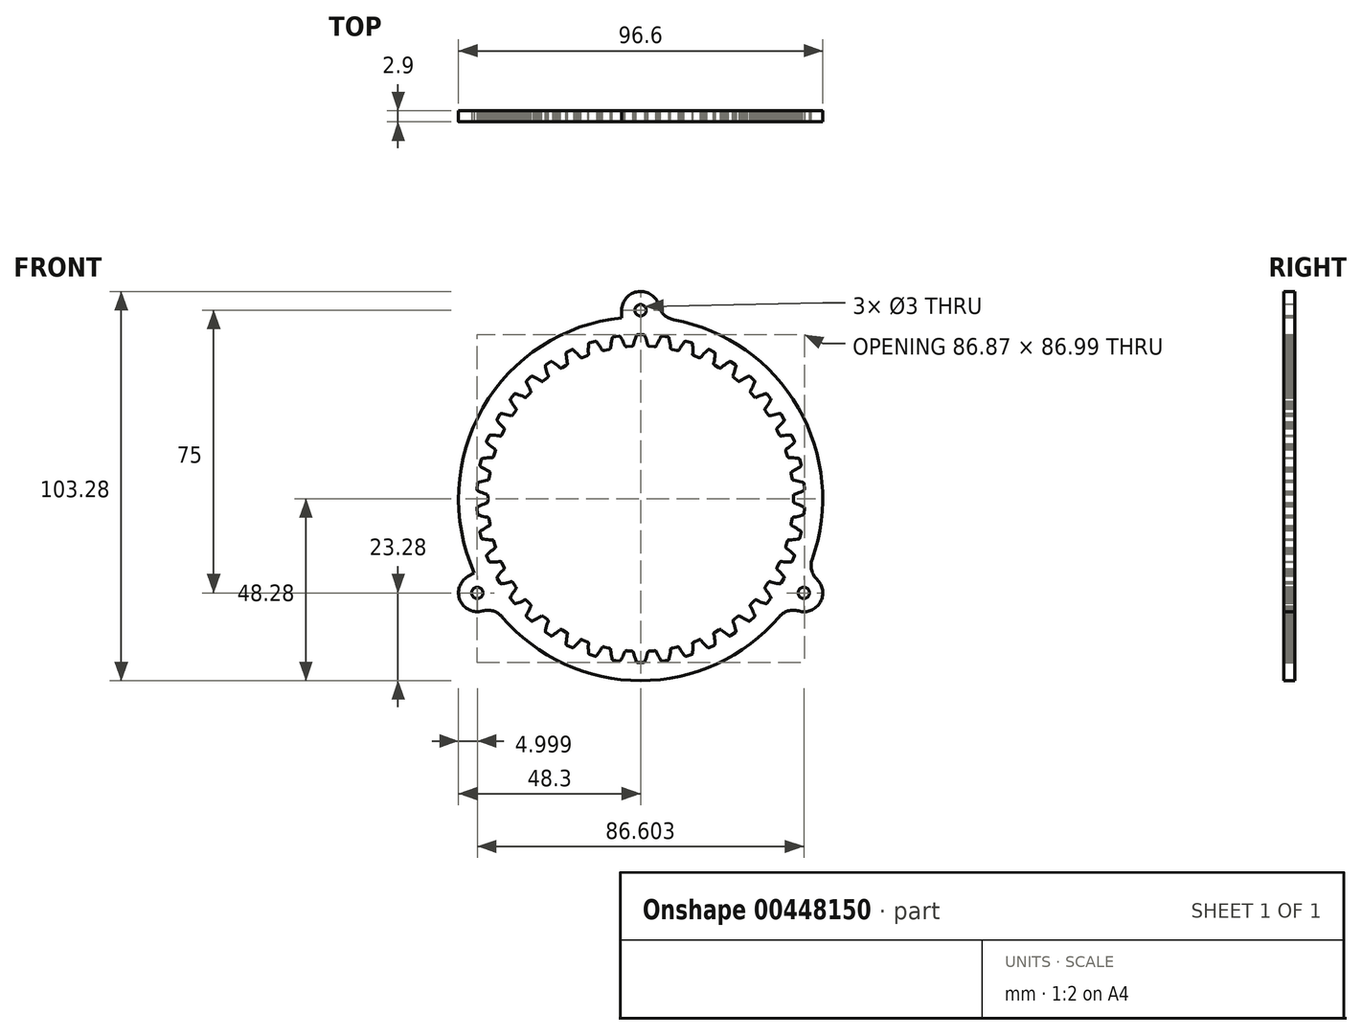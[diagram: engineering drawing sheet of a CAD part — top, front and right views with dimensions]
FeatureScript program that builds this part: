
annotation { "Feature Type Name" : "Feature", "Feature Type Description" : "" }
export const myFeature = defineFeature(function(context is Context, id is Id, definition is map)
    precondition{}
    {
        {
            var Q0;
            Q0=qCreatedBy(makeId("Front.planeOp"),FACE);
            var sketch = newSketch(context, id + "F0", { "sketchPlane" : qUnion([Q0])});
            skLineSegment(sketch, "E0", {"start": v(-40.52, 1.08) * mm, "end": v(-40.64, 1.11) * mm});
            skLineSegment(sketch, "E1", {"start": v(-40.64, 1.11) * mm, "end": v(-40.77, 1.15) * mm});
            skLineSegment(sketch, "E2", {"start": v(-40.77, 1.15) * mm, "end": v(-41.01, 1.22) * mm});
            skLineSegment(sketch, "E3", {"start": v(-41.01, 1.22) * mm, "end": v(-41.5, 1.39) * mm});
            skLineSegment(sketch, "E4", {"start": v(-41.5, 1.39) * mm, "end": v(-42, 1.58) * mm});
            skLineSegment(sketch, "E5", {"start": v(-42, 1.58) * mm, "end": v(-42.48, 1.79) * mm});
            skLineSegment(sketch, "E6", {"start": v(-42.48, 1.79) * mm, "end": v(-42.96, 2.02) * mm});
            skLineSegment(sketch, "E7", {"start": v(-42.96, 2.02) * mm, "end": v(-43.45, 2.26) * mm});
            skLineSegment(sketch, "E8", {"start": v(-43.45, 2.26) * mm, "end": v(-43.3, 4.24) * mm});
            skLineSegment(sketch, "E9", {"start": v(-43.3, 4.24) * mm, "end": v(-42.79, 4.4) * mm});
            skLineSegment(sketch, "E10", {"start": v(-42.79, 4.4) * mm, "end": v(-42.27, 4.56) * mm});
            skLineSegment(sketch, "E11", {"start": v(-42.27, 4.56) * mm, "end": v(-41.76, 4.7) * mm});
            skLineSegment(sketch, "E12", {"start": v(-41.76, 4.7) * mm, "end": v(-41.25, 4.81) * mm});
            skLineSegment(sketch, "E13", {"start": v(-41.25, 4.81) * mm, "end": v(-40.74, 4.9) * mm});
            skLineSegment(sketch, "E14", {"start": v(-40.74, 4.9) * mm, "end": v(-40.48, 4.94) * mm});
            skLineSegment(sketch, "E15", {"start": v(-40.48, 4.94) * mm, "end": v(-40.36, 4.96) * mm});
            skLineSegment(sketch, "E16", {"start": v(-40.36, 4.96) * mm, "end": v(-40.23, 4.97) * mm});
            skLineSegment(sketch, "E17", {"start": v(-40.23, 4.97) * mm, "end": v(-39.9, 7.1) * mm});
            skLineSegment(sketch, "E18", {"start": v(-39.9, 7.1) * mm, "end": v(-40.02, 7.16) * mm});
            skLineSegment(sketch, "E19", {"start": v(-40.02, 7.16) * mm, "end": v(-40.14, 7.21) * mm});
            skLineSegment(sketch, "E20", {"start": v(-40.14, 7.21) * mm, "end": v(-40.37, 7.32) * mm});
            skLineSegment(sketch, "E21", {"start": v(-40.37, 7.32) * mm, "end": v(-40.83, 7.56) * mm});
            skLineSegment(sketch, "E22", {"start": v(-40.83, 7.56) * mm, "end": v(-41.29, 7.82) * mm});
            skLineSegment(sketch, "E23", {"start": v(-41.29, 7.82) * mm, "end": v(-41.74, 8.1) * mm});
            skLineSegment(sketch, "E24", {"start": v(-41.74, 8.1) * mm, "end": v(-42.18, 8.4) * mm});
            skLineSegment(sketch, "E25", {"start": v(-42.18, 8.4) * mm, "end": v(-42.63, 8.71) * mm});
            skLineSegment(sketch, "E26", {"start": v(-42.63, 8.71) * mm, "end": v(-42.19, 10.64) * mm});
            skLineSegment(sketch, "E27", {"start": v(-42.19, 10.64) * mm, "end": v(-41.65, 10.74) * mm});
            skLineSegment(sketch, "E28", {"start": v(-41.65, 10.74) * mm, "end": v(-41.12, 10.81) * mm});
            skLineSegment(sketch, "E29", {"start": v(-41.12, 10.81) * mm, "end": v(-40.6, 10.87) * mm});
            skLineSegment(sketch, "E30", {"start": v(-40.6, 10.87) * mm, "end": v(-40.07, 10.9) * mm});
            skLineSegment(sketch, "E31", {"start": v(-40.07, 10.9) * mm, "end": v(-39.55, 10.92) * mm});
            skLineSegment(sketch, "E32", {"start": v(-39.55, 10.92) * mm, "end": v(-39.3, 10.92) * mm});
            skLineSegment(sketch, "E33", {"start": v(-39.3, 10.92) * mm, "end": v(-39.17, 10.92) * mm});
            skLineSegment(sketch, "E34", {"start": v(-39.17, 10.92) * mm, "end": v(-39.04, 10.91) * mm});
            skLineSegment(sketch, "E35", {"start": v(-39.04, 10.91) * mm, "end": v(-38.4, 12.98) * mm});
            skLineSegment(sketch, "E36", {"start": v(-38.4, 12.98) * mm, "end": v(-38.51, 13.04) * mm});
            skLineSegment(sketch, "E37", {"start": v(-38.51, 13.04) * mm, "end": v(-38.62, 13.11) * mm});
            skLineSegment(sketch, "E38", {"start": v(-38.62, 13.11) * mm, "end": v(-38.83, 13.26) * mm});
            skLineSegment(sketch, "E39", {"start": v(-38.83, 13.26) * mm, "end": v(-39.25, 13.56) * mm});
            skLineSegment(sketch, "E40", {"start": v(-39.25, 13.56) * mm, "end": v(-39.66, 13.89) * mm});
            skLineSegment(sketch, "E41", {"start": v(-39.66, 13.89) * mm, "end": v(-40.06, 14.23) * mm});
            skLineSegment(sketch, "E42", {"start": v(-40.06, 14.23) * mm, "end": v(-40.46, 14.6) * mm});
            skLineSegment(sketch, "E43", {"start": v(-40.46, 14.6) * mm, "end": v(-40.85, 14.97) * mm});
            skLineSegment(sketch, "E44", {"start": v(-40.85, 14.97) * mm, "end": v(-40.13, 16.81) * mm});
            skLineSegment(sketch, "E45", {"start": v(-40.13, 16.81) * mm, "end": v(-39.59, 16.82) * mm});
            skLineSegment(sketch, "E46", {"start": v(-39.59, 16.82) * mm, "end": v(-39.05, 16.82) * mm});
            skLineSegment(sketch, "E47", {"start": v(-39.05, 16.82) * mm, "end": v(-38.52, 16.8) * mm});
            skLineSegment(sketch, "E48", {"start": v(-38.52, 16.8) * mm, "end": v(-38, 16.76) * mm});
            skLineSegment(sketch, "E49", {"start": v(-38, 16.76) * mm, "end": v(-37.48, 16.7) * mm});
            skLineSegment(sketch, "E50", {"start": v(-37.48, 16.7) * mm, "end": v(-37.23, 16.65) * mm});
            skLineSegment(sketch, "E51", {"start": v(-37.23, 16.65) * mm, "end": v(-37.1, 16.63) * mm});
            skLineSegment(sketch, "E52", {"start": v(-37.1, 16.63) * mm, "end": v(-36.98, 16.6) * mm});
            skLineSegment(sketch, "E53", {"start": v(-36.98, 16.6) * mm, "end": v(-36.04, 18.55) * mm});
            skLineSegment(sketch, "E54", {"start": v(-36.04, 18.55) * mm, "end": v(-36.14, 18.64) * mm});
            skLineSegment(sketch, "E55", {"start": v(-36.14, 18.64) * mm, "end": v(-36.23, 18.72) * mm});
            skLineSegment(sketch, "E56", {"start": v(-36.23, 18.72) * mm, "end": v(-36.42, 18.9) * mm});
            skLineSegment(sketch, "E57", {"start": v(-36.42, 18.9) * mm, "end": v(-36.8, 19.26) * mm});
            skLineSegment(sketch, "E58", {"start": v(-36.8, 19.26) * mm, "end": v(-37.15, 19.64) * mm});
            skLineSegment(sketch, "E59", {"start": v(-37.15, 19.64) * mm, "end": v(-37.5, 20.04) * mm});
            skLineSegment(sketch, "E60", {"start": v(-37.5, 20.04) * mm, "end": v(-37.83, 20.46) * mm});
            skLineSegment(sketch, "E61", {"start": v(-37.83, 20.46) * mm, "end": v(-38.16, 20.9) * mm});
            skLineSegment(sketch, "E62", {"start": v(-38.16, 20.9) * mm, "end": v(-37.17, 22.6) * mm});
            skLineSegment(sketch, "E63", {"start": v(-37.17, 22.6) * mm, "end": v(-36.64, 22.54) * mm});
            skLineSegment(sketch, "E64", {"start": v(-36.64, 22.54) * mm, "end": v(-36.1, 22.45) * mm});
            skLineSegment(sketch, "E65", {"start": v(-36.1, 22.45) * mm, "end": v(-35.59, 22.35) * mm});
            skLineSegment(sketch, "E66", {"start": v(-35.59, 22.35) * mm, "end": v(-35.07, 22.23) * mm});
            skLineSegment(sketch, "E67", {"start": v(-35.07, 22.23) * mm, "end": v(-34.58, 22.1) * mm});
            skLineSegment(sketch, "E68", {"start": v(-34.58, 22.1) * mm, "end": v(-34.33, 22.02) * mm});
            skLineSegment(sketch, "E69", {"start": v(-34.33, 22.02) * mm, "end": v(-34.2, 21.98) * mm});
            skLineSegment(sketch, "E70", {"start": v(-34.2, 21.98) * mm, "end": v(-34.09, 21.93) * mm});
            skLineSegment(sketch, "E71", {"start": v(-34.09, 21.93) * mm, "end": v(-32.87, 23.72) * mm});
            skLineSegment(sketch, "E72", {"start": v(-32.87, 23.72) * mm, "end": v(-32.96, 23.82) * mm});
            skLineSegment(sketch, "E73", {"start": v(-32.96, 23.82) * mm, "end": v(-33.04, 23.91) * mm});
            skLineSegment(sketch, "E74", {"start": v(-33.04, 23.91) * mm, "end": v(-33.2, 24.11) * mm});
            skLineSegment(sketch, "E75", {"start": v(-33.2, 24.11) * mm, "end": v(-33.5, 24.53) * mm});
            skLineSegment(sketch, "E76", {"start": v(-33.5, 24.53) * mm, "end": v(-33.8, 24.96) * mm});
            skLineSegment(sketch, "E77", {"start": v(-33.8, 24.96) * mm, "end": v(-34.1, 25.4) * mm});
            skLineSegment(sketch, "E78", {"start": v(-34.1, 25.4) * mm, "end": v(-34.36, 25.87) * mm});
            skLineSegment(sketch, "E79", {"start": v(-34.36, 25.87) * mm, "end": v(-34.62, 26.35) * mm});
            skLineSegment(sketch, "E80", {"start": v(-34.62, 26.35) * mm, "end": v(-33.39, 27.9) * mm});
            skLineSegment(sketch, "E81", {"start": v(-33.39, 27.9) * mm, "end": v(-32.87, 27.74) * mm});
            skLineSegment(sketch, "E82", {"start": v(-32.87, 27.74) * mm, "end": v(-32.36, 27.58) * mm});
            skLineSegment(sketch, "E83", {"start": v(-32.36, 27.58) * mm, "end": v(-31.86, 27.4) * mm});
            skLineSegment(sketch, "E84", {"start": v(-31.86, 27.4) * mm, "end": v(-31.37, 27.21) * mm});
            skLineSegment(sketch, "E85", {"start": v(-31.37, 27.21) * mm, "end": v(-30.9, 27) * mm});
            skLineSegment(sketch, "E86", {"start": v(-30.9, 27) * mm, "end": v(-30.67, 26.89) * mm});
            skLineSegment(sketch, "E87", {"start": v(-30.67, 26.89) * mm, "end": v(-30.55, 26.83) * mm});
            skLineSegment(sketch, "E88", {"start": v(-30.55, 26.83) * mm, "end": v(-30.44, 26.77) * mm});
            skLineSegment(sketch, "E89", {"start": v(-30.44, 26.77) * mm, "end": v(-28.97, 28.35) * mm});
            skLineSegment(sketch, "E90", {"start": v(-28.97, 28.35) * mm, "end": v(-29.04, 28.46) * mm});
            skLineSegment(sketch, "E91", {"start": v(-29.04, 28.46) * mm, "end": v(-29.1, 28.57) * mm});
            skLineSegment(sketch, "E92", {"start": v(-29.1, 28.57) * mm, "end": v(-29.23, 28.8) * mm});
            skLineSegment(sketch, "E93", {"start": v(-29.23, 28.8) * mm, "end": v(-29.48, 29.25) * mm});
            skLineSegment(sketch, "E94", {"start": v(-29.48, 29.25) * mm, "end": v(-29.7, 29.72) * mm});
            skLineSegment(sketch, "E95", {"start": v(-29.7, 29.72) * mm, "end": v(-29.92, 30.2) * mm});
            skLineSegment(sketch, "E96", {"start": v(-29.92, 30.2) * mm, "end": v(-30.12, 30.7) * mm});
            skLineSegment(sketch, "E97", {"start": v(-30.12, 30.7) * mm, "end": v(-30.31, 31.21) * mm});
            skLineSegment(sketch, "E98", {"start": v(-30.31, 31.21) * mm, "end": v(-28.86, 32.56) * mm});
            skLineSegment(sketch, "E99", {"start": v(-28.86, 32.56) * mm, "end": v(-28.37, 32.33) * mm});
            skLineSegment(sketch, "E100", {"start": v(-28.37, 32.33) * mm, "end": v(-27.88, 32.1) * mm});
            skLineSegment(sketch, "E101", {"start": v(-27.88, 32.1) * mm, "end": v(-27.42, 31.85) * mm});
            skLineSegment(sketch, "E102", {"start": v(-27.42, 31.85) * mm, "end": v(-26.96, 31.58) * mm});
            skLineSegment(sketch, "E103", {"start": v(-26.96, 31.58) * mm, "end": v(-26.53, 31.3) * mm});
            skLineSegment(sketch, "E104", {"start": v(-26.53, 31.3) * mm, "end": v(-26.32, 31.16) * mm});
            skLineSegment(sketch, "E105", {"start": v(-26.32, 31.16) * mm, "end": v(-26.21, 31.08) * mm});
            skLineSegment(sketch, "E106", {"start": v(-26.21, 31.08) * mm, "end": v(-26.1, 31) * mm});
            skLineSegment(sketch, "E107", {"start": v(-26.1, 31) * mm, "end": v(-24.42, 32.35) * mm});
            skLineSegment(sketch, "E108", {"start": v(-24.42, 32.35) * mm, "end": v(-24.47, 32.47) * mm});
            skLineSegment(sketch, "E109", {"start": v(-24.47, 32.47) * mm, "end": v(-24.52, 32.59) * mm});
            skLineSegment(sketch, "E110", {"start": v(-24.52, 32.59) * mm, "end": v(-24.62, 32.83) * mm});
            skLineSegment(sketch, "E111", {"start": v(-24.62, 32.83) * mm, "end": v(-24.8, 33.32) * mm});
            skLineSegment(sketch, "E112", {"start": v(-24.8, 33.32) * mm, "end": v(-24.95, 33.82) * mm});
            skLineSegment(sketch, "E113", {"start": v(-24.95, 33.82) * mm, "end": v(-25.09, 34.33) * mm});
            skLineSegment(sketch, "E114", {"start": v(-25.09, 34.33) * mm, "end": v(-25.21, 34.85) * mm});
            skLineSegment(sketch, "E115", {"start": v(-25.21, 34.85) * mm, "end": v(-25.32, 35.38) * mm});
            skLineSegment(sketch, "E116", {"start": v(-25.32, 35.38) * mm, "end": v(-23.68, 36.5) * mm});
            skLineSegment(sketch, "E117", {"start": v(-23.68, 36.5) * mm, "end": v(-23.23, 36.2) * mm});
            skLineSegment(sketch, "E118", {"start": v(-23.23, 36.2) * mm, "end": v(-22.79, 35.9) * mm});
            skLineSegment(sketch, "E119", {"start": v(-22.79, 35.9) * mm, "end": v(-22.36, 35.58) * mm});
            skLineSegment(sketch, "E120", {"start": v(-22.36, 35.58) * mm, "end": v(-21.96, 35.25) * mm});
            skLineSegment(sketch, "E121", {"start": v(-21.96, 35.25) * mm, "end": v(-21.57, 34.9) * mm});
            skLineSegment(sketch, "E122", {"start": v(-21.57, 34.9) * mm, "end": v(-21.38, 34.73) * mm});
            skLineSegment(sketch, "E123", {"start": v(-21.38, 34.73) * mm, "end": v(-21.29, 34.64) * mm});
            skLineSegment(sketch, "E124", {"start": v(-21.29, 34.64) * mm, "end": v(-21.2, 34.55) * mm});
            skLineSegment(sketch, "E125", {"start": v(-21.2, 34.55) * mm, "end": v(-19.33, 35.63) * mm});
            skLineSegment(sketch, "E126", {"start": v(-19.33, 35.63) * mm, "end": v(-19.36, 35.76) * mm});
            skLineSegment(sketch, "E127", {"start": v(-19.36, 35.76) * mm, "end": v(-19.39, 35.88) * mm});
            skLineSegment(sketch, "E128", {"start": v(-19.39, 35.88) * mm, "end": v(-19.45, 36.13) * mm});
            skLineSegment(sketch, "E129", {"start": v(-19.45, 36.13) * mm, "end": v(-19.55, 36.64) * mm});
            skLineSegment(sketch, "E130", {"start": v(-19.55, 36.64) * mm, "end": v(-19.63, 37.16) * mm});
            skLineSegment(sketch, "E131", {"start": v(-19.63, 37.16) * mm, "end": v(-19.7, 37.68) * mm});
            skLineSegment(sketch, "E132", {"start": v(-19.7, 37.68) * mm, "end": v(-19.74, 38.22) * mm});
            skLineSegment(sketch, "E133", {"start": v(-19.74, 38.22) * mm, "end": v(-19.76, 38.76) * mm});
            skLineSegment(sketch, "E134", {"start": v(-19.76, 38.76) * mm, "end": v(-17.98, 39.62) * mm});
            skLineSegment(sketch, "E135", {"start": v(-17.98, 39.62) * mm, "end": v(-17.57, 39.26) * mm});
            skLineSegment(sketch, "E136", {"start": v(-17.57, 39.26) * mm, "end": v(-17.18, 38.89) * mm});
            skLineSegment(sketch, "E137", {"start": v(-17.18, 38.89) * mm, "end": v(-16.81, 38.51) * mm});
            skLineSegment(sketch, "E138", {"start": v(-16.81, 38.51) * mm, "end": v(-16.46, 38.13) * mm});
            skLineSegment(sketch, "E139", {"start": v(-16.46, 38.13) * mm, "end": v(-16.12, 37.73) * mm});
            skLineSegment(sketch, "E140", {"start": v(-16.12, 37.73) * mm, "end": v(-15.96, 37.53) * mm});
            skLineSegment(sketch, "E141", {"start": v(-15.96, 37.53) * mm, "end": v(-15.89, 37.43) * mm});
            skLineSegment(sketch, "E142", {"start": v(-15.89, 37.43) * mm, "end": v(-15.8, 37.33) * mm});
            skLineSegment(sketch, "E143", {"start": v(-15.8, 37.33) * mm, "end": v(-13.8, 38.12) * mm});
            skLineSegment(sketch, "E144", {"start": v(-13.8, 38.12) * mm, "end": v(-13.81, 38.24) * mm});
            skLineSegment(sketch, "E145", {"start": v(-13.81, 38.24) * mm, "end": v(-13.83, 38.37) * mm});
            skLineSegment(sketch, "E146", {"start": v(-13.83, 38.37) * mm, "end": v(-13.85, 38.62) * mm});
            skLineSegment(sketch, "E147", {"start": v(-13.85, 38.62) * mm, "end": v(-13.87, 39.14) * mm});
            skLineSegment(sketch, "E148", {"start": v(-13.87, 39.14) * mm, "end": v(-13.87, 39.67) * mm});
            skLineSegment(sketch, "E149", {"start": v(-13.87, 39.67) * mm, "end": v(-13.85, 40.2) * mm});
            skLineSegment(sketch, "E150", {"start": v(-13.85, 40.2) * mm, "end": v(-13.82, 40.73) * mm});
            skLineSegment(sketch, "E151", {"start": v(-13.82, 40.73) * mm, "end": v(-13.77, 41.27) * mm});
            skLineSegment(sketch, "E152", {"start": v(-13.77, 41.27) * mm, "end": v(-11.87, 41.86) * mm});
            skLineSegment(sketch, "E153", {"start": v(-11.87, 41.86) * mm, "end": v(-11.53, 41.44) * mm});
            skLineSegment(sketch, "E154", {"start": v(-11.53, 41.44) * mm, "end": v(-11.2, 41.02) * mm});
            skLineSegment(sketch, "E155", {"start": v(-11.2, 41.02) * mm, "end": v(-10.88, 40.59) * mm});
            skLineSegment(sketch, "E156", {"start": v(-10.88, 40.59) * mm, "end": v(-10.6, 40.15) * mm});
            skLineSegment(sketch, "E157", {"start": v(-10.6, 40.15) * mm, "end": v(-10.32, 39.71) * mm});
            skLineSegment(sketch, "E158", {"start": v(-10.32, 39.71) * mm, "end": v(-10.2, 39.49) * mm});
            skLineSegment(sketch, "E159", {"start": v(-10.2, 39.49) * mm, "end": v(-10.13, 39.38) * mm});
            skLineSegment(sketch, "E160", {"start": v(-10.13, 39.38) * mm, "end": v(-10.07, 39.27) * mm});
            skLineSegment(sketch, "E161", {"start": v(-10.07, 39.27) * mm, "end": v(-7.96, 39.75) * mm});
            skLineSegment(sketch, "E162", {"start": v(-7.96, 39.75) * mm, "end": v(-7.96, 39.87) * mm});
            skLineSegment(sketch, "E163", {"start": v(-7.96, 39.87) * mm, "end": v(-7.95, 40) * mm});
            skLineSegment(sketch, "E164", {"start": v(-7.95, 40) * mm, "end": v(-7.93, 40.26) * mm});
            skLineSegment(sketch, "E165", {"start": v(-7.93, 40.26) * mm, "end": v(-7.88, 40.77) * mm});
            skLineSegment(sketch, "E166", {"start": v(-7.88, 40.77) * mm, "end": v(-7.8, 41.3) * mm});
            skLineSegment(sketch, "E167", {"start": v(-7.8, 41.3) * mm, "end": v(-7.7, 41.81) * mm});
            skLineSegment(sketch, "E168", {"start": v(-7.7, 41.81) * mm, "end": v(-7.6, 42.34) * mm});
            skLineSegment(sketch, "E169", {"start": v(-7.6, 42.34) * mm, "end": v(-7.46, 42.86) * mm});
            skLineSegment(sketch, "E170", {"start": v(-7.46, 42.86) * mm, "end": v(-5.5, 43.16) * mm});
            skLineSegment(sketch, "E171", {"start": v(-5.5, 43.16) * mm, "end": v(-5.22, 42.7) * mm});
            skLineSegment(sketch, "E172", {"start": v(-5.22, 42.7) * mm, "end": v(-4.96, 42.23) * mm});
            skLineSegment(sketch, "E173", {"start": v(-4.96, 42.23) * mm, "end": v(-4.71, 41.76) * mm});
            skLineSegment(sketch, "E174", {"start": v(-4.71, 41.76) * mm, "end": v(-4.49, 41.28) * mm});
            skLineSegment(sketch, "E175", {"start": v(-4.49, 41.28) * mm, "end": v(-4.28, 40.8) * mm});
            skLineSegment(sketch, "E176", {"start": v(-4.28, 40.8) * mm, "end": v(-4.2, 40.57) * mm});
            skLineSegment(sketch, "E177", {"start": v(-4.2, 40.57) * mm, "end": v(-4.15, 40.45) * mm});
            skLineSegment(sketch, "E178", {"start": v(-4.15, 40.45) * mm, "end": v(-4.1, 40.33) * mm});
            skLineSegment(sketch, "E179", {"start": v(-4.1, 40.33) * mm, "end": v(-1.95, 40.49) * mm});
            skLineSegment(sketch, "E180", {"start": v(-1.95, 40.49) * mm, "end": v(-1.93, 40.61) * mm});
            skLineSegment(sketch, "E181", {"start": v(-1.93, 40.61) * mm, "end": v(-1.9, 40.74) * mm});
            skLineSegment(sketch, "E182", {"start": v(-1.9, 40.74) * mm, "end": v(-1.85, 40.99) * mm});
            skLineSegment(sketch, "E183", {"start": v(-1.85, 40.99) * mm, "end": v(-1.72, 41.5) * mm});
            skLineSegment(sketch, "E184", {"start": v(-1.72, 41.5) * mm, "end": v(-1.56, 42) * mm});
            skLineSegment(sketch, "E185", {"start": v(-1.56, 42) * mm, "end": v(-1.4, 42.5) * mm});
            skLineSegment(sketch, "E186", {"start": v(-1.4, 42.5) * mm, "end": v(-1.2, 43) * mm});
            skLineSegment(sketch, "E187", {"start": v(-1.2, 43) * mm, "end": v(-0.99, 43.5) * mm});
            skLineSegment(sketch, "E188", {"start": v(-0.99, 43.5) * mm, "end": v(0.99, 43.5) * mm});
            skLineSegment(sketch, "E189", {"start": v(0.99, 43.5) * mm, "end": v(1.2, 43) * mm});
            skLineSegment(sketch, "E190", {"start": v(1.2, 43) * mm, "end": v(1.4, 42.5) * mm});
            skLineSegment(sketch, "E191", {"start": v(1.4, 42.5) * mm, "end": v(1.56, 42) * mm});
            skLineSegment(sketch, "E192", {"start": v(1.56, 42) * mm, "end": v(1.72, 41.5) * mm});
            skLineSegment(sketch, "E193", {"start": v(1.72, 41.5) * mm, "end": v(1.85, 40.99) * mm});
            skLineSegment(sketch, "E194", {"start": v(1.85, 40.99) * mm, "end": v(1.9, 40.74) * mm});
            skLineSegment(sketch, "E195", {"start": v(1.9, 40.74) * mm, "end": v(1.93, 40.61) * mm});
            skLineSegment(sketch, "E196", {"start": v(1.93, 40.61) * mm, "end": v(1.95, 40.49) * mm});
            skLineSegment(sketch, "E197", {"start": v(1.95, 40.49) * mm, "end": v(4.1, 40.33) * mm});
            skLineSegment(sketch, "E198", {"start": v(4.1, 40.33) * mm, "end": v(4.15, 40.45) * mm});
            skLineSegment(sketch, "E199", {"start": v(4.15, 40.45) * mm, "end": v(4.2, 40.57) * mm});
            skLineSegment(sketch, "E200", {"start": v(4.2, 40.57) * mm, "end": v(4.28, 40.8) * mm});
            skLineSegment(sketch, "E201", {"start": v(4.28, 40.8) * mm, "end": v(4.49, 41.28) * mm});
            skLineSegment(sketch, "E202", {"start": v(4.49, 41.28) * mm, "end": v(4.71, 41.76) * mm});
            skLineSegment(sketch, "E203", {"start": v(4.71, 41.76) * mm, "end": v(4.96, 42.23) * mm});
            skLineSegment(sketch, "E204", {"start": v(4.96, 42.23) * mm, "end": v(5.22, 42.7) * mm});
            skLineSegment(sketch, "E205", {"start": v(5.22, 42.7) * mm, "end": v(5.5, 43.16) * mm});
            skLineSegment(sketch, "E206", {"start": v(5.5, 43.16) * mm, "end": v(7.46, 42.86) * mm});
            skLineSegment(sketch, "E207", {"start": v(7.46, 42.86) * mm, "end": v(7.6, 42.34) * mm});
            skLineSegment(sketch, "E208", {"start": v(7.6, 42.34) * mm, "end": v(7.7, 41.81) * mm});
            skLineSegment(sketch, "E209", {"start": v(7.7, 41.81) * mm, "end": v(7.8, 41.3) * mm});
            skLineSegment(sketch, "E210", {"start": v(7.8, 41.3) * mm, "end": v(7.88, 40.77) * mm});
            skLineSegment(sketch, "E211", {"start": v(7.88, 40.77) * mm, "end": v(7.93, 40.26) * mm});
            skLineSegment(sketch, "E212", {"start": v(7.93, 40.26) * mm, "end": v(7.95, 40) * mm});
            skLineSegment(sketch, "E213", {"start": v(7.95, 40) * mm, "end": v(7.96, 39.87) * mm});
            skLineSegment(sketch, "E214", {"start": v(7.96, 39.87) * mm, "end": v(7.96, 39.75) * mm});
            skLineSegment(sketch, "E215", {"start": v(7.96, 39.75) * mm, "end": v(10.07, 39.27) * mm});
            skLineSegment(sketch, "E216", {"start": v(10.07, 39.27) * mm, "end": v(10.13, 39.38) * mm});
            skLineSegment(sketch, "E217", {"start": v(10.13, 39.38) * mm, "end": v(10.2, 39.49) * mm});
            skLineSegment(sketch, "E218", {"start": v(10.2, 39.49) * mm, "end": v(10.32, 39.71) * mm});
            skLineSegment(sketch, "E219", {"start": v(10.32, 39.71) * mm, "end": v(10.6, 40.15) * mm});
            skLineSegment(sketch, "E220", {"start": v(10.6, 40.15) * mm, "end": v(10.88, 40.59) * mm});
            skLineSegment(sketch, "E221", {"start": v(10.88, 40.59) * mm, "end": v(11.2, 41.02) * mm});
            skLineSegment(sketch, "E222", {"start": v(11.2, 41.02) * mm, "end": v(11.53, 41.44) * mm});
            skLineSegment(sketch, "E223", {"start": v(11.53, 41.44) * mm, "end": v(11.87, 41.86) * mm});
            skLineSegment(sketch, "E224", {"start": v(11.87, 41.86) * mm, "end": v(13.77, 41.27) * mm});
            skLineSegment(sketch, "E225", {"start": v(13.77, 41.27) * mm, "end": v(13.82, 40.73) * mm});
            skLineSegment(sketch, "E226", {"start": v(13.82, 40.73) * mm, "end": v(13.85, 40.2) * mm});
            skLineSegment(sketch, "E227", {"start": v(13.85, 40.2) * mm, "end": v(13.87, 39.67) * mm});
            skLineSegment(sketch, "E228", {"start": v(13.87, 39.67) * mm, "end": v(13.87, 39.14) * mm});
            skLineSegment(sketch, "E229", {"start": v(13.87, 39.14) * mm, "end": v(13.85, 38.62) * mm});
            skLineSegment(sketch, "E230", {"start": v(13.85, 38.62) * mm, "end": v(13.83, 38.37) * mm});
            skLineSegment(sketch, "E231", {"start": v(13.83, 38.37) * mm, "end": v(13.81, 38.24) * mm});
            skLineSegment(sketch, "E232", {"start": v(13.81, 38.24) * mm, "end": v(13.8, 38.12) * mm});
            skLineSegment(sketch, "E233", {"start": v(13.8, 38.12) * mm, "end": v(15.8, 37.33) * mm});
            skLineSegment(sketch, "E234", {"start": v(15.8, 37.33) * mm, "end": v(15.89, 37.43) * mm});
            skLineSegment(sketch, "E235", {"start": v(15.89, 37.43) * mm, "end": v(15.96, 37.53) * mm});
            skLineSegment(sketch, "E236", {"start": v(15.96, 37.53) * mm, "end": v(16.12, 37.73) * mm});
            skLineSegment(sketch, "E237", {"start": v(16.12, 37.73) * mm, "end": v(16.46, 38.13) * mm});
            skLineSegment(sketch, "E238", {"start": v(16.46, 38.13) * mm, "end": v(16.81, 38.51) * mm});
            skLineSegment(sketch, "E239", {"start": v(16.81, 38.51) * mm, "end": v(17.18, 38.89) * mm});
            skLineSegment(sketch, "E240", {"start": v(17.18, 38.89) * mm, "end": v(17.57, 39.26) * mm});
            skLineSegment(sketch, "E241", {"start": v(17.57, 39.26) * mm, "end": v(17.98, 39.62) * mm});
            skLineSegment(sketch, "E242", {"start": v(17.98, 39.62) * mm, "end": v(19.76, 38.76) * mm});
            skLineSegment(sketch, "E243", {"start": v(19.76, 38.76) * mm, "end": v(19.74, 38.22) * mm});
            skLineSegment(sketch, "E244", {"start": v(19.74, 38.22) * mm, "end": v(19.7, 37.68) * mm});
            skLineSegment(sketch, "E245", {"start": v(19.7, 37.68) * mm, "end": v(19.63, 37.16) * mm});
            skLineSegment(sketch, "E246", {"start": v(19.63, 37.16) * mm, "end": v(19.55, 36.64) * mm});
            skLineSegment(sketch, "E247", {"start": v(19.55, 36.64) * mm, "end": v(19.45, 36.13) * mm});
            skLineSegment(sketch, "E248", {"start": v(19.45, 36.13) * mm, "end": v(19.39, 35.88) * mm});
            skLineSegment(sketch, "E249", {"start": v(19.39, 35.88) * mm, "end": v(19.36, 35.76) * mm});
            skLineSegment(sketch, "E250", {"start": v(19.36, 35.76) * mm, "end": v(19.33, 35.63) * mm});
            skLineSegment(sketch, "E251", {"start": v(19.33, 35.63) * mm, "end": v(21.2, 34.55) * mm});
            skLineSegment(sketch, "E252", {"start": v(21.2, 34.55) * mm, "end": v(21.29, 34.64) * mm});
            skLineSegment(sketch, "E253", {"start": v(21.29, 34.64) * mm, "end": v(21.38, 34.73) * mm});
            skLineSegment(sketch, "E254", {"start": v(21.38, 34.73) * mm, "end": v(21.57, 34.9) * mm});
            skLineSegment(sketch, "E255", {"start": v(21.57, 34.9) * mm, "end": v(21.96, 35.25) * mm});
            skLineSegment(sketch, "E256", {"start": v(21.96, 35.25) * mm, "end": v(22.36, 35.58) * mm});
            skLineSegment(sketch, "E257", {"start": v(22.36, 35.58) * mm, "end": v(22.79, 35.9) * mm});
            skLineSegment(sketch, "E258", {"start": v(22.79, 35.9) * mm, "end": v(23.23, 36.2) * mm});
            skLineSegment(sketch, "E259", {"start": v(23.23, 36.2) * mm, "end": v(23.68, 36.5) * mm});
            skLineSegment(sketch, "E260", {"start": v(23.68, 36.5) * mm, "end": v(25.32, 35.38) * mm});
            skLineSegment(sketch, "E261", {"start": v(25.32, 35.38) * mm, "end": v(25.21, 34.85) * mm});
            skLineSegment(sketch, "E262", {"start": v(25.21, 34.85) * mm, "end": v(25.09, 34.33) * mm});
            skLineSegment(sketch, "E263", {"start": v(25.09, 34.33) * mm, "end": v(24.95, 33.82) * mm});
            skLineSegment(sketch, "E264", {"start": v(24.95, 33.82) * mm, "end": v(24.8, 33.32) * mm});
            skLineSegment(sketch, "E265", {"start": v(24.8, 33.32) * mm, "end": v(24.62, 32.83) * mm});
            skLineSegment(sketch, "E266", {"start": v(24.62, 32.83) * mm, "end": v(24.52, 32.59) * mm});
            skLineSegment(sketch, "E267", {"start": v(24.52, 32.59) * mm, "end": v(24.47, 32.47) * mm});
            skLineSegment(sketch, "E268", {"start": v(24.47, 32.47) * mm, "end": v(24.42, 32.35) * mm});
            skLineSegment(sketch, "E269", {"start": v(24.42, 32.35) * mm, "end": v(26.1, 31) * mm});
            skLineSegment(sketch, "E270", {"start": v(26.1, 31) * mm, "end": v(26.21, 31.08) * mm});
            skLineSegment(sketch, "E271", {"start": v(26.21, 31.08) * mm, "end": v(26.32, 31.16) * mm});
            skLineSegment(sketch, "E272", {"start": v(26.32, 31.16) * mm, "end": v(26.53, 31.3) * mm});
            skLineSegment(sketch, "E273", {"start": v(26.53, 31.3) * mm, "end": v(26.96, 31.58) * mm});
            skLineSegment(sketch, "E274", {"start": v(26.96, 31.58) * mm, "end": v(27.42, 31.85) * mm});
            skLineSegment(sketch, "E275", {"start": v(27.42, 31.85) * mm, "end": v(27.88, 32.1) * mm});
            skLineSegment(sketch, "E276", {"start": v(27.88, 32.1) * mm, "end": v(28.36, 32.33) * mm});
            skLineSegment(sketch, "E277", {"start": v(28.36, 32.33) * mm, "end": v(28.86, 32.56) * mm});
            skLineSegment(sketch, "E278", {"start": v(28.86, 32.56) * mm, "end": v(30.31, 31.21) * mm});
            skLineSegment(sketch, "E279", {"start": v(30.31, 31.21) * mm, "end": v(30.12, 30.7) * mm});
            skLineSegment(sketch, "E280", {"start": v(30.12, 30.7) * mm, "end": v(29.92, 30.2) * mm});
            skLineSegment(sketch, "E281", {"start": v(29.92, 30.2) * mm, "end": v(29.7, 29.72) * mm});
            skLineSegment(sketch, "E282", {"start": v(29.7, 29.72) * mm, "end": v(29.48, 29.25) * mm});
            skLineSegment(sketch, "E283", {"start": v(29.48, 29.25) * mm, "end": v(29.23, 28.8) * mm});
            skLineSegment(sketch, "E284", {"start": v(29.23, 28.8) * mm, "end": v(29.1, 28.57) * mm});
            skLineSegment(sketch, "E285", {"start": v(29.1, 28.57) * mm, "end": v(29.04, 28.46) * mm});
            skLineSegment(sketch, "E286", {"start": v(29.04, 28.46) * mm, "end": v(28.97, 28.35) * mm});
            skLineSegment(sketch, "E287", {"start": v(28.97, 28.35) * mm, "end": v(30.44, 26.77) * mm});
            skLineSegment(sketch, "E288", {"start": v(30.44, 26.77) * mm, "end": v(30.55, 26.83) * mm});
            skLineSegment(sketch, "E289", {"start": v(30.55, 26.83) * mm, "end": v(30.67, 26.89) * mm});
            skLineSegment(sketch, "E290", {"start": v(30.67, 26.89) * mm, "end": v(30.9, 27) * mm});
            skLineSegment(sketch, "E291", {"start": v(30.9, 27) * mm, "end": v(31.37, 27.21) * mm});
            skLineSegment(sketch, "E292", {"start": v(31.37, 27.21) * mm, "end": v(31.86, 27.4) * mm});
            skLineSegment(sketch, "E293", {"start": v(31.86, 27.4) * mm, "end": v(32.36, 27.58) * mm});
            skLineSegment(sketch, "E294", {"start": v(32.36, 27.58) * mm, "end": v(32.87, 27.74) * mm});
            skLineSegment(sketch, "E295", {"start": v(32.87, 27.74) * mm, "end": v(33.39, 27.9) * mm});
            skLineSegment(sketch, "E296", {"start": v(33.39, 27.9) * mm, "end": v(34.62, 26.35) * mm});
            skLineSegment(sketch, "E297", {"start": v(34.62, 26.35) * mm, "end": v(34.36, 25.87) * mm});
            skLineSegment(sketch, "E298", {"start": v(34.36, 25.87) * mm, "end": v(34.1, 25.4) * mm});
            skLineSegment(sketch, "E299", {"start": v(34.1, 25.4) * mm, "end": v(33.8, 24.96) * mm});
            skLineSegment(sketch, "E300", {"start": v(33.8, 24.96) * mm, "end": v(33.5, 24.53) * mm});
            skLineSegment(sketch, "E301", {"start": v(33.5, 24.53) * mm, "end": v(33.2, 24.11) * mm});
            skLineSegment(sketch, "E302", {"start": v(33.2, 24.11) * mm, "end": v(33.04, 23.91) * mm});
            skLineSegment(sketch, "E303", {"start": v(33.04, 23.91) * mm, "end": v(32.95, 23.82) * mm});
            skLineSegment(sketch, "E304", {"start": v(32.95, 23.82) * mm, "end": v(32.87, 23.72) * mm});
            skLineSegment(sketch, "E305", {"start": v(32.87, 23.72) * mm, "end": v(34.09, 21.93) * mm});
            skLineSegment(sketch, "E306", {"start": v(34.09, 21.93) * mm, "end": v(34.2, 21.98) * mm});
            skLineSegment(sketch, "E307", {"start": v(34.2, 21.98) * mm, "end": v(34.33, 22.02) * mm});
            skLineSegment(sketch, "E308", {"start": v(34.33, 22.02) * mm, "end": v(34.58, 22.1) * mm});
            skLineSegment(sketch, "E309", {"start": v(34.58, 22.1) * mm, "end": v(35.07, 22.23) * mm});
            skLineSegment(sketch, "E310", {"start": v(35.07, 22.23) * mm, "end": v(35.58, 22.35) * mm});
            skLineSegment(sketch, "E311", {"start": v(35.58, 22.35) * mm, "end": v(36.1, 22.45) * mm});
            skLineSegment(sketch, "E312", {"start": v(36.1, 22.45) * mm, "end": v(36.64, 22.54) * mm});
            skLineSegment(sketch, "E313", {"start": v(36.64, 22.54) * mm, "end": v(37.17, 22.6) * mm});
            skLineSegment(sketch, "E314", {"start": v(37.17, 22.6) * mm, "end": v(38.16, 20.9) * mm});
            skLineSegment(sketch, "E315", {"start": v(38.16, 20.9) * mm, "end": v(37.83, 20.46) * mm});
            skLineSegment(sketch, "E316", {"start": v(37.83, 20.46) * mm, "end": v(37.5, 20.04) * mm});
            skLineSegment(sketch, "E317", {"start": v(37.5, 20.04) * mm, "end": v(37.15, 19.64) * mm});
            skLineSegment(sketch, "E318", {"start": v(37.15, 19.64) * mm, "end": v(36.79, 19.26) * mm});
            skLineSegment(sketch, "E319", {"start": v(36.79, 19.26) * mm, "end": v(36.42, 18.9) * mm});
            skLineSegment(sketch, "E320", {"start": v(36.42, 18.9) * mm, "end": v(36.23, 18.72) * mm});
            skLineSegment(sketch, "E321", {"start": v(36.23, 18.72) * mm, "end": v(36.14, 18.64) * mm});
            skLineSegment(sketch, "E322", {"start": v(36.14, 18.64) * mm, "end": v(36.04, 18.55) * mm});
            skLineSegment(sketch, "E323", {"start": v(36.04, 18.55) * mm, "end": v(36.98, 16.6) * mm});
            skLineSegment(sketch, "E324", {"start": v(36.98, 16.6) * mm, "end": v(37.1, 16.63) * mm});
            skLineSegment(sketch, "E325", {"start": v(37.1, 16.63) * mm, "end": v(37.23, 16.65) * mm});
            skLineSegment(sketch, "E326", {"start": v(37.23, 16.65) * mm, "end": v(37.48, 16.7) * mm});
            skLineSegment(sketch, "E327", {"start": v(37.48, 16.7) * mm, "end": v(38, 16.76) * mm});
            skLineSegment(sketch, "E328", {"start": v(38, 16.76) * mm, "end": v(38.52, 16.8) * mm});
            skLineSegment(sketch, "E329", {"start": v(38.52, 16.8) * mm, "end": v(39.05, 16.82) * mm});
            skLineSegment(sketch, "E330", {"start": v(39.05, 16.82) * mm, "end": v(39.58, 16.82) * mm});
            skLineSegment(sketch, "E331", {"start": v(39.58, 16.82) * mm, "end": v(40.13, 16.81) * mm});
            skLineSegment(sketch, "E332", {"start": v(40.13, 16.81) * mm, "end": v(40.85, 14.97) * mm});
            skLineSegment(sketch, "E333", {"start": v(40.85, 14.97) * mm, "end": v(40.46, 14.6) * mm});
            skLineSegment(sketch, "E334", {"start": v(40.46, 14.6) * mm, "end": v(40.06, 14.23) * mm});
            skLineSegment(sketch, "E335", {"start": v(40.06, 14.23) * mm, "end": v(39.66, 13.89) * mm});
            skLineSegment(sketch, "E336", {"start": v(39.66, 13.89) * mm, "end": v(39.25, 13.56) * mm});
            skLineSegment(sketch, "E337", {"start": v(39.25, 13.56) * mm, "end": v(38.83, 13.26) * mm});
            skLineSegment(sketch, "E338", {"start": v(38.83, 13.26) * mm, "end": v(38.62, 13.11) * mm});
            skLineSegment(sketch, "E339", {"start": v(38.62, 13.11) * mm, "end": v(38.51, 13.04) * mm});
            skLineSegment(sketch, "E340", {"start": v(38.51, 13.04) * mm, "end": v(38.4, 12.98) * mm});
            skLineSegment(sketch, "E341", {"start": v(38.4, 12.98) * mm, "end": v(39.04, 10.91) * mm});
            skLineSegment(sketch, "E342", {"start": v(39.04, 10.91) * mm, "end": v(39.17, 10.92) * mm});
            skLineSegment(sketch, "E343", {"start": v(39.17, 10.92) * mm, "end": v(39.3, 10.92) * mm});
            skLineSegment(sketch, "E344", {"start": v(39.3, 10.92) * mm, "end": v(39.55, 10.92) * mm});
            skLineSegment(sketch, "E345", {"start": v(39.55, 10.92) * mm, "end": v(40.07, 10.9) * mm});
            skLineSegment(sketch, "E346", {"start": v(40.07, 10.9) * mm, "end": v(40.6, 10.87) * mm});
            skLineSegment(sketch, "E347", {"start": v(40.6, 10.87) * mm, "end": v(41.12, 10.81) * mm});
            skLineSegment(sketch, "E348", {"start": v(41.12, 10.81) * mm, "end": v(41.65, 10.74) * mm});
            skLineSegment(sketch, "E349", {"start": v(41.65, 10.74) * mm, "end": v(42.19, 10.64) * mm});
            skLineSegment(sketch, "E350", {"start": v(42.19, 10.64) * mm, "end": v(42.63, 8.71) * mm});
            skLineSegment(sketch, "E351", {"start": v(42.63, 8.71) * mm, "end": v(42.18, 8.4) * mm});
            skLineSegment(sketch, "E352", {"start": v(42.18, 8.4) * mm, "end": v(41.74, 8.1) * mm});
            skLineSegment(sketch, "E353", {"start": v(41.74, 8.1) * mm, "end": v(41.29, 7.82) * mm});
            skLineSegment(sketch, "E354", {"start": v(41.29, 7.82) * mm, "end": v(40.83, 7.56) * mm});
            skLineSegment(sketch, "E355", {"start": v(40.83, 7.56) * mm, "end": v(40.37, 7.32) * mm});
            skLineSegment(sketch, "E356", {"start": v(40.37, 7.32) * mm, "end": v(40.14, 7.21) * mm});
            skLineSegment(sketch, "E357", {"start": v(40.14, 7.21) * mm, "end": v(40.02, 7.16) * mm});
            skLineSegment(sketch, "E358", {"start": v(40.02, 7.16) * mm, "end": v(39.9, 7.1) * mm});
            skLineSegment(sketch, "E359", {"start": v(39.9, 7.1) * mm, "end": v(40.23, 4.97) * mm});
            skLineSegment(sketch, "E360", {"start": v(40.23, 4.97) * mm, "end": v(40.36, 4.96) * mm});
            skLineSegment(sketch, "E361", {"start": v(40.36, 4.96) * mm, "end": v(40.48, 4.94) * mm});
            skLineSegment(sketch, "E362", {"start": v(40.48, 4.94) * mm, "end": v(40.74, 4.9) * mm});
            skLineSegment(sketch, "E363", {"start": v(40.74, 4.9) * mm, "end": v(41.25, 4.81) * mm});
            skLineSegment(sketch, "E364", {"start": v(41.25, 4.81) * mm, "end": v(41.76, 4.7) * mm});
            skLineSegment(sketch, "E365", {"start": v(41.76, 4.7) * mm, "end": v(42.27, 4.56) * mm});
            skLineSegment(sketch, "E366", {"start": v(42.27, 4.56) * mm, "end": v(42.79, 4.4) * mm});
            skLineSegment(sketch, "E367", {"start": v(42.79, 4.4) * mm, "end": v(43.3, 4.24) * mm});
            skLineSegment(sketch, "E368", {"start": v(43.3, 4.24) * mm, "end": v(43.45, 2.26) * mm});
            skLineSegment(sketch, "E369", {"start": v(43.45, 2.26) * mm, "end": v(42.96, 2.02) * mm});
            skLineSegment(sketch, "E370", {"start": v(42.96, 2.02) * mm, "end": v(42.48, 1.79) * mm});
            skLineSegment(sketch, "E371", {"start": v(42.48, 1.79) * mm, "end": v(42, 1.58) * mm});
            skLineSegment(sketch, "E372", {"start": v(42, 1.58) * mm, "end": v(41.5, 1.39) * mm});
            skLineSegment(sketch, "E373", {"start": v(41.5, 1.39) * mm, "end": v(41.01, 1.22) * mm});
            skLineSegment(sketch, "E374", {"start": v(41.01, 1.22) * mm, "end": v(40.77, 1.15) * mm});
            skLineSegment(sketch, "E375", {"start": v(40.77, 1.15) * mm, "end": v(40.64, 1.11) * mm});
            skLineSegment(sketch, "E376", {"start": v(40.64, 1.11) * mm, "end": v(40.52, 1.08) * mm});
            skLineSegment(sketch, "E377", {"start": v(40.52, 1.08) * mm, "end": v(40.52, -1.08) * mm});
            skLineSegment(sketch, "E378", {"start": v(40.52, -1.08) * mm, "end": v(40.64, -1.11) * mm});
            skLineSegment(sketch, "E379", {"start": v(40.64, -1.11) * mm, "end": v(40.77, -1.15) * mm});
            skLineSegment(sketch, "E380", {"start": v(40.77, -1.15) * mm, "end": v(41.01, -1.22) * mm});
            skLineSegment(sketch, "E381", {"start": v(41.01, -1.22) * mm, "end": v(41.5, -1.4) * mm});
            skLineSegment(sketch, "E382", {"start": v(41.5, -1.4) * mm, "end": v(42, -1.58) * mm});
            skLineSegment(sketch, "E383", {"start": v(42, -1.58) * mm, "end": v(42.48, -1.79) * mm});
            skLineSegment(sketch, "E384", {"start": v(42.48, -1.79) * mm, "end": v(42.96, -2.02) * mm});
            skLineSegment(sketch, "E385", {"start": v(42.96, -2.02) * mm, "end": v(43.45, -2.26) * mm});
            skLineSegment(sketch, "E386", {"start": v(43.45, -2.26) * mm, "end": v(43.3, -4.24) * mm});
            skLineSegment(sketch, "E387", {"start": v(43.3, -4.24) * mm, "end": v(42.79, -4.4) * mm});
            skLineSegment(sketch, "E388", {"start": v(42.79, -4.4) * mm, "end": v(42.27, -4.56) * mm});
            skLineSegment(sketch, "E389", {"start": v(42.27, -4.56) * mm, "end": v(41.76, -4.7) * mm});
            skLineSegment(sketch, "E390", {"start": v(41.76, -4.7) * mm, "end": v(41.25, -4.81) * mm});
            skLineSegment(sketch, "E391", {"start": v(41.25, -4.81) * mm, "end": v(40.74, -4.9) * mm});
            skLineSegment(sketch, "E392", {"start": v(40.74, -4.9) * mm, "end": v(40.48, -4.94) * mm});
            skLineSegment(sketch, "E393", {"start": v(40.48, -4.94) * mm, "end": v(40.36, -4.96) * mm});
            skLineSegment(sketch, "E394", {"start": v(40.36, -4.96) * mm, "end": v(40.23, -4.97) * mm});
            skLineSegment(sketch, "E395", {"start": v(40.23, -4.97) * mm, "end": v(39.9, -7.1) * mm});
            skLineSegment(sketch, "E396", {"start": v(39.9, -7.1) * mm, "end": v(40.02, -7.16) * mm});
            skLineSegment(sketch, "E397", {"start": v(40.02, -7.16) * mm, "end": v(40.14, -7.21) * mm});
            skLineSegment(sketch, "E398", {"start": v(40.14, -7.21) * mm, "end": v(40.37, -7.32) * mm});
            skLineSegment(sketch, "E399", {"start": v(40.37, -7.32) * mm, "end": v(40.83, -7.56) * mm});
            skLineSegment(sketch, "E400", {"start": v(40.83, -7.56) * mm, "end": v(41.29, -7.82) * mm});
            skLineSegment(sketch, "E401", {"start": v(41.29, -7.82) * mm, "end": v(41.74, -8.1) * mm});
            skLineSegment(sketch, "E402", {"start": v(41.74, -8.1) * mm, "end": v(42.18, -8.4) * mm});
            skLineSegment(sketch, "E403", {"start": v(42.18, -8.4) * mm, "end": v(42.63, -8.71) * mm});
            skLineSegment(sketch, "E404", {"start": v(42.63, -8.71) * mm, "end": v(42.19, -10.64) * mm});
            skLineSegment(sketch, "E405", {"start": v(42.19, -10.64) * mm, "end": v(41.65, -10.74) * mm});
            skLineSegment(sketch, "E406", {"start": v(41.65, -10.74) * mm, "end": v(41.12, -10.81) * mm});
            skLineSegment(sketch, "E407", {"start": v(41.12, -10.81) * mm, "end": v(40.6, -10.87) * mm});
            skLineSegment(sketch, "E408", {"start": v(40.6, -10.87) * mm, "end": v(40.07, -10.9) * mm});
            skLineSegment(sketch, "E409", {"start": v(40.07, -10.9) * mm, "end": v(39.55, -10.92) * mm});
            skLineSegment(sketch, "E410", {"start": v(39.55, -10.92) * mm, "end": v(39.3, -10.92) * mm});
            skLineSegment(sketch, "E411", {"start": v(39.3, -10.92) * mm, "end": v(39.17, -10.92) * mm});
            skLineSegment(sketch, "E412", {"start": v(39.17, -10.92) * mm, "end": v(39.04, -10.91) * mm});
            skLineSegment(sketch, "E413", {"start": v(39.04, -10.91) * mm, "end": v(38.4, -12.98) * mm});
            skLineSegment(sketch, "E414", {"start": v(38.4, -12.98) * mm, "end": v(38.51, -13.04) * mm});
            skLineSegment(sketch, "E415", {"start": v(38.51, -13.04) * mm, "end": v(38.62, -13.11) * mm});
            skLineSegment(sketch, "E416", {"start": v(38.62, -13.11) * mm, "end": v(38.83, -13.26) * mm});
            skLineSegment(sketch, "E417", {"start": v(38.83, -13.26) * mm, "end": v(39.25, -13.56) * mm});
            skLineSegment(sketch, "E418", {"start": v(39.25, -13.56) * mm, "end": v(39.66, -13.89) * mm});
            skLineSegment(sketch, "E419", {"start": v(39.66, -13.89) * mm, "end": v(40.06, -14.23) * mm});
            skLineSegment(sketch, "E420", {"start": v(40.06, -14.23) * mm, "end": v(40.46, -14.6) * mm});
            skLineSegment(sketch, "E421", {"start": v(40.46, -14.6) * mm, "end": v(40.85, -14.97) * mm});
            skLineSegment(sketch, "E422", {"start": v(40.85, -14.97) * mm, "end": v(40.13, -16.81) * mm});
            skLineSegment(sketch, "E423", {"start": v(40.13, -16.81) * mm, "end": v(39.58, -16.82) * mm});
            skLineSegment(sketch, "E424", {"start": v(39.58, -16.82) * mm, "end": v(39.05, -16.82) * mm});
            skLineSegment(sketch, "E425", {"start": v(39.05, -16.82) * mm, "end": v(38.52, -16.8) * mm});
            skLineSegment(sketch, "E426", {"start": v(38.52, -16.8) * mm, "end": v(38, -16.76) * mm});
            skLineSegment(sketch, "E427", {"start": v(38, -16.76) * mm, "end": v(37.48, -16.7) * mm});
            skLineSegment(sketch, "E428", {"start": v(37.48, -16.7) * mm, "end": v(37.23, -16.65) * mm});
            skLineSegment(sketch, "E429", {"start": v(37.23, -16.65) * mm, "end": v(37.1, -16.63) * mm});
            skLineSegment(sketch, "E430", {"start": v(37.1, -16.63) * mm, "end": v(36.98, -16.6) * mm});
            skLineSegment(sketch, "E431", {"start": v(36.98, -16.6) * mm, "end": v(36.04, -18.55) * mm});
            skLineSegment(sketch, "E432", {"start": v(36.04, -18.55) * mm, "end": v(36.14, -18.64) * mm});
            skLineSegment(sketch, "E433", {"start": v(36.14, -18.64) * mm, "end": v(36.23, -18.72) * mm});
            skLineSegment(sketch, "E434", {"start": v(36.23, -18.72) * mm, "end": v(36.42, -18.9) * mm});
            skLineSegment(sketch, "E435", {"start": v(36.42, -18.9) * mm, "end": v(36.79, -19.26) * mm});
            skLineSegment(sketch, "E436", {"start": v(36.79, -19.26) * mm, "end": v(37.15, -19.64) * mm});
            skLineSegment(sketch, "E437", {"start": v(37.15, -19.64) * mm, "end": v(37.5, -20.04) * mm});
            skLineSegment(sketch, "E438", {"start": v(37.5, -20.04) * mm, "end": v(37.83, -20.46) * mm});
            skLineSegment(sketch, "E439", {"start": v(37.83, -20.46) * mm, "end": v(38.16, -20.9) * mm});
            skLineSegment(sketch, "E440", {"start": v(38.16, -20.9) * mm, "end": v(37.17, -22.6) * mm});
            skLineSegment(sketch, "E441", {"start": v(37.17, -22.6) * mm, "end": v(36.64, -22.54) * mm});
            skLineSegment(sketch, "E442", {"start": v(36.64, -22.54) * mm, "end": v(36.1, -22.45) * mm});
            skLineSegment(sketch, "E443", {"start": v(36.1, -22.45) * mm, "end": v(35.58, -22.35) * mm});
            skLineSegment(sketch, "E444", {"start": v(35.58, -22.35) * mm, "end": v(35.07, -22.23) * mm});
            skLineSegment(sketch, "E445", {"start": v(35.07, -22.23) * mm, "end": v(34.58, -22.1) * mm});
            skLineSegment(sketch, "E446", {"start": v(34.58, -22.1) * mm, "end": v(34.33, -22.02) * mm});
            skLineSegment(sketch, "E447", {"start": v(34.33, -22.02) * mm, "end": v(34.2, -21.98) * mm});
            skLineSegment(sketch, "E448", {"start": v(34.2, -21.98) * mm, "end": v(34.09, -21.93) * mm});
            skLineSegment(sketch, "E449", {"start": v(34.09, -21.93) * mm, "end": v(32.87, -23.72) * mm});
            skLineSegment(sketch, "E450", {"start": v(32.87, -23.72) * mm, "end": v(32.95, -23.82) * mm});
            skLineSegment(sketch, "E451", {"start": v(32.95, -23.82) * mm, "end": v(33.04, -23.91) * mm});
            skLineSegment(sketch, "E452", {"start": v(33.04, -23.91) * mm, "end": v(33.2, -24.11) * mm});
            skLineSegment(sketch, "E453", {"start": v(33.2, -24.11) * mm, "end": v(33.5, -24.53) * mm});
            skLineSegment(sketch, "E454", {"start": v(33.5, -24.53) * mm, "end": v(33.8, -24.96) * mm});
            skLineSegment(sketch, "E455", {"start": v(33.8, -24.96) * mm, "end": v(34.1, -25.4) * mm});
            skLineSegment(sketch, "E456", {"start": v(34.1, -25.4) * mm, "end": v(34.36, -25.87) * mm});
            skLineSegment(sketch, "E457", {"start": v(34.36, -25.87) * mm, "end": v(34.62, -26.35) * mm});
            skLineSegment(sketch, "E458", {"start": v(34.62, -26.35) * mm, "end": v(33.39, -27.9) * mm});
            skLineSegment(sketch, "E459", {"start": v(33.39, -27.9) * mm, "end": v(32.87, -27.75) * mm});
            skLineSegment(sketch, "E460", {"start": v(32.87, -27.75) * mm, "end": v(32.36, -27.58) * mm});
            skLineSegment(sketch, "E461", {"start": v(32.36, -27.58) * mm, "end": v(31.86, -27.4) * mm});
            skLineSegment(sketch, "E462", {"start": v(31.86, -27.4) * mm, "end": v(31.37, -27.21) * mm});
            skLineSegment(sketch, "E463", {"start": v(31.37, -27.21) * mm, "end": v(30.9, -27) * mm});
            skLineSegment(sketch, "E464", {"start": v(30.9, -27) * mm, "end": v(30.67, -26.89) * mm});
            skLineSegment(sketch, "E465", {"start": v(30.67, -26.89) * mm, "end": v(30.55, -26.83) * mm});
            skLineSegment(sketch, "E466", {"start": v(30.55, -26.83) * mm, "end": v(30.44, -26.77) * mm});
            skLineSegment(sketch, "E467", {"start": v(30.44, -26.77) * mm, "end": v(28.97, -28.35) * mm});
            skLineSegment(sketch, "E468", {"start": v(28.97, -28.35) * mm, "end": v(29.04, -28.46) * mm});
            skLineSegment(sketch, "E469", {"start": v(29.04, -28.46) * mm, "end": v(29.1, -28.57) * mm});
            skLineSegment(sketch, "E470", {"start": v(29.1, -28.57) * mm, "end": v(29.23, -28.8) * mm});
            skLineSegment(sketch, "E471", {"start": v(29.23, -28.8) * mm, "end": v(29.48, -29.25) * mm});
            skLineSegment(sketch, "E472", {"start": v(29.48, -29.25) * mm, "end": v(29.7, -29.72) * mm});
            skLineSegment(sketch, "E473", {"start": v(29.7, -29.72) * mm, "end": v(29.92, -30.2) * mm});
            skLineSegment(sketch, "E474", {"start": v(29.92, -30.2) * mm, "end": v(30.12, -30.7) * mm});
            skLineSegment(sketch, "E475", {"start": v(30.12, -30.7) * mm, "end": v(30.31, -31.21) * mm});
            skLineSegment(sketch, "E476", {"start": v(30.31, -31.21) * mm, "end": v(28.86, -32.56) * mm});
            skLineSegment(sketch, "E477", {"start": v(28.86, -32.56) * mm, "end": v(28.36, -32.33) * mm});
            skLineSegment(sketch, "E478", {"start": v(28.36, -32.33) * mm, "end": v(27.88, -32.1) * mm});
            skLineSegment(sketch, "E479", {"start": v(27.88, -32.1) * mm, "end": v(27.42, -31.85) * mm});
            skLineSegment(sketch, "E480", {"start": v(27.42, -31.85) * mm, "end": v(26.96, -31.58) * mm});
            skLineSegment(sketch, "E481", {"start": v(26.96, -31.58) * mm, "end": v(26.53, -31.3) * mm});
            skLineSegment(sketch, "E482", {"start": v(26.53, -31.3) * mm, "end": v(26.32, -31.16) * mm});
            skLineSegment(sketch, "E483", {"start": v(26.32, -31.16) * mm, "end": v(26.21, -31.08) * mm});
            skLineSegment(sketch, "E484", {"start": v(26.21, -31.08) * mm, "end": v(26.1, -31) * mm});
            skLineSegment(sketch, "E485", {"start": v(26.1, -31) * mm, "end": v(24.42, -32.35) * mm});
            skLineSegment(sketch, "E486", {"start": v(24.42, -32.35) * mm, "end": v(24.47, -32.47) * mm});
            skLineSegment(sketch, "E487", {"start": v(24.47, -32.47) * mm, "end": v(24.52, -32.59) * mm});
            skLineSegment(sketch, "E488", {"start": v(24.52, -32.59) * mm, "end": v(24.62, -32.83) * mm});
            skLineSegment(sketch, "E489", {"start": v(24.62, -32.83) * mm, "end": v(24.8, -33.32) * mm});
            skLineSegment(sketch, "E490", {"start": v(24.8, -33.32) * mm, "end": v(24.95, -33.82) * mm});
            skLineSegment(sketch, "E491", {"start": v(24.95, -33.82) * mm, "end": v(25.09, -34.33) * mm});
            skLineSegment(sketch, "E492", {"start": v(25.09, -34.33) * mm, "end": v(25.21, -34.85) * mm});
            skLineSegment(sketch, "E493", {"start": v(25.21, -34.85) * mm, "end": v(25.32, -35.38) * mm});
            skLineSegment(sketch, "E494", {"start": v(25.32, -35.38) * mm, "end": v(23.68, -36.5) * mm});
            skLineSegment(sketch, "E495", {"start": v(23.68, -36.5) * mm, "end": v(23.23, -36.2) * mm});
            skLineSegment(sketch, "E496", {"start": v(23.23, -36.2) * mm, "end": v(22.79, -35.9) * mm});
            skLineSegment(sketch, "E497", {"start": v(22.79, -35.9) * mm, "end": v(22.36, -35.58) * mm});
            skLineSegment(sketch, "E498", {"start": v(22.36, -35.58) * mm, "end": v(21.96, -35.25) * mm});
            skLineSegment(sketch, "E499", {"start": v(21.96, -35.25) * mm, "end": v(21.57, -34.9) * mm});
            skLineSegment(sketch, "E500", {"start": v(21.57, -34.9) * mm, "end": v(21.38, -34.73) * mm});
            skLineSegment(sketch, "E501", {"start": v(21.38, -34.73) * mm, "end": v(21.29, -34.64) * mm});
            skLineSegment(sketch, "E502", {"start": v(21.29, -34.64) * mm, "end": v(21.2, -34.55) * mm});
            skLineSegment(sketch, "E503", {"start": v(21.2, -34.55) * mm, "end": v(19.33, -35.63) * mm});
            skLineSegment(sketch, "E504", {"start": v(19.33, -35.63) * mm, "end": v(19.36, -35.76) * mm});
            skLineSegment(sketch, "E505", {"start": v(19.36, -35.76) * mm, "end": v(19.39, -35.88) * mm});
            skLineSegment(sketch, "E506", {"start": v(19.39, -35.88) * mm, "end": v(19.45, -36.13) * mm});
            skLineSegment(sketch, "E507", {"start": v(19.45, -36.13) * mm, "end": v(19.55, -36.64) * mm});
            skLineSegment(sketch, "E508", {"start": v(19.55, -36.64) * mm, "end": v(19.63, -37.16) * mm});
            skLineSegment(sketch, "E509", {"start": v(19.63, -37.16) * mm, "end": v(19.7, -37.68) * mm});
            skLineSegment(sketch, "E510", {"start": v(19.7, -37.68) * mm, "end": v(19.74, -38.22) * mm});
            skLineSegment(sketch, "E511", {"start": v(19.74, -38.22) * mm, "end": v(19.76, -38.76) * mm});
            skLineSegment(sketch, "E512", {"start": v(19.76, -38.76) * mm, "end": v(17.98, -39.62) * mm});
            skLineSegment(sketch, "E513", {"start": v(17.98, -39.62) * mm, "end": v(17.57, -39.26) * mm});
            skLineSegment(sketch, "E514", {"start": v(17.57, -39.26) * mm, "end": v(17.18, -38.89) * mm});
            skLineSegment(sketch, "E515", {"start": v(17.18, -38.89) * mm, "end": v(16.81, -38.51) * mm});
            skLineSegment(sketch, "E516", {"start": v(16.81, -38.51) * mm, "end": v(16.46, -38.13) * mm});
            skLineSegment(sketch, "E517", {"start": v(16.46, -38.13) * mm, "end": v(16.12, -37.73) * mm});
            skLineSegment(sketch, "E518", {"start": v(16.12, -37.73) * mm, "end": v(15.96, -37.53) * mm});
            skLineSegment(sketch, "E519", {"start": v(15.96, -37.53) * mm, "end": v(15.89, -37.43) * mm});
            skLineSegment(sketch, "E520", {"start": v(15.89, -37.43) * mm, "end": v(15.8, -37.33) * mm});
            skLineSegment(sketch, "E521", {"start": v(15.8, -37.33) * mm, "end": v(13.8, -38.12) * mm});
            skLineSegment(sketch, "E522", {"start": v(13.8, -38.12) * mm, "end": v(13.81, -38.24) * mm});
            skLineSegment(sketch, "E523", {"start": v(13.81, -38.24) * mm, "end": v(13.83, -38.37) * mm});
            skLineSegment(sketch, "E524", {"start": v(13.83, -38.37) * mm, "end": v(13.85, -38.62) * mm});
            skLineSegment(sketch, "E525", {"start": v(13.85, -38.62) * mm, "end": v(13.87, -39.14) * mm});
            skLineSegment(sketch, "E526", {"start": v(13.87, -39.14) * mm, "end": v(13.87, -39.67) * mm});
            skLineSegment(sketch, "E527", {"start": v(13.87, -39.67) * mm, "end": v(13.85, -40.2) * mm});
            skLineSegment(sketch, "E528", {"start": v(13.85, -40.2) * mm, "end": v(13.82, -40.73) * mm});
            skLineSegment(sketch, "E529", {"start": v(13.82, -40.73) * mm, "end": v(13.77, -41.27) * mm});
            skLineSegment(sketch, "E530", {"start": v(13.77, -41.27) * mm, "end": v(11.87, -41.86) * mm});
            skLineSegment(sketch, "E531", {"start": v(11.87, -41.86) * mm, "end": v(11.53, -41.44) * mm});
            skLineSegment(sketch, "E532", {"start": v(11.53, -41.44) * mm, "end": v(11.2, -41.02) * mm});
            skLineSegment(sketch, "E533", {"start": v(11.2, -41.02) * mm, "end": v(10.88, -40.59) * mm});
            skLineSegment(sketch, "E534", {"start": v(10.88, -40.59) * mm, "end": v(10.6, -40.15) * mm});
            skLineSegment(sketch, "E535", {"start": v(10.6, -40.15) * mm, "end": v(10.32, -39.71) * mm});
            skLineSegment(sketch, "E536", {"start": v(10.32, -39.71) * mm, "end": v(10.2, -39.49) * mm});
            skLineSegment(sketch, "E537", {"start": v(10.2, -39.49) * mm, "end": v(10.13, -39.38) * mm});
            skLineSegment(sketch, "E538", {"start": v(10.13, -39.38) * mm, "end": v(10.07, -39.27) * mm});
            skLineSegment(sketch, "E539", {"start": v(10.07, -39.27) * mm, "end": v(7.96, -39.75) * mm});
            skLineSegment(sketch, "E540", {"start": v(7.96, -39.75) * mm, "end": v(7.96, -39.87) * mm});
            skLineSegment(sketch, "E541", {"start": v(7.96, -39.87) * mm, "end": v(7.95, -40) * mm});
            skLineSegment(sketch, "E542", {"start": v(7.95, -40) * mm, "end": v(7.93, -40.26) * mm});
            skLineSegment(sketch, "E543", {"start": v(7.93, -40.26) * mm, "end": v(7.88, -40.77) * mm});
            skLineSegment(sketch, "E544", {"start": v(7.88, -40.77) * mm, "end": v(7.8, -41.3) * mm});
            skLineSegment(sketch, "E545", {"start": v(7.8, -41.3) * mm, "end": v(7.7, -41.81) * mm});
            skLineSegment(sketch, "E546", {"start": v(7.7, -41.81) * mm, "end": v(7.6, -42.34) * mm});
            skLineSegment(sketch, "E547", {"start": v(7.6, -42.34) * mm, "end": v(7.46, -42.86) * mm});
            skLineSegment(sketch, "E548", {"start": v(7.46, -42.86) * mm, "end": v(5.5, -43.16) * mm});
            skLineSegment(sketch, "E549", {"start": v(5.5, -43.16) * mm, "end": v(5.22, -42.7) * mm});
            skLineSegment(sketch, "E550", {"start": v(5.22, -42.7) * mm, "end": v(4.96, -42.23) * mm});
            skLineSegment(sketch, "E551", {"start": v(4.96, -42.23) * mm, "end": v(4.71, -41.76) * mm});
            skLineSegment(sketch, "E552", {"start": v(4.71, -41.76) * mm, "end": v(4.49, -41.28) * mm});
            skLineSegment(sketch, "E553", {"start": v(4.49, -41.28) * mm, "end": v(4.28, -40.8) * mm});
            skLineSegment(sketch, "E554", {"start": v(4.28, -40.8) * mm, "end": v(4.2, -40.57) * mm});
            skLineSegment(sketch, "E555", {"start": v(4.2, -40.57) * mm, "end": v(4.15, -40.45) * mm});
            skLineSegment(sketch, "E556", {"start": v(4.15, -40.45) * mm, "end": v(4.1, -40.33) * mm});
            skLineSegment(sketch, "E557", {"start": v(4.1, -40.33) * mm, "end": v(1.95, -40.49) * mm});
            skLineSegment(sketch, "E558", {"start": v(1.95, -40.49) * mm, "end": v(1.93, -40.61) * mm});
            skLineSegment(sketch, "E559", {"start": v(1.93, -40.61) * mm, "end": v(1.9, -40.74) * mm});
            skLineSegment(sketch, "E560", {"start": v(1.9, -40.74) * mm, "end": v(1.85, -40.99) * mm});
            skLineSegment(sketch, "E561", {"start": v(1.85, -40.99) * mm, "end": v(1.72, -41.5) * mm});
            skLineSegment(sketch, "E562", {"start": v(1.72, -41.5) * mm, "end": v(1.56, -42) * mm});
            skLineSegment(sketch, "E563", {"start": v(1.56, -42) * mm, "end": v(1.4, -42.5) * mm});
            skLineSegment(sketch, "E564", {"start": v(1.4, -42.5) * mm, "end": v(1.2, -43) * mm});
            skLineSegment(sketch, "E565", {"start": v(1.2, -43) * mm, "end": v(0.99, -43.5) * mm});
            skLineSegment(sketch, "E566", {"start": v(0.99, -43.5) * mm, "end": v(-0.99, -43.5) * mm});
            skLineSegment(sketch, "E567", {"start": v(-0.99, -43.5) * mm, "end": v(-1.2, -43) * mm});
            skLineSegment(sketch, "E568", {"start": v(-1.2, -43) * mm, "end": v(-1.4, -42.5) * mm});
            skLineSegment(sketch, "E569", {"start": v(-1.4, -42.5) * mm, "end": v(-1.56, -42) * mm});
            skLineSegment(sketch, "E570", {"start": v(-1.56, -42) * mm, "end": v(-1.72, -41.5) * mm});
            skLineSegment(sketch, "E571", {"start": v(-1.72, -41.5) * mm, "end": v(-1.85, -40.99) * mm});
            skLineSegment(sketch, "E572", {"start": v(-1.85, -40.99) * mm, "end": v(-1.9, -40.74) * mm});
            skLineSegment(sketch, "E573", {"start": v(-1.9, -40.74) * mm, "end": v(-1.93, -40.61) * mm});
            skLineSegment(sketch, "E574", {"start": v(-1.93, -40.61) * mm, "end": v(-1.95, -40.49) * mm});
            skLineSegment(sketch, "E575", {"start": v(-1.95, -40.49) * mm, "end": v(-4.1, -40.33) * mm});
            skLineSegment(sketch, "E576", {"start": v(-4.1, -40.33) * mm, "end": v(-4.15, -40.45) * mm});
            skLineSegment(sketch, "E577", {"start": v(-4.15, -40.45) * mm, "end": v(-4.2, -40.57) * mm});
            skLineSegment(sketch, "E578", {"start": v(-4.2, -40.57) * mm, "end": v(-4.28, -40.8) * mm});
            skLineSegment(sketch, "E579", {"start": v(-4.28, -40.8) * mm, "end": v(-4.49, -41.28) * mm});
            skLineSegment(sketch, "E580", {"start": v(-4.49, -41.28) * mm, "end": v(-4.71, -41.76) * mm});
            skLineSegment(sketch, "E581", {"start": v(-4.71, -41.76) * mm, "end": v(-4.96, -42.23) * mm});
            skLineSegment(sketch, "E582", {"start": v(-4.96, -42.23) * mm, "end": v(-5.22, -42.7) * mm});
            skLineSegment(sketch, "E583", {"start": v(-5.22, -42.7) * mm, "end": v(-5.5, -43.16) * mm});
            skLineSegment(sketch, "E584", {"start": v(-5.5, -43.16) * mm, "end": v(-7.46, -42.86) * mm});
            skLineSegment(sketch, "E585", {"start": v(-7.46, -42.86) * mm, "end": v(-7.6, -42.34) * mm});
            skLineSegment(sketch, "E586", {"start": v(-7.6, -42.34) * mm, "end": v(-7.7, -41.81) * mm});
            skLineSegment(sketch, "E587", {"start": v(-7.7, -41.81) * mm, "end": v(-7.8, -41.3) * mm});
            skLineSegment(sketch, "E588", {"start": v(-7.8, -41.3) * mm, "end": v(-7.88, -40.77) * mm});
            skLineSegment(sketch, "E589", {"start": v(-7.88, -40.77) * mm, "end": v(-7.93, -40.26) * mm});
            skLineSegment(sketch, "E590", {"start": v(-7.93, -40.26) * mm, "end": v(-7.95, -40) * mm});
            skLineSegment(sketch, "E591", {"start": v(-7.95, -40) * mm, "end": v(-7.96, -39.87) * mm});
            skLineSegment(sketch, "E592", {"start": v(-7.96, -39.87) * mm, "end": v(-7.96, -39.75) * mm});
            skLineSegment(sketch, "E593", {"start": v(-7.96, -39.75) * mm, "end": v(-10.07, -39.27) * mm});
            skLineSegment(sketch, "E594", {"start": v(-10.07, -39.27) * mm, "end": v(-10.13, -39.38) * mm});
            skLineSegment(sketch, "E595", {"start": v(-10.13, -39.38) * mm, "end": v(-10.2, -39.49) * mm});
            skLineSegment(sketch, "E596", {"start": v(-10.2, -39.49) * mm, "end": v(-10.32, -39.71) * mm});
            skLineSegment(sketch, "E597", {"start": v(-10.32, -39.71) * mm, "end": v(-10.6, -40.15) * mm});
            skLineSegment(sketch, "E598", {"start": v(-10.6, -40.15) * mm, "end": v(-10.88, -40.59) * mm});
            skLineSegment(sketch, "E599", {"start": v(-10.88, -40.59) * mm, "end": v(-11.2, -41.02) * mm});
            skLineSegment(sketch, "E600", {"start": v(-11.2, -41.02) * mm, "end": v(-11.53, -41.44) * mm});
            skLineSegment(sketch, "E601", {"start": v(-11.53, -41.44) * mm, "end": v(-11.87, -41.86) * mm});
            skLineSegment(sketch, "E602", {"start": v(-11.87, -41.86) * mm, "end": v(-13.77, -41.27) * mm});
            skLineSegment(sketch, "E603", {"start": v(-13.77, -41.27) * mm, "end": v(-13.82, -40.73) * mm});
            skLineSegment(sketch, "E604", {"start": v(-13.82, -40.73) * mm, "end": v(-13.85, -40.2) * mm});
            skLineSegment(sketch, "E605", {"start": v(-13.85, -40.2) * mm, "end": v(-13.87, -39.67) * mm});
            skLineSegment(sketch, "E606", {"start": v(-13.87, -39.67) * mm, "end": v(-13.87, -39.14) * mm});
            skLineSegment(sketch, "E607", {"start": v(-13.87, -39.14) * mm, "end": v(-13.85, -38.62) * mm});
            skLineSegment(sketch, "E608", {"start": v(-13.85, -38.62) * mm, "end": v(-13.83, -38.37) * mm});
            skLineSegment(sketch, "E609", {"start": v(-13.83, -38.37) * mm, "end": v(-13.81, -38.24) * mm});
            skLineSegment(sketch, "E610", {"start": v(-13.81, -38.24) * mm, "end": v(-13.8, -38.12) * mm});
            skLineSegment(sketch, "E611", {"start": v(-13.8, -38.12) * mm, "end": v(-15.8, -37.33) * mm});
            skLineSegment(sketch, "E612", {"start": v(-15.8, -37.33) * mm, "end": v(-15.89, -37.43) * mm});
            skLineSegment(sketch, "E613", {"start": v(-15.89, -37.43) * mm, "end": v(-15.96, -37.53) * mm});
            skLineSegment(sketch, "E614", {"start": v(-15.96, -37.53) * mm, "end": v(-16.12, -37.73) * mm});
            skLineSegment(sketch, "E615", {"start": v(-16.12, -37.73) * mm, "end": v(-16.46, -38.13) * mm});
            skLineSegment(sketch, "E616", {"start": v(-16.46, -38.13) * mm, "end": v(-16.81, -38.51) * mm});
            skLineSegment(sketch, "E617", {"start": v(-16.81, -38.51) * mm, "end": v(-17.18, -38.89) * mm});
            skLineSegment(sketch, "E618", {"start": v(-17.18, -38.89) * mm, "end": v(-17.57, -39.26) * mm});
            skLineSegment(sketch, "E619", {"start": v(-17.57, -39.26) * mm, "end": v(-17.98, -39.62) * mm});
            skLineSegment(sketch, "E620", {"start": v(-17.98, -39.62) * mm, "end": v(-19.76, -38.76) * mm});
            skLineSegment(sketch, "E621", {"start": v(-19.76, -38.76) * mm, "end": v(-19.74, -38.22) * mm});
            skLineSegment(sketch, "E622", {"start": v(-19.74, -38.22) * mm, "end": v(-19.7, -37.68) * mm});
            skLineSegment(sketch, "E623", {"start": v(-19.7, -37.68) * mm, "end": v(-19.63, -37.16) * mm});
            skLineSegment(sketch, "E624", {"start": v(-19.63, -37.16) * mm, "end": v(-19.55, -36.64) * mm});
            skLineSegment(sketch, "E625", {"start": v(-19.55, -36.64) * mm, "end": v(-19.45, -36.13) * mm});
            skLineSegment(sketch, "E626", {"start": v(-19.45, -36.13) * mm, "end": v(-19.39, -35.88) * mm});
            skLineSegment(sketch, "E627", {"start": v(-19.39, -35.88) * mm, "end": v(-19.36, -35.76) * mm});
            skLineSegment(sketch, "E628", {"start": v(-19.36, -35.76) * mm, "end": v(-19.33, -35.63) * mm});
            skLineSegment(sketch, "E629", {"start": v(-19.33, -35.63) * mm, "end": v(-21.2, -34.55) * mm});
            skLineSegment(sketch, "E630", {"start": v(-21.2, -34.55) * mm, "end": v(-21.29, -34.64) * mm});
            skLineSegment(sketch, "E631", {"start": v(-21.29, -34.64) * mm, "end": v(-21.38, -34.73) * mm});
            skLineSegment(sketch, "E632", {"start": v(-21.38, -34.73) * mm, "end": v(-21.57, -34.9) * mm});
            skLineSegment(sketch, "E633", {"start": v(-21.57, -34.9) * mm, "end": v(-21.96, -35.25) * mm});
            skLineSegment(sketch, "E634", {"start": v(-21.96, -35.25) * mm, "end": v(-22.36, -35.58) * mm});
            skLineSegment(sketch, "E635", {"start": v(-22.36, -35.58) * mm, "end": v(-22.79, -35.9) * mm});
            skLineSegment(sketch, "E636", {"start": v(-22.79, -35.9) * mm, "end": v(-23.23, -36.2) * mm});
            skLineSegment(sketch, "E637", {"start": v(-23.23, -36.2) * mm, "end": v(-23.68, -36.5) * mm});
            skLineSegment(sketch, "E638", {"start": v(-23.68, -36.5) * mm, "end": v(-25.32, -35.38) * mm});
            skLineSegment(sketch, "E639", {"start": v(-25.32, -35.38) * mm, "end": v(-25.21, -34.85) * mm});
            skLineSegment(sketch, "E640", {"start": v(-25.21, -34.85) * mm, "end": v(-25.09, -34.33) * mm});
            skLineSegment(sketch, "E641", {"start": v(-25.09, -34.33) * mm, "end": v(-24.95, -33.82) * mm});
            skLineSegment(sketch, "E642", {"start": v(-24.95, -33.82) * mm, "end": v(-24.8, -33.32) * mm});
            skLineSegment(sketch, "E643", {"start": v(-24.8, -33.32) * mm, "end": v(-24.62, -32.83) * mm});
            skLineSegment(sketch, "E644", {"start": v(-24.62, -32.83) * mm, "end": v(-24.52, -32.59) * mm});
            skLineSegment(sketch, "E645", {"start": v(-24.52, -32.59) * mm, "end": v(-24.47, -32.47) * mm});
            skLineSegment(sketch, "E646", {"start": v(-24.47, -32.47) * mm, "end": v(-24.42, -32.35) * mm});
            skLineSegment(sketch, "E647", {"start": v(-24.42, -32.35) * mm, "end": v(-26.1, -31) * mm});
            skLineSegment(sketch, "E648", {"start": v(-26.1, -31) * mm, "end": v(-26.21, -31.08) * mm});
            skLineSegment(sketch, "E649", {"start": v(-26.21, -31.08) * mm, "end": v(-26.32, -31.16) * mm});
            skLineSegment(sketch, "E650", {"start": v(-26.32, -31.16) * mm, "end": v(-26.53, -31.3) * mm});
            skLineSegment(sketch, "E651", {"start": v(-26.53, -31.3) * mm, "end": v(-26.96, -31.58) * mm});
            skLineSegment(sketch, "E652", {"start": v(-26.96, -31.58) * mm, "end": v(-27.42, -31.85) * mm});
            skLineSegment(sketch, "E653", {"start": v(-27.42, -31.85) * mm, "end": v(-27.88, -32.1) * mm});
            skLineSegment(sketch, "E654", {"start": v(-27.88, -32.1) * mm, "end": v(-28.37, -32.33) * mm});
            skLineSegment(sketch, "E655", {"start": v(-28.37, -32.33) * mm, "end": v(-28.86, -32.56) * mm});
            skLineSegment(sketch, "E656", {"start": v(-28.86, -32.56) * mm, "end": v(-30.31, -31.21) * mm});
            skLineSegment(sketch, "E657", {"start": v(-30.31, -31.21) * mm, "end": v(-30.12, -30.7) * mm});
            skLineSegment(sketch, "E658", {"start": v(-30.12, -30.7) * mm, "end": v(-29.92, -30.2) * mm});
            skLineSegment(sketch, "E659", {"start": v(-29.92, -30.2) * mm, "end": v(-29.7, -29.72) * mm});
            skLineSegment(sketch, "E660", {"start": v(-29.7, -29.72) * mm, "end": v(-29.48, -29.25) * mm});
            skLineSegment(sketch, "E661", {"start": v(-29.48, -29.25) * mm, "end": v(-29.23, -28.8) * mm});
            skLineSegment(sketch, "E662", {"start": v(-29.23, -28.8) * mm, "end": v(-29.1, -28.57) * mm});
            skLineSegment(sketch, "E663", {"start": v(-29.1, -28.57) * mm, "end": v(-29.04, -28.46) * mm});
            skLineSegment(sketch, "E664", {"start": v(-29.04, -28.46) * mm, "end": v(-28.97, -28.35) * mm});
            skLineSegment(sketch, "E665", {"start": v(-28.97, -28.35) * mm, "end": v(-30.44, -26.77) * mm});
            skLineSegment(sketch, "E666", {"start": v(-30.44, -26.77) * mm, "end": v(-30.55, -26.83) * mm});
            skLineSegment(sketch, "E667", {"start": v(-30.55, -26.83) * mm, "end": v(-30.67, -26.89) * mm});
            skLineSegment(sketch, "E668", {"start": v(-30.67, -26.89) * mm, "end": v(-30.9, -27) * mm});
            skLineSegment(sketch, "E669", {"start": v(-30.9, -27) * mm, "end": v(-31.37, -27.21) * mm});
            skLineSegment(sketch, "E670", {"start": v(-31.37, -27.21) * mm, "end": v(-31.86, -27.4) * mm});
            skLineSegment(sketch, "E671", {"start": v(-31.86, -27.4) * mm, "end": v(-32.36, -27.58) * mm});
            skLineSegment(sketch, "E672", {"start": v(-32.36, -27.58) * mm, "end": v(-32.87, -27.75) * mm});
            skLineSegment(sketch, "E673", {"start": v(-32.87, -27.75) * mm, "end": v(-33.39, -27.9) * mm});
            skLineSegment(sketch, "E674", {"start": v(-33.39, -27.9) * mm, "end": v(-34.62, -26.35) * mm});
            skLineSegment(sketch, "E675", {"start": v(-34.62, -26.35) * mm, "end": v(-34.36, -25.87) * mm});
            skLineSegment(sketch, "E676", {"start": v(-34.36, -25.87) * mm, "end": v(-34.1, -25.4) * mm});
            skLineSegment(sketch, "E677", {"start": v(-34.1, -25.4) * mm, "end": v(-33.8, -24.96) * mm});
            skLineSegment(sketch, "E678", {"start": v(-33.8, -24.96) * mm, "end": v(-33.5, -24.53) * mm});
            skLineSegment(sketch, "E679", {"start": v(-33.5, -24.53) * mm, "end": v(-33.2, -24.11) * mm});
            skLineSegment(sketch, "E680", {"start": v(-33.2, -24.11) * mm, "end": v(-33.04, -23.91) * mm});
            skLineSegment(sketch, "E681", {"start": v(-33.04, -23.91) * mm, "end": v(-32.96, -23.82) * mm});
            skLineSegment(sketch, "E682", {"start": v(-32.96, -23.82) * mm, "end": v(-32.87, -23.72) * mm});
            skLineSegment(sketch, "E683", {"start": v(-32.87, -23.72) * mm, "end": v(-34.09, -21.93) * mm});
            skLineSegment(sketch, "E684", {"start": v(-34.09, -21.93) * mm, "end": v(-34.2, -21.98) * mm});
            skLineSegment(sketch, "E685", {"start": v(-34.2, -21.98) * mm, "end": v(-34.33, -22.02) * mm});
            skLineSegment(sketch, "E686", {"start": v(-34.33, -22.02) * mm, "end": v(-34.58, -22.1) * mm});
            skLineSegment(sketch, "E687", {"start": v(-34.58, -22.1) * mm, "end": v(-35.07, -22.23) * mm});
            skLineSegment(sketch, "E688", {"start": v(-35.07, -22.23) * mm, "end": v(-35.59, -22.35) * mm});
            skLineSegment(sketch, "E689", {"start": v(-35.59, -22.35) * mm, "end": v(-36.1, -22.45) * mm});
            skLineSegment(sketch, "E690", {"start": v(-36.1, -22.45) * mm, "end": v(-36.64, -22.54) * mm});
            skLineSegment(sketch, "E691", {"start": v(-36.64, -22.54) * mm, "end": v(-37.17, -22.6) * mm});
            skLineSegment(sketch, "E692", {"start": v(-37.17, -22.6) * mm, "end": v(-38.16, -20.9) * mm});
            skLineSegment(sketch, "E693", {"start": v(-38.16, -20.9) * mm, "end": v(-37.83, -20.46) * mm});
            skLineSegment(sketch, "E694", {"start": v(-37.83, -20.46) * mm, "end": v(-37.5, -20.04) * mm});
            skLineSegment(sketch, "E695", {"start": v(-37.5, -20.04) * mm, "end": v(-37.15, -19.64) * mm});
            skLineSegment(sketch, "E696", {"start": v(-37.15, -19.64) * mm, "end": v(-36.8, -19.26) * mm});
            skLineSegment(sketch, "E697", {"start": v(-36.8, -19.26) * mm, "end": v(-36.42, -18.9) * mm});
            skLineSegment(sketch, "E698", {"start": v(-36.42, -18.9) * mm, "end": v(-36.23, -18.72) * mm});
            skLineSegment(sketch, "E699", {"start": v(-36.23, -18.72) * mm, "end": v(-36.14, -18.64) * mm});
            skLineSegment(sketch, "E700", {"start": v(-36.14, -18.64) * mm, "end": v(-36.04, -18.55) * mm});
            skLineSegment(sketch, "E701", {"start": v(-36.04, -18.55) * mm, "end": v(-36.98, -16.6) * mm});
            skLineSegment(sketch, "E702", {"start": v(-36.98, -16.6) * mm, "end": v(-37.1, -16.63) * mm});
            skLineSegment(sketch, "E703", {"start": v(-37.1, -16.63) * mm, "end": v(-37.23, -16.65) * mm});
            skLineSegment(sketch, "E704", {"start": v(-37.23, -16.65) * mm, "end": v(-37.48, -16.7) * mm});
            skLineSegment(sketch, "E705", {"start": v(-37.48, -16.7) * mm, "end": v(-38, -16.76) * mm});
            skLineSegment(sketch, "E706", {"start": v(-38, -16.76) * mm, "end": v(-38.52, -16.8) * mm});
            skLineSegment(sketch, "E707", {"start": v(-38.52, -16.8) * mm, "end": v(-39.05, -16.82) * mm});
            skLineSegment(sketch, "E708", {"start": v(-39.05, -16.82) * mm, "end": v(-39.59, -16.82) * mm});
            skLineSegment(sketch, "E709", {"start": v(-39.59, -16.82) * mm, "end": v(-40.13, -16.81) * mm});
            skLineSegment(sketch, "E710", {"start": v(-40.13, -16.81) * mm, "end": v(-40.85, -14.97) * mm});
            skLineSegment(sketch, "E711", {"start": v(-40.85, -14.97) * mm, "end": v(-40.46, -14.6) * mm});
            skLineSegment(sketch, "E712", {"start": v(-40.46, -14.6) * mm, "end": v(-40.06, -14.23) * mm});
            skLineSegment(sketch, "E713", {"start": v(-40.06, -14.23) * mm, "end": v(-39.66, -13.89) * mm});
            skLineSegment(sketch, "E714", {"start": v(-39.66, -13.89) * mm, "end": v(-39.25, -13.56) * mm});
            skLineSegment(sketch, "E715", {"start": v(-39.25, -13.56) * mm, "end": v(-38.83, -13.26) * mm});
            skLineSegment(sketch, "E716", {"start": v(-38.83, -13.26) * mm, "end": v(-38.62, -13.11) * mm});
            skLineSegment(sketch, "E717", {"start": v(-38.62, -13.11) * mm, "end": v(-38.51, -13.04) * mm});
            skLineSegment(sketch, "E718", {"start": v(-38.51, -13.04) * mm, "end": v(-38.4, -12.98) * mm});
            skLineSegment(sketch, "E719", {"start": v(-38.4, -12.98) * mm, "end": v(-39.04, -10.91) * mm});
            skLineSegment(sketch, "E720", {"start": v(-39.04, -10.91) * mm, "end": v(-39.17, -10.92) * mm});
            skLineSegment(sketch, "E721", {"start": v(-39.17, -10.92) * mm, "end": v(-39.3, -10.92) * mm});
            skLineSegment(sketch, "E722", {"start": v(-39.3, -10.92) * mm, "end": v(-39.55, -10.92) * mm});
            skLineSegment(sketch, "E723", {"start": v(-39.55, -10.92) * mm, "end": v(-40.07, -10.9) * mm});
            skLineSegment(sketch, "E724", {"start": v(-40.07, -10.9) * mm, "end": v(-40.6, -10.87) * mm});
            skLineSegment(sketch, "E725", {"start": v(-40.6, -10.87) * mm, "end": v(-41.12, -10.81) * mm});
            skLineSegment(sketch, "E726", {"start": v(-41.12, -10.81) * mm, "end": v(-41.65, -10.74) * mm});
            skLineSegment(sketch, "E727", {"start": v(-41.65, -10.74) * mm, "end": v(-42.19, -10.64) * mm});
            skLineSegment(sketch, "E728", {"start": v(-42.19, -10.64) * mm, "end": v(-42.63, -8.71) * mm});
            skLineSegment(sketch, "E729", {"start": v(-42.63, -8.71) * mm, "end": v(-42.18, -8.4) * mm});
            skLineSegment(sketch, "E730", {"start": v(-42.18, -8.4) * mm, "end": v(-41.74, -8.1) * mm});
            skLineSegment(sketch, "E731", {"start": v(-41.74, -8.1) * mm, "end": v(-41.29, -7.82) * mm});
            skLineSegment(sketch, "E732", {"start": v(-41.29, -7.82) * mm, "end": v(-40.83, -7.56) * mm});
            skLineSegment(sketch, "E733", {"start": v(-40.83, -7.56) * mm, "end": v(-40.37, -7.32) * mm});
            skLineSegment(sketch, "E734", {"start": v(-40.37, -7.32) * mm, "end": v(-40.14, -7.21) * mm});
            skLineSegment(sketch, "E735", {"start": v(-40.14, -7.21) * mm, "end": v(-40.02, -7.16) * mm});
            skLineSegment(sketch, "E736", {"start": v(-40.02, -7.16) * mm, "end": v(-39.9, -7.1) * mm});
            skLineSegment(sketch, "E737", {"start": v(-39.9, -7.1) * mm, "end": v(-40.23, -4.97) * mm});
            skLineSegment(sketch, "E738", {"start": v(-40.23, -4.97) * mm, "end": v(-40.36, -4.96) * mm});
            skLineSegment(sketch, "E739", {"start": v(-40.36, -4.96) * mm, "end": v(-40.48, -4.94) * mm});
            skLineSegment(sketch, "E740", {"start": v(-40.48, -4.94) * mm, "end": v(-40.74, -4.9) * mm});
            skLineSegment(sketch, "E741", {"start": v(-40.74, -4.9) * mm, "end": v(-41.25, -4.81) * mm});
            skLineSegment(sketch, "E742", {"start": v(-41.25, -4.81) * mm, "end": v(-41.76, -4.7) * mm});
            skLineSegment(sketch, "E743", {"start": v(-41.76, -4.7) * mm, "end": v(-42.27, -4.56) * mm});
            skLineSegment(sketch, "E744", {"start": v(-42.27, -4.56) * mm, "end": v(-42.79, -4.4) * mm});
            skLineSegment(sketch, "E745", {"start": v(-42.79, -4.4) * mm, "end": v(-43.3, -4.24) * mm});
            skLineSegment(sketch, "E746", {"start": v(-43.3, -4.24) * mm, "end": v(-43.45, -2.26) * mm});
            skLineSegment(sketch, "E747", {"start": v(-43.45, -2.26) * mm, "end": v(-42.96, -2.02) * mm});
            skLineSegment(sketch, "E748", {"start": v(-42.96, -2.02) * mm, "end": v(-42.48, -1.79) * mm});
            skLineSegment(sketch, "E749", {"start": v(-42.48, -1.79) * mm, "end": v(-42, -1.58) * mm});
            skLineSegment(sketch, "E750", {"start": v(-42, -1.58) * mm, "end": v(-41.5, -1.4) * mm});
            skLineSegment(sketch, "E751", {"start": v(-41.5, -1.4) * mm, "end": v(-41.01, -1.22) * mm});
            skLineSegment(sketch, "E752", {"start": v(-41.01, -1.22) * mm, "end": v(-40.77, -1.15) * mm});
            skLineSegment(sketch, "E753", {"start": v(-40.77, -1.15) * mm, "end": v(-40.64, -1.11) * mm});
            skLineSegment(sketch, "E754", {"start": v(-40.64, -1.11) * mm, "end": v(-40.52, -1.08) * mm});
            skLineSegment(sketch, "E755", {"start": v(-40.52, -1.08) * mm, "end": v(-40.52, 1.08) * mm});
            skCircle(sketch, "E756", {"center": v(0, 0) * mm, "radius": 48.28 * mm});
            skSolve(sketch);
        }
        {
            var Q0;
            Q0=makeQuery(id+"F0.imprint","IMPRINT",FACE,{"disambiguationData":[TD([[makeQuery(id+"F0.imprint","IMPRINT",EDGE,{"derivedFrom":sQuery(id+"F0.wireOp",EDGE,"E0")}),1.0]])]});
            extrude(context, id + "F1", {"entities" : qUnion([Q0]), "depth" : 2.9 * mm, "offsetDistance" : 25 * mm});
        }
        {
            var Q0;
            Q0=makeQuery(id+"F1.opExtrude","CAP_FACE",FACE,{"disambiguationData":[OSD([sQuery(id+"F0.wireOp",EDGE,"E0"),sQuery(id+"F0.wireOp",EDGE,"E1"),sQuery(id+"F0.wireOp",EDGE,"E2"),sQuery(id+"F0.wireOp",EDGE,"E3"),sQuery(id+"F0.wireOp",EDGE,"E4"),sQuery(id+"F0.wireOp",EDGE,"E5"),sQuery(id+"F0.wireOp",EDGE,"E6"),sQuery(id+"F0.wireOp",EDGE,"E7"),sQuery(id+"F0.wireOp",EDGE,"E8"),sQuery(id+"F0.wireOp",EDGE,"E9"),sQuery(id+"F0.wireOp",EDGE,"E10"),sQuery(id+"F0.wireOp",EDGE,"E11"),sQuery(id+"F0.wireOp",EDGE,"E12"),sQuery(id+"F0.wireOp",EDGE,"E13"),sQuery(id+"F0.wireOp",EDGE,"E14"),sQuery(id+"F0.wireOp",EDGE,"E15"),sQuery(id+"F0.wireOp",EDGE,"E16"),sQuery(id+"F0.wireOp",EDGE,"E17"),sQuery(id+"F0.wireOp",EDGE,"E18"),sQuery(id+"F0.wireOp",EDGE,"E19"),sQuery(id+"F0.wireOp",EDGE,"E20"),sQuery(id+"F0.wireOp",EDGE,"E21"),sQuery(id+"F0.wireOp",EDGE,"E22"),sQuery(id+"F0.wireOp",EDGE,"E23"),sQuery(id+"F0.wireOp",EDGE,"E24"),sQuery(id+"F0.wireOp",EDGE,"E25"),sQuery(id+"F0.wireOp",EDGE,"E26"),sQuery(id+"F0.wireOp",EDGE,"E27"),sQuery(id+"F0.wireOp",EDGE,"E28"),sQuery(id+"F0.wireOp",EDGE,"E29"),sQuery(id+"F0.wireOp",EDGE,"E30"),sQuery(id+"F0.wireOp",EDGE,"E31"),sQuery(id+"F0.wireOp",EDGE,"E32"),sQuery(id+"F0.wireOp",EDGE,"E33"),sQuery(id+"F0.wireOp",EDGE,"E34"),sQuery(id+"F0.wireOp",EDGE,"E35"),sQuery(id+"F0.wireOp",EDGE,"E36"),sQuery(id+"F0.wireOp",EDGE,"E37"),sQuery(id+"F0.wireOp",EDGE,"E38"),sQuery(id+"F0.wireOp",EDGE,"E39"),sQuery(id+"F0.wireOp",EDGE,"E40"),sQuery(id+"F0.wireOp",EDGE,"E41"),sQuery(id+"F0.wireOp",EDGE,"E42"),sQuery(id+"F0.wireOp",EDGE,"E43"),sQuery(id+"F0.wireOp",EDGE,"E44"),sQuery(id+"F0.wireOp",EDGE,"E45"),sQuery(id+"F0.wireOp",EDGE,"E46"),sQuery(id+"F0.wireOp",EDGE,"E47"),sQuery(id+"F0.wireOp",EDGE,"E48"),sQuery(id+"F0.wireOp",EDGE,"E49"),sQuery(id+"F0.wireOp",EDGE,"E50"),sQuery(id+"F0.wireOp",EDGE,"E51"),sQuery(id+"F0.wireOp",EDGE,"E52"),sQuery(id+"F0.wireOp",EDGE,"E53"),sQuery(id+"F0.wireOp",EDGE,"E54"),sQuery(id+"F0.wireOp",EDGE,"E55"),sQuery(id+"F0.wireOp",EDGE,"E56"),sQuery(id+"F0.wireOp",EDGE,"E57"),sQuery(id+"F0.wireOp",EDGE,"E58"),sQuery(id+"F0.wireOp",EDGE,"E59"),sQuery(id+"F0.wireOp",EDGE,"E60"),sQuery(id+"F0.wireOp",EDGE,"E61"),sQuery(id+"F0.wireOp",EDGE,"E62"),sQuery(id+"F0.wireOp",EDGE,"E63"),sQuery(id+"F0.wireOp",EDGE,"E64"),sQuery(id+"F0.wireOp",EDGE,"E65"),sQuery(id+"F0.wireOp",EDGE,"E66"),sQuery(id+"F0.wireOp",EDGE,"E67"),sQuery(id+"F0.wireOp",EDGE,"E68"),sQuery(id+"F0.wireOp",EDGE,"E69"),sQuery(id+"F0.wireOp",EDGE,"E70"),sQuery(id+"F0.wireOp",EDGE,"E71"),sQuery(id+"F0.wireOp",EDGE,"E72"),sQuery(id+"F0.wireOp",EDGE,"E73"),sQuery(id+"F0.wireOp",EDGE,"E74"),sQuery(id+"F0.wireOp",EDGE,"E75"),sQuery(id+"F0.wireOp",EDGE,"E76"),sQuery(id+"F0.wireOp",EDGE,"E77"),sQuery(id+"F0.wireOp",EDGE,"E78"),sQuery(id+"F0.wireOp",EDGE,"E79"),sQuery(id+"F0.wireOp",EDGE,"E80"),sQuery(id+"F0.wireOp",EDGE,"E81"),sQuery(id+"F0.wireOp",EDGE,"E82"),sQuery(id+"F0.wireOp",EDGE,"E83"),sQuery(id+"F0.wireOp",EDGE,"E84"),sQuery(id+"F0.wireOp",EDGE,"E85"),sQuery(id+"F0.wireOp",EDGE,"E86"),sQuery(id+"F0.wireOp",EDGE,"E87"),sQuery(id+"F0.wireOp",EDGE,"E88"),sQuery(id+"F0.wireOp",EDGE,"E89"),sQuery(id+"F0.wireOp",EDGE,"E90"),sQuery(id+"F0.wireOp",EDGE,"E91"),sQuery(id+"F0.wireOp",EDGE,"E92"),sQuery(id+"F0.wireOp",EDGE,"E93"),sQuery(id+"F0.wireOp",EDGE,"E94"),sQuery(id+"F0.wireOp",EDGE,"E95"),sQuery(id+"F0.wireOp",EDGE,"E96"),sQuery(id+"F0.wireOp",EDGE,"E97"),sQuery(id+"F0.wireOp",EDGE,"E98"),sQuery(id+"F0.wireOp",EDGE,"E99"),sQuery(id+"F0.wireOp",EDGE,"E100"),sQuery(id+"F0.wireOp",EDGE,"E101"),sQuery(id+"F0.wireOp",EDGE,"E102"),sQuery(id+"F0.wireOp",EDGE,"E103"),sQuery(id+"F0.wireOp",EDGE,"E104"),sQuery(id+"F0.wireOp",EDGE,"E105"),sQuery(id+"F0.wireOp",EDGE,"E106"),sQuery(id+"F0.wireOp",EDGE,"E107"),sQuery(id+"F0.wireOp",EDGE,"E108"),sQuery(id+"F0.wireOp",EDGE,"E109"),sQuery(id+"F0.wireOp",EDGE,"E110"),sQuery(id+"F0.wireOp",EDGE,"E111"),sQuery(id+"F0.wireOp",EDGE,"E112"),sQuery(id+"F0.wireOp",EDGE,"E113"),sQuery(id+"F0.wireOp",EDGE,"E114"),sQuery(id+"F0.wireOp",EDGE,"E115"),sQuery(id+"F0.wireOp",EDGE,"E116"),sQuery(id+"F0.wireOp",EDGE,"E117"),sQuery(id+"F0.wireOp",EDGE,"E118"),sQuery(id+"F0.wireOp",EDGE,"E119"),sQuery(id+"F0.wireOp",EDGE,"E120"),sQuery(id+"F0.wireOp",EDGE,"E121"),sQuery(id+"F0.wireOp",EDGE,"E122"),sQuery(id+"F0.wireOp",EDGE,"E123"),sQuery(id+"F0.wireOp",EDGE,"E124"),sQuery(id+"F0.wireOp",EDGE,"E125"),sQuery(id+"F0.wireOp",EDGE,"E126"),sQuery(id+"F0.wireOp",EDGE,"E127"),sQuery(id+"F0.wireOp",EDGE,"E128"),sQuery(id+"F0.wireOp",EDGE,"E129"),sQuery(id+"F0.wireOp",EDGE,"E130"),sQuery(id+"F0.wireOp",EDGE,"E131"),sQuery(id+"F0.wireOp",EDGE,"E132"),sQuery(id+"F0.wireOp",EDGE,"E133"),sQuery(id+"F0.wireOp",EDGE,"E134"),sQuery(id+"F0.wireOp",EDGE,"E135"),sQuery(id+"F0.wireOp",EDGE,"E136"),sQuery(id+"F0.wireOp",EDGE,"E137"),sQuery(id+"F0.wireOp",EDGE,"E138"),sQuery(id+"F0.wireOp",EDGE,"E139"),sQuery(id+"F0.wireOp",EDGE,"E140"),sQuery(id+"F0.wireOp",EDGE,"E141"),sQuery(id+"F0.wireOp",EDGE,"E142"),sQuery(id+"F0.wireOp",EDGE,"E143"),sQuery(id+"F0.wireOp",EDGE,"E144"),sQuery(id+"F0.wireOp",EDGE,"E145"),sQuery(id+"F0.wireOp",EDGE,"E146"),sQuery(id+"F0.wireOp",EDGE,"E147"),sQuery(id+"F0.wireOp",EDGE,"E148"),sQuery(id+"F0.wireOp",EDGE,"E149"),sQuery(id+"F0.wireOp",EDGE,"E150"),sQuery(id+"F0.wireOp",EDGE,"E151"),sQuery(id+"F0.wireOp",EDGE,"E152"),sQuery(id+"F0.wireOp",EDGE,"E153"),sQuery(id+"F0.wireOp",EDGE,"E154"),sQuery(id+"F0.wireOp",EDGE,"E155"),sQuery(id+"F0.wireOp",EDGE,"E156"),sQuery(id+"F0.wireOp",EDGE,"E157"),sQuery(id+"F0.wireOp",EDGE,"E158"),sQuery(id+"F0.wireOp",EDGE,"E159"),sQuery(id+"F0.wireOp",EDGE,"E160"),sQuery(id+"F0.wireOp",EDGE,"E161"),sQuery(id+"F0.wireOp",EDGE,"E162"),sQuery(id+"F0.wireOp",EDGE,"E163"),sQuery(id+"F0.wireOp",EDGE,"E164"),sQuery(id+"F0.wireOp",EDGE,"E165"),sQuery(id+"F0.wireOp",EDGE,"E166"),sQuery(id+"F0.wireOp",EDGE,"E167"),sQuery(id+"F0.wireOp",EDGE,"E168"),sQuery(id+"F0.wireOp",EDGE,"E169"),sQuery(id+"F0.wireOp",EDGE,"E170"),sQuery(id+"F0.wireOp",EDGE,"E171"),sQuery(id+"F0.wireOp",EDGE,"E172"),sQuery(id+"F0.wireOp",EDGE,"E173"),sQuery(id+"F0.wireOp",EDGE,"E174"),sQuery(id+"F0.wireOp",EDGE,"E175"),sQuery(id+"F0.wireOp",EDGE,"E176"),sQuery(id+"F0.wireOp",EDGE,"E177"),sQuery(id+"F0.wireOp",EDGE,"E178"),sQuery(id+"F0.wireOp",EDGE,"E179"),sQuery(id+"F0.wireOp",EDGE,"E180"),sQuery(id+"F0.wireOp",EDGE,"E181"),sQuery(id+"F0.wireOp",EDGE,"E182"),sQuery(id+"F0.wireOp",EDGE,"E183"),sQuery(id+"F0.wireOp",EDGE,"E184"),sQuery(id+"F0.wireOp",EDGE,"E185"),sQuery(id+"F0.wireOp",EDGE,"E186"),sQuery(id+"F0.wireOp",EDGE,"E187"),sQuery(id+"F0.wireOp",EDGE,"E188"),sQuery(id+"F0.wireOp",EDGE,"E189"),sQuery(id+"F0.wireOp",EDGE,"E190"),sQuery(id+"F0.wireOp",EDGE,"E191"),sQuery(id+"F0.wireOp",EDGE,"E192"),sQuery(id+"F0.wireOp",EDGE,"E193"),sQuery(id+"F0.wireOp",EDGE,"E194"),sQuery(id+"F0.wireOp",EDGE,"E195"),sQuery(id+"F0.wireOp",EDGE,"E196"),sQuery(id+"F0.wireOp",EDGE,"E197"),sQuery(id+"F0.wireOp",EDGE,"E198"),sQuery(id+"F0.wireOp",EDGE,"E199"),sQuery(id+"F0.wireOp",EDGE,"E200"),sQuery(id+"F0.wireOp",EDGE,"E201"),sQuery(id+"F0.wireOp",EDGE,"E202"),sQuery(id+"F0.wireOp",EDGE,"E203"),sQuery(id+"F0.wireOp",EDGE,"E204"),sQuery(id+"F0.wireOp",EDGE,"E205"),sQuery(id+"F0.wireOp",EDGE,"E206"),sQuery(id+"F0.wireOp",EDGE,"E207"),sQuery(id+"F0.wireOp",EDGE,"E208"),sQuery(id+"F0.wireOp",EDGE,"E209"),sQuery(id+"F0.wireOp",EDGE,"E210"),sQuery(id+"F0.wireOp",EDGE,"E211"),sQuery(id+"F0.wireOp",EDGE,"E212"),sQuery(id+"F0.wireOp",EDGE,"E213"),sQuery(id+"F0.wireOp",EDGE,"E214"),sQuery(id+"F0.wireOp",EDGE,"E215"),sQuery(id+"F0.wireOp",EDGE,"E216"),sQuery(id+"F0.wireOp",EDGE,"E217"),sQuery(id+"F0.wireOp",EDGE,"E218"),sQuery(id+"F0.wireOp",EDGE,"E219"),sQuery(id+"F0.wireOp",EDGE,"E220"),sQuery(id+"F0.wireOp",EDGE,"E221"),sQuery(id+"F0.wireOp",EDGE,"E222"),sQuery(id+"F0.wireOp",EDGE,"E223"),sQuery(id+"F0.wireOp",EDGE,"E224"),sQuery(id+"F0.wireOp",EDGE,"E225"),sQuery(id+"F0.wireOp",EDGE,"E226"),sQuery(id+"F0.wireOp",EDGE,"E227"),sQuery(id+"F0.wireOp",EDGE,"E228"),sQuery(id+"F0.wireOp",EDGE,"E229"),sQuery(id+"F0.wireOp",EDGE,"E230"),sQuery(id+"F0.wireOp",EDGE,"E231"),sQuery(id+"F0.wireOp",EDGE,"E232"),sQuery(id+"F0.wireOp",EDGE,"E233"),sQuery(id+"F0.wireOp",EDGE,"E234"),sQuery(id+"F0.wireOp",EDGE,"E235"),sQuery(id+"F0.wireOp",EDGE,"E236"),sQuery(id+"F0.wireOp",EDGE,"E237"),sQuery(id+"F0.wireOp",EDGE,"E238"),sQuery(id+"F0.wireOp",EDGE,"E239"),sQuery(id+"F0.wireOp",EDGE,"E240"),sQuery(id+"F0.wireOp",EDGE,"E241"),sQuery(id+"F0.wireOp",EDGE,"E242"),sQuery(id+"F0.wireOp",EDGE,"E243"),sQuery(id+"F0.wireOp",EDGE,"E244"),sQuery(id+"F0.wireOp",EDGE,"E245"),sQuery(id+"F0.wireOp",EDGE,"E246"),sQuery(id+"F0.wireOp",EDGE,"E247"),sQuery(id+"F0.wireOp",EDGE,"E248"),sQuery(id+"F0.wireOp",EDGE,"E249"),sQuery(id+"F0.wireOp",EDGE,"E250"),sQuery(id+"F0.wireOp",EDGE,"E251"),sQuery(id+"F0.wireOp",EDGE,"E252"),sQuery(id+"F0.wireOp",EDGE,"E253"),sQuery(id+"F0.wireOp",EDGE,"E254"),sQuery(id+"F0.wireOp",EDGE,"E255"),sQuery(id+"F0.wireOp",EDGE,"E256"),sQuery(id+"F0.wireOp",EDGE,"E257"),sQuery(id+"F0.wireOp",EDGE,"E258"),sQuery(id+"F0.wireOp",EDGE,"E259"),sQuery(id+"F0.wireOp",EDGE,"E260"),sQuery(id+"F0.wireOp",EDGE,"E261"),sQuery(id+"F0.wireOp",EDGE,"E262"),sQuery(id+"F0.wireOp",EDGE,"E263"),sQuery(id+"F0.wireOp",EDGE,"E264"),sQuery(id+"F0.wireOp",EDGE,"E265"),sQuery(id+"F0.wireOp",EDGE,"E266"),sQuery(id+"F0.wireOp",EDGE,"E267"),sQuery(id+"F0.wireOp",EDGE,"E268"),sQuery(id+"F0.wireOp",EDGE,"E269"),sQuery(id+"F0.wireOp",EDGE,"E270"),sQuery(id+"F0.wireOp",EDGE,"E271"),sQuery(id+"F0.wireOp",EDGE,"E272"),sQuery(id+"F0.wireOp",EDGE,"E273"),sQuery(id+"F0.wireOp",EDGE,"E274"),sQuery(id+"F0.wireOp",EDGE,"E275"),sQuery(id+"F0.wireOp",EDGE,"E276"),sQuery(id+"F0.wireOp",EDGE,"E277"),sQuery(id+"F0.wireOp",EDGE,"E278"),sQuery(id+"F0.wireOp",EDGE,"E279"),sQuery(id+"F0.wireOp",EDGE,"E280"),sQuery(id+"F0.wireOp",EDGE,"E281"),sQuery(id+"F0.wireOp",EDGE,"E282"),sQuery(id+"F0.wireOp",EDGE,"E283"),sQuery(id+"F0.wireOp",EDGE,"E284"),sQuery(id+"F0.wireOp",EDGE,"E285"),sQuery(id+"F0.wireOp",EDGE,"E286"),sQuery(id+"F0.wireOp",EDGE,"E287"),sQuery(id+"F0.wireOp",EDGE,"E288"),sQuery(id+"F0.wireOp",EDGE,"E289"),sQuery(id+"F0.wireOp",EDGE,"E290"),sQuery(id+"F0.wireOp",EDGE,"E291"),sQuery(id+"F0.wireOp",EDGE,"E292"),sQuery(id+"F0.wireOp",EDGE,"E293"),sQuery(id+"F0.wireOp",EDGE,"E294"),sQuery(id+"F0.wireOp",EDGE,"E295"),sQuery(id+"F0.wireOp",EDGE,"E296"),sQuery(id+"F0.wireOp",EDGE,"E297"),sQuery(id+"F0.wireOp",EDGE,"E298"),sQuery(id+"F0.wireOp",EDGE,"E299"),sQuery(id+"F0.wireOp",EDGE,"E300"),sQuery(id+"F0.wireOp",EDGE,"E301"),sQuery(id+"F0.wireOp",EDGE,"E302"),sQuery(id+"F0.wireOp",EDGE,"E303"),sQuery(id+"F0.wireOp",EDGE,"E304"),sQuery(id+"F0.wireOp",EDGE,"E305"),sQuery(id+"F0.wireOp",EDGE,"E306"),sQuery(id+"F0.wireOp",EDGE,"E307"),sQuery(id+"F0.wireOp",EDGE,"E308"),sQuery(id+"F0.wireOp",EDGE,"E309"),sQuery(id+"F0.wireOp",EDGE,"E310"),sQuery(id+"F0.wireOp",EDGE,"E311"),sQuery(id+"F0.wireOp",EDGE,"E312"),sQuery(id+"F0.wireOp",EDGE,"E313"),sQuery(id+"F0.wireOp",EDGE,"E314"),sQuery(id+"F0.wireOp",EDGE,"E315"),sQuery(id+"F0.wireOp",EDGE,"E316"),sQuery(id+"F0.wireOp",EDGE,"E317"),sQuery(id+"F0.wireOp",EDGE,"E318"),sQuery(id+"F0.wireOp",EDGE,"E319"),sQuery(id+"F0.wireOp",EDGE,"E320"),sQuery(id+"F0.wireOp",EDGE,"E321"),sQuery(id+"F0.wireOp",EDGE,"E322"),sQuery(id+"F0.wireOp",EDGE,"E323"),sQuery(id+"F0.wireOp",EDGE,"E324"),sQuery(id+"F0.wireOp",EDGE,"E325"),sQuery(id+"F0.wireOp",EDGE,"E326"),sQuery(id+"F0.wireOp",EDGE,"E327"),sQuery(id+"F0.wireOp",EDGE,"E328"),sQuery(id+"F0.wireOp",EDGE,"E329"),sQuery(id+"F0.wireOp",EDGE,"E330"),sQuery(id+"F0.wireOp",EDGE,"E331"),sQuery(id+"F0.wireOp",EDGE,"E332"),sQuery(id+"F0.wireOp",EDGE,"E333"),sQuery(id+"F0.wireOp",EDGE,"E334"),sQuery(id+"F0.wireOp",EDGE,"E335"),sQuery(id+"F0.wireOp",EDGE,"E336"),sQuery(id+"F0.wireOp",EDGE,"E337"),sQuery(id+"F0.wireOp",EDGE,"E338"),sQuery(id+"F0.wireOp",EDGE,"E339"),sQuery(id+"F0.wireOp",EDGE,"E340"),sQuery(id+"F0.wireOp",EDGE,"E341"),sQuery(id+"F0.wireOp",EDGE,"E342"),sQuery(id+"F0.wireOp",EDGE,"E343"),sQuery(id+"F0.wireOp",EDGE,"E344"),sQuery(id+"F0.wireOp",EDGE,"E345"),sQuery(id+"F0.wireOp",EDGE,"E346"),sQuery(id+"F0.wireOp",EDGE,"E347"),sQuery(id+"F0.wireOp",EDGE,"E348"),sQuery(id+"F0.wireOp",EDGE,"E349"),sQuery(id+"F0.wireOp",EDGE,"E350"),sQuery(id+"F0.wireOp",EDGE,"E351"),sQuery(id+"F0.wireOp",EDGE,"E352"),sQuery(id+"F0.wireOp",EDGE,"E353"),sQuery(id+"F0.wireOp",EDGE,"E354"),sQuery(id+"F0.wireOp",EDGE,"E355"),sQuery(id+"F0.wireOp",EDGE,"E356"),sQuery(id+"F0.wireOp",EDGE,"E357"),sQuery(id+"F0.wireOp",EDGE,"E358"),sQuery(id+"F0.wireOp",EDGE,"E359"),sQuery(id+"F0.wireOp",EDGE,"E360"),sQuery(id+"F0.wireOp",EDGE,"E361"),sQuery(id+"F0.wireOp",EDGE,"E362"),sQuery(id+"F0.wireOp",EDGE,"E363"),sQuery(id+"F0.wireOp",EDGE,"E364"),sQuery(id+"F0.wireOp",EDGE,"E365"),sQuery(id+"F0.wireOp",EDGE,"E366"),sQuery(id+"F0.wireOp",EDGE,"E367"),sQuery(id+"F0.wireOp",EDGE,"E368"),sQuery(id+"F0.wireOp",EDGE,"E369"),sQuery(id+"F0.wireOp",EDGE,"E370"),sQuery(id+"F0.wireOp",EDGE,"E371"),sQuery(id+"F0.wireOp",EDGE,"E372"),sQuery(id+"F0.wireOp",EDGE,"E373"),sQuery(id+"F0.wireOp",EDGE,"E374"),sQuery(id+"F0.wireOp",EDGE,"E375"),sQuery(id+"F0.wireOp",EDGE,"E376"),sQuery(id+"F0.wireOp",EDGE,"E377"),sQuery(id+"F0.wireOp",EDGE,"E378"),sQuery(id+"F0.wireOp",EDGE,"E379"),sQuery(id+"F0.wireOp",EDGE,"E380"),sQuery(id+"F0.wireOp",EDGE,"E381"),sQuery(id+"F0.wireOp",EDGE,"E382"),sQuery(id+"F0.wireOp",EDGE,"E383"),sQuery(id+"F0.wireOp",EDGE,"E384"),sQuery(id+"F0.wireOp",EDGE,"E385"),sQuery(id+"F0.wireOp",EDGE,"E386"),sQuery(id+"F0.wireOp",EDGE,"E387"),sQuery(id+"F0.wireOp",EDGE,"E388"),sQuery(id+"F0.wireOp",EDGE,"E389"),sQuery(id+"F0.wireOp",EDGE,"E390"),sQuery(id+"F0.wireOp",EDGE,"E391"),sQuery(id+"F0.wireOp",EDGE,"E392"),sQuery(id+"F0.wireOp",EDGE,"E393"),sQuery(id+"F0.wireOp",EDGE,"E394"),sQuery(id+"F0.wireOp",EDGE,"E395"),sQuery(id+"F0.wireOp",EDGE,"E396"),sQuery(id+"F0.wireOp",EDGE,"E397"),sQuery(id+"F0.wireOp",EDGE,"E398"),sQuery(id+"F0.wireOp",EDGE,"E399"),sQuery(id+"F0.wireOp",EDGE,"E400"),sQuery(id+"F0.wireOp",EDGE,"E401"),sQuery(id+"F0.wireOp",EDGE,"E402"),sQuery(id+"F0.wireOp",EDGE,"E403"),sQuery(id+"F0.wireOp",EDGE,"E404"),sQuery(id+"F0.wireOp",EDGE,"E405"),sQuery(id+"F0.wireOp",EDGE,"E406"),sQuery(id+"F0.wireOp",EDGE,"E407"),sQuery(id+"F0.wireOp",EDGE,"E408"),sQuery(id+"F0.wireOp",EDGE,"E409"),sQuery(id+"F0.wireOp",EDGE,"E410"),sQuery(id+"F0.wireOp",EDGE,"E411"),sQuery(id+"F0.wireOp",EDGE,"E412"),sQuery(id+"F0.wireOp",EDGE,"E413"),sQuery(id+"F0.wireOp",EDGE,"E414"),sQuery(id+"F0.wireOp",EDGE,"E415"),sQuery(id+"F0.wireOp",EDGE,"E416"),sQuery(id+"F0.wireOp",EDGE,"E417"),sQuery(id+"F0.wireOp",EDGE,"E418"),sQuery(id+"F0.wireOp",EDGE,"E419"),sQuery(id+"F0.wireOp",EDGE,"E420"),sQuery(id+"F0.wireOp",EDGE,"E421"),sQuery(id+"F0.wireOp",EDGE,"E422"),sQuery(id+"F0.wireOp",EDGE,"E423"),sQuery(id+"F0.wireOp",EDGE,"E424"),sQuery(id+"F0.wireOp",EDGE,"E425"),sQuery(id+"F0.wireOp",EDGE,"E426"),sQuery(id+"F0.wireOp",EDGE,"E427"),sQuery(id+"F0.wireOp",EDGE,"E428"),sQuery(id+"F0.wireOp",EDGE,"E429"),sQuery(id+"F0.wireOp",EDGE,"E430"),sQuery(id+"F0.wireOp",EDGE,"E431"),sQuery(id+"F0.wireOp",EDGE,"E432"),sQuery(id+"F0.wireOp",EDGE,"E433"),sQuery(id+"F0.wireOp",EDGE,"E434"),sQuery(id+"F0.wireOp",EDGE,"E435"),sQuery(id+"F0.wireOp",EDGE,"E436"),sQuery(id+"F0.wireOp",EDGE,"E437"),sQuery(id+"F0.wireOp",EDGE,"E438"),sQuery(id+"F0.wireOp",EDGE,"E439"),sQuery(id+"F0.wireOp",EDGE,"E440"),sQuery(id+"F0.wireOp",EDGE,"E441"),sQuery(id+"F0.wireOp",EDGE,"E442"),sQuery(id+"F0.wireOp",EDGE,"E443"),sQuery(id+"F0.wireOp",EDGE,"E444"),sQuery(id+"F0.wireOp",EDGE,"E445"),sQuery(id+"F0.wireOp",EDGE,"E446"),sQuery(id+"F0.wireOp",EDGE,"E447"),sQuery(id+"F0.wireOp",EDGE,"E448"),sQuery(id+"F0.wireOp",EDGE,"E449"),sQuery(id+"F0.wireOp",EDGE,"E450"),sQuery(id+"F0.wireOp",EDGE,"E451"),sQuery(id+"F0.wireOp",EDGE,"E452"),sQuery(id+"F0.wireOp",EDGE,"E453"),sQuery(id+"F0.wireOp",EDGE,"E454"),sQuery(id+"F0.wireOp",EDGE,"E455"),sQuery(id+"F0.wireOp",EDGE,"E456"),sQuery(id+"F0.wireOp",EDGE,"E457"),sQuery(id+"F0.wireOp",EDGE,"E458"),sQuery(id+"F0.wireOp",EDGE,"E459"),sQuery(id+"F0.wireOp",EDGE,"E460"),sQuery(id+"F0.wireOp",EDGE,"E461"),sQuery(id+"F0.wireOp",EDGE,"E462"),sQuery(id+"F0.wireOp",EDGE,"E463"),sQuery(id+"F0.wireOp",EDGE,"E464"),sQuery(id+"F0.wireOp",EDGE,"E465"),sQuery(id+"F0.wireOp",EDGE,"E466"),sQuery(id+"F0.wireOp",EDGE,"E467"),sQuery(id+"F0.wireOp",EDGE,"E468"),sQuery(id+"F0.wireOp",EDGE,"E469"),sQuery(id+"F0.wireOp",EDGE,"E470"),sQuery(id+"F0.wireOp",EDGE,"E471"),sQuery(id+"F0.wireOp",EDGE,"E472"),sQuery(id+"F0.wireOp",EDGE,"E473"),sQuery(id+"F0.wireOp",EDGE,"E474"),sQuery(id+"F0.wireOp",EDGE,"E475"),sQuery(id+"F0.wireOp",EDGE,"E476"),sQuery(id+"F0.wireOp",EDGE,"E477"),sQuery(id+"F0.wireOp",EDGE,"E478"),sQuery(id+"F0.wireOp",EDGE,"E479"),sQuery(id+"F0.wireOp",EDGE,"E480"),sQuery(id+"F0.wireOp",EDGE,"E481"),sQuery(id+"F0.wireOp",EDGE,"E482"),sQuery(id+"F0.wireOp",EDGE,"E483"),sQuery(id+"F0.wireOp",EDGE,"E484"),sQuery(id+"F0.wireOp",EDGE,"E485"),sQuery(id+"F0.wireOp",EDGE,"E486"),sQuery(id+"F0.wireOp",EDGE,"E487"),sQuery(id+"F0.wireOp",EDGE,"E488"),sQuery(id+"F0.wireOp",EDGE,"E489"),sQuery(id+"F0.wireOp",EDGE,"E490"),sQuery(id+"F0.wireOp",EDGE,"E491"),sQuery(id+"F0.wireOp",EDGE,"E492"),sQuery(id+"F0.wireOp",EDGE,"E493"),sQuery(id+"F0.wireOp",EDGE,"E494"),sQuery(id+"F0.wireOp",EDGE,"E495"),sQuery(id+"F0.wireOp",EDGE,"E496"),sQuery(id+"F0.wireOp",EDGE,"E497"),sQuery(id+"F0.wireOp",EDGE,"E498"),sQuery(id+"F0.wireOp",EDGE,"E499"),sQuery(id+"F0.wireOp",EDGE,"E500"),sQuery(id+"F0.wireOp",EDGE,"E501"),sQuery(id+"F0.wireOp",EDGE,"E502"),sQuery(id+"F0.wireOp",EDGE,"E503"),sQuery(id+"F0.wireOp",EDGE,"E504"),sQuery(id+"F0.wireOp",EDGE,"E505"),sQuery(id+"F0.wireOp",EDGE,"E506"),sQuery(id+"F0.wireOp",EDGE,"E507"),sQuery(id+"F0.wireOp",EDGE,"E508"),sQuery(id+"F0.wireOp",EDGE,"E509"),sQuery(id+"F0.wireOp",EDGE,"E510"),sQuery(id+"F0.wireOp",EDGE,"E511"),sQuery(id+"F0.wireOp",EDGE,"E512"),sQuery(id+"F0.wireOp",EDGE,"E513"),sQuery(id+"F0.wireOp",EDGE,"E514"),sQuery(id+"F0.wireOp",EDGE,"E515"),sQuery(id+"F0.wireOp",EDGE,"E516"),sQuery(id+"F0.wireOp",EDGE,"E517"),sQuery(id+"F0.wireOp",EDGE,"E518"),sQuery(id+"F0.wireOp",EDGE,"E519"),sQuery(id+"F0.wireOp",EDGE,"E520"),sQuery(id+"F0.wireOp",EDGE,"E521"),sQuery(id+"F0.wireOp",EDGE,"E522"),sQuery(id+"F0.wireOp",EDGE,"E523"),sQuery(id+"F0.wireOp",EDGE,"E524"),sQuery(id+"F0.wireOp",EDGE,"E525"),sQuery(id+"F0.wireOp",EDGE,"E526"),sQuery(id+"F0.wireOp",EDGE,"E527"),sQuery(id+"F0.wireOp",EDGE,"E528"),sQuery(id+"F0.wireOp",EDGE,"E529"),sQuery(id+"F0.wireOp",EDGE,"E530"),sQuery(id+"F0.wireOp",EDGE,"E531"),sQuery(id+"F0.wireOp",EDGE,"E532"),sQuery(id+"F0.wireOp",EDGE,"E533"),sQuery(id+"F0.wireOp",EDGE,"E534"),sQuery(id+"F0.wireOp",EDGE,"E535"),sQuery(id+"F0.wireOp",EDGE,"E536"),sQuery(id+"F0.wireOp",EDGE,"E537"),sQuery(id+"F0.wireOp",EDGE,"E538"),sQuery(id+"F0.wireOp",EDGE,"E539"),sQuery(id+"F0.wireOp",EDGE,"E540"),sQuery(id+"F0.wireOp",EDGE,"E541"),sQuery(id+"F0.wireOp",EDGE,"E542"),sQuery(id+"F0.wireOp",EDGE,"E543"),sQuery(id+"F0.wireOp",EDGE,"E544"),sQuery(id+"F0.wireOp",EDGE,"E545"),sQuery(id+"F0.wireOp",EDGE,"E546"),sQuery(id+"F0.wireOp",EDGE,"E547"),sQuery(id+"F0.wireOp",EDGE,"E548"),sQuery(id+"F0.wireOp",EDGE,"E549"),sQuery(id+"F0.wireOp",EDGE,"E550"),sQuery(id+"F0.wireOp",EDGE,"E551"),sQuery(id+"F0.wireOp",EDGE,"E552"),sQuery(id+"F0.wireOp",EDGE,"E553"),sQuery(id+"F0.wireOp",EDGE,"E554"),sQuery(id+"F0.wireOp",EDGE,"E555"),sQuery(id+"F0.wireOp",EDGE,"E556"),sQuery(id+"F0.wireOp",EDGE,"E557"),sQuery(id+"F0.wireOp",EDGE,"E558"),sQuery(id+"F0.wireOp",EDGE,"E559"),sQuery(id+"F0.wireOp",EDGE,"E560"),sQuery(id+"F0.wireOp",EDGE,"E561"),sQuery(id+"F0.wireOp",EDGE,"E562"),sQuery(id+"F0.wireOp",EDGE,"E563"),sQuery(id+"F0.wireOp",EDGE,"E564"),sQuery(id+"F0.wireOp",EDGE,"E565"),sQuery(id+"F0.wireOp",EDGE,"E566"),sQuery(id+"F0.wireOp",EDGE,"E567"),sQuery(id+"F0.wireOp",EDGE,"E568"),sQuery(id+"F0.wireOp",EDGE,"E569"),sQuery(id+"F0.wireOp",EDGE,"E570"),sQuery(id+"F0.wireOp",EDGE,"E571"),sQuery(id+"F0.wireOp",EDGE,"E572"),sQuery(id+"F0.wireOp",EDGE,"E573"),sQuery(id+"F0.wireOp",EDGE,"E574"),sQuery(id+"F0.wireOp",EDGE,"E575"),sQuery(id+"F0.wireOp",EDGE,"E576"),sQuery(id+"F0.wireOp",EDGE,"E577"),sQuery(id+"F0.wireOp",EDGE,"E578"),sQuery(id+"F0.wireOp",EDGE,"E579"),sQuery(id+"F0.wireOp",EDGE,"E580"),sQuery(id+"F0.wireOp",EDGE,"E581"),sQuery(id+"F0.wireOp",EDGE,"E582"),sQuery(id+"F0.wireOp",EDGE,"E583"),sQuery(id+"F0.wireOp",EDGE,"E584"),sQuery(id+"F0.wireOp",EDGE,"E585"),sQuery(id+"F0.wireOp",EDGE,"E586"),sQuery(id+"F0.wireOp",EDGE,"E587"),sQuery(id+"F0.wireOp",EDGE,"E588"),sQuery(id+"F0.wireOp",EDGE,"E589"),sQuery(id+"F0.wireOp",EDGE,"E590"),sQuery(id+"F0.wireOp",EDGE,"E591"),sQuery(id+"F0.wireOp",EDGE,"E592"),sQuery(id+"F0.wireOp",EDGE,"E593"),sQuery(id+"F0.wireOp",EDGE,"E594"),sQuery(id+"F0.wireOp",EDGE,"E595"),sQuery(id+"F0.wireOp",EDGE,"E596"),sQuery(id+"F0.wireOp",EDGE,"E597"),sQuery(id+"F0.wireOp",EDGE,"E598"),sQuery(id+"F0.wireOp",EDGE,"E599"),sQuery(id+"F0.wireOp",EDGE,"E600"),sQuery(id+"F0.wireOp",EDGE,"E601"),sQuery(id+"F0.wireOp",EDGE,"E602"),sQuery(id+"F0.wireOp",EDGE,"E603"),sQuery(id+"F0.wireOp",EDGE,"E604"),sQuery(id+"F0.wireOp",EDGE,"E605"),sQuery(id+"F0.wireOp",EDGE,"E606"),sQuery(id+"F0.wireOp",EDGE,"E607"),sQuery(id+"F0.wireOp",EDGE,"E608"),sQuery(id+"F0.wireOp",EDGE,"E609"),sQuery(id+"F0.wireOp",EDGE,"E610"),sQuery(id+"F0.wireOp",EDGE,"E611"),sQuery(id+"F0.wireOp",EDGE,"E612"),sQuery(id+"F0.wireOp",EDGE,"E613"),sQuery(id+"F0.wireOp",EDGE,"E614"),sQuery(id+"F0.wireOp",EDGE,"E615"),sQuery(id+"F0.wireOp",EDGE,"E616"),sQuery(id+"F0.wireOp",EDGE,"E617"),sQuery(id+"F0.wireOp",EDGE,"E618"),sQuery(id+"F0.wireOp",EDGE,"E619"),sQuery(id+"F0.wireOp",EDGE,"E620"),sQuery(id+"F0.wireOp",EDGE,"E621"),sQuery(id+"F0.wireOp",EDGE,"E622"),sQuery(id+"F0.wireOp",EDGE,"E623"),sQuery(id+"F0.wireOp",EDGE,"E624"),sQuery(id+"F0.wireOp",EDGE,"E625"),sQuery(id+"F0.wireOp",EDGE,"E626"),sQuery(id+"F0.wireOp",EDGE,"E627"),sQuery(id+"F0.wireOp",EDGE,"E628"),sQuery(id+"F0.wireOp",EDGE,"E629"),sQuery(id+"F0.wireOp",EDGE,"E630"),sQuery(id+"F0.wireOp",EDGE,"E631"),sQuery(id+"F0.wireOp",EDGE,"E632"),sQuery(id+"F0.wireOp",EDGE,"E633"),sQuery(id+"F0.wireOp",EDGE,"E634"),sQuery(id+"F0.wireOp",EDGE,"E635"),sQuery(id+"F0.wireOp",EDGE,"E636"),sQuery(id+"F0.wireOp",EDGE,"E637"),sQuery(id+"F0.wireOp",EDGE,"E638"),sQuery(id+"F0.wireOp",EDGE,"E639"),sQuery(id+"F0.wireOp",EDGE,"E640"),sQuery(id+"F0.wireOp",EDGE,"E641"),sQuery(id+"F0.wireOp",EDGE,"E642"),sQuery(id+"F0.wireOp",EDGE,"E643"),sQuery(id+"F0.wireOp",EDGE,"E644"),sQuery(id+"F0.wireOp",EDGE,"E645"),sQuery(id+"F0.wireOp",EDGE,"E646"),sQuery(id+"F0.wireOp",EDGE,"E647"),sQuery(id+"F0.wireOp",EDGE,"E648"),sQuery(id+"F0.wireOp",EDGE,"E649"),sQuery(id+"F0.wireOp",EDGE,"E650"),sQuery(id+"F0.wireOp",EDGE,"E651"),sQuery(id+"F0.wireOp",EDGE,"E652"),sQuery(id+"F0.wireOp",EDGE,"E653"),sQuery(id+"F0.wireOp",EDGE,"E654"),sQuery(id+"F0.wireOp",EDGE,"E655"),sQuery(id+"F0.wireOp",EDGE,"E656"),sQuery(id+"F0.wireOp",EDGE,"E657"),sQuery(id+"F0.wireOp",EDGE,"E658"),sQuery(id+"F0.wireOp",EDGE,"E659"),sQuery(id+"F0.wireOp",EDGE,"E660"),sQuery(id+"F0.wireOp",EDGE,"E661"),sQuery(id+"F0.wireOp",EDGE,"E662"),sQuery(id+"F0.wireOp",EDGE,"E663"),sQuery(id+"F0.wireOp",EDGE,"E664"),sQuery(id+"F0.wireOp",EDGE,"E665"),sQuery(id+"F0.wireOp",EDGE,"E666"),sQuery(id+"F0.wireOp",EDGE,"E667"),sQuery(id+"F0.wireOp",EDGE,"E668"),sQuery(id+"F0.wireOp",EDGE,"E669"),sQuery(id+"F0.wireOp",EDGE,"E670"),sQuery(id+"F0.wireOp",EDGE,"E671"),sQuery(id+"F0.wireOp",EDGE,"E672"),sQuery(id+"F0.wireOp",EDGE,"E673"),sQuery(id+"F0.wireOp",EDGE,"E674"),sQuery(id+"F0.wireOp",EDGE,"E675"),sQuery(id+"F0.wireOp",EDGE,"E676"),sQuery(id+"F0.wireOp",EDGE,"E677"),sQuery(id+"F0.wireOp",EDGE,"E678"),sQuery(id+"F0.wireOp",EDGE,"E679"),sQuery(id+"F0.wireOp",EDGE,"E680"),sQuery(id+"F0.wireOp",EDGE,"E681"),sQuery(id+"F0.wireOp",EDGE,"E682"),sQuery(id+"F0.wireOp",EDGE,"E683"),sQuery(id+"F0.wireOp",EDGE,"E684"),sQuery(id+"F0.wireOp",EDGE,"E685"),sQuery(id+"F0.wireOp",EDGE,"E686"),sQuery(id+"F0.wireOp",EDGE,"E687"),sQuery(id+"F0.wireOp",EDGE,"E688"),sQuery(id+"F0.wireOp",EDGE,"E689"),sQuery(id+"F0.wireOp",EDGE,"E690"),sQuery(id+"F0.wireOp",EDGE,"E691"),sQuery(id+"F0.wireOp",EDGE,"E692"),sQuery(id+"F0.wireOp",EDGE,"E693"),sQuery(id+"F0.wireOp",EDGE,"E694"),sQuery(id+"F0.wireOp",EDGE,"E695"),sQuery(id+"F0.wireOp",EDGE,"E696"),sQuery(id+"F0.wireOp",EDGE,"E697"),sQuery(id+"F0.wireOp",EDGE,"E698"),sQuery(id+"F0.wireOp",EDGE,"E699"),sQuery(id+"F0.wireOp",EDGE,"E700"),sQuery(id+"F0.wireOp",EDGE,"E701"),sQuery(id+"F0.wireOp",EDGE,"E702"),sQuery(id+"F0.wireOp",EDGE,"E703"),sQuery(id+"F0.wireOp",EDGE,"E704"),sQuery(id+"F0.wireOp",EDGE,"E705"),sQuery(id+"F0.wireOp",EDGE,"E706"),sQuery(id+"F0.wireOp",EDGE,"E707"),sQuery(id+"F0.wireOp",EDGE,"E708"),sQuery(id+"F0.wireOp",EDGE,"E709"),sQuery(id+"F0.wireOp",EDGE,"E710"),sQuery(id+"F0.wireOp",EDGE,"E711"),sQuery(id+"F0.wireOp",EDGE,"E712"),sQuery(id+"F0.wireOp",EDGE,"E713"),sQuery(id+"F0.wireOp",EDGE,"E714"),sQuery(id+"F0.wireOp",EDGE,"E715"),sQuery(id+"F0.wireOp",EDGE,"E716"),sQuery(id+"F0.wireOp",EDGE,"E717"),sQuery(id+"F0.wireOp",EDGE,"E718"),sQuery(id+"F0.wireOp",EDGE,"E719"),sQuery(id+"F0.wireOp",EDGE,"E720"),sQuery(id+"F0.wireOp",EDGE,"E721"),sQuery(id+"F0.wireOp",EDGE,"E722"),sQuery(id+"F0.wireOp",EDGE,"E723"),sQuery(id+"F0.wireOp",EDGE,"E724"),sQuery(id+"F0.wireOp",EDGE,"E725"),sQuery(id+"F0.wireOp",EDGE,"E726"),sQuery(id+"F0.wireOp",EDGE,"E727"),sQuery(id+"F0.wireOp",EDGE,"E728"),sQuery(id+"F0.wireOp",EDGE,"E729"),sQuery(id+"F0.wireOp",EDGE,"E730"),sQuery(id+"F0.wireOp",EDGE,"E731"),sQuery(id+"F0.wireOp",EDGE,"E732"),sQuery(id+"F0.wireOp",EDGE,"E733"),sQuery(id+"F0.wireOp",EDGE,"E734"),sQuery(id+"F0.wireOp",EDGE,"E735"),sQuery(id+"F0.wireOp",EDGE,"E736"),sQuery(id+"F0.wireOp",EDGE,"E737"),sQuery(id+"F0.wireOp",EDGE,"E738"),sQuery(id+"F0.wireOp",EDGE,"E739"),sQuery(id+"F0.wireOp",EDGE,"E740"),sQuery(id+"F0.wireOp",EDGE,"E741"),sQuery(id+"F0.wireOp",EDGE,"E742"),sQuery(id+"F0.wireOp",EDGE,"E743"),sQuery(id+"F0.wireOp",EDGE,"E744"),sQuery(id+"F0.wireOp",EDGE,"E745"),sQuery(id+"F0.wireOp",EDGE,"E746"),sQuery(id+"F0.wireOp",EDGE,"E747"),sQuery(id+"F0.wireOp",EDGE,"E748"),sQuery(id+"F0.wireOp",EDGE,"E749"),sQuery(id+"F0.wireOp",EDGE,"E750"),sQuery(id+"F0.wireOp",EDGE,"E751"),sQuery(id+"F0.wireOp",EDGE,"E752"),sQuery(id+"F0.wireOp",EDGE,"E753"),sQuery(id+"F0.wireOp",EDGE,"E754"),sQuery(id+"F0.wireOp",EDGE,"E755"),sQuery(id+"F0.wireOp",EDGE,"E756")])],"isStart":false});
            var sketch = newSketch(context, id + "F2", { "sketchPlane" : qUnion([Q0])});
            skLineSegment(sketch, "E757", {"start": v(0, 0) * mm, "end": v(0, 63.57) * mm, "construction": true});
            skLineSegment(sketch, "E758", {"start": v(0, 0) * mm, "end": v(55.18, -31.86) * mm, "construction": true});
            skLineSegment(sketch, "E759", {"start": v(0, 0) * mm, "end": v(-55.31, -31.93) * mm, "construction": true});
            skCircle(sketch, "E760", {"center": v(0, 50) * mm, "radius": 1.5 * mm});
            skCircle(sketch, "E761", {"center": v(-43.3, -25) * mm, "radius": 1.5 * mm});
            skCircle(sketch, "E762.0", {"center": v(0, 0) * mm, "radius": 48.28 * mm});
            skLineSegment(sketch, "E763", {"start": v(-5, 48.02) * mm, "end": v(-5, 50) * mm});
            skLineSegment(sketch, "E764.MirrorCS", {"start": v(5, 48.02) * mm, "end": v(5, 50) * mm});
            skArc(sketch, "E765", {"start": v(-5, 50) * mm, "mid": v(0, 55) * mm, "end": v(5, 50) * mm});
            skLineSegment(sketch, "E766", {"start": v(-43.3, -25) * mm, "end": v(-41.64, -27.88) * mm, "construction": true});
            skLineSegment(sketch, "E767", {"start": v(-40.8, -29.33) * mm, "end": v(-39.09, -28.34) * mm});
            skLineSegment(sketch, "E768.MirrorCS", {"start": v(-45.8, -20.67) * mm, "end": v(-44.09, -19.68) * mm});
            skArc(sketch, "E769", {"start": v(-40.8, -29.33) * mm, "mid": v(-47.63, -27.5) * mm, "end": v(-45.8, -20.67) * mm});
            skLineSegment(sketch, "E770.MirrorCS", {"start": v(40.8, -29.33) * mm, "end": v(39.09, -28.34) * mm});
            skLineSegment(sketch, "E771.MirrorCS", {"start": v(45.8, -20.67) * mm, "end": v(44.09, -19.68) * mm});
            skArc(sketch, "E772.MirrorCS", {"start": v(40.8, -29.33) * mm, "mid": v(47.63, -27.5) * mm, "end": v(45.8, -20.67) * mm});
            skCircle(sketch, "E773.MirrorC", {"center": v(43.3, -25) * mm, "radius": 1.5 * mm});
            skSolve(sketch);
        }
        {
            var Q0;
            Q0=makeQuery(id+"F2.imprint","IMPRINT",FACE,{"disambiguationData":[TD([[makeQuery(id+"F2.imprint","IMPRINT",EDGE,{"derivedFrom":sQuery(id+"F2.wireOp",EDGE,"E760")}),-1.0]])]});
            var Q1;
            Q1=makeQuery(id+"F2.imprint","IMPRINT",FACE,{"disambiguationData":[TD([[makeQuery(id+"F2.imprint","IMPRINT",EDGE,{"derivedFrom":sQuery(id+"F2.wireOp",EDGE,"E761")}),-1.0]])]});
            var Q2;
            {var subQ1=sQuery(id+"F2.wireOp",EDGE,"E770.MirrorCS");Q2=makeQuery(id+"F2.imprint","IMPRINT",FACE,{"disambiguationData":[TD([[makeQuery(id+"F2.imprint","IMPRINT",EDGE,{"derivedFrom":subQ1}),-1.0]])]});}
            extrude(context, id + "F3", {"entities" : qUnion([Q0, Q1, Q2]), "operationType" : NewBodyOperationType.ADD, "oppositeDirection" : true, "depth" : 2.9 * mm, "offsetDistance" : 25 * mm});
        }
        {
            var Q0;
            Q0=makeQuery(id+"F3.opExtrude","SWEPT_EDGE",EDGE,{"disambiguationData":[OSD([sQuery(id+"F2.wireOp",EDGE,"E762.0"),sQuery(id+"F2.wireOp",EDGE,"E764.MirrorCS")])]});
            var Q1;
            Q1=makeQuery(id+"F3.opExtrude","SWEPT_EDGE",EDGE,{"disambiguationData":[OSD([sQuery(id+"F2.wireOp",EDGE,"E762.0"),sQuery(id+"F2.wireOp",EDGE,"E763")])]});
            var Q2;
            Q2=makeQuery(id+"F3.opExtrude","SWEPT_EDGE",EDGE,{"disambiguationData":[OSD([sQuery(id+"F2.wireOp",EDGE,"E762.0"),sQuery(id+"F2.wireOp",EDGE,"E768.MirrorCS")])]});
            var Q3;
            Q3=makeQuery(id+"F3.opExtrude","SWEPT_EDGE",EDGE,{"disambiguationData":[OSD([sQuery(id+"F2.wireOp",EDGE,"E762.0"),sQuery(id+"F2.wireOp",EDGE,"E767")])]});
            var Q4;
            Q4=makeQuery(id+"F3.opExtrude","SWEPT_EDGE",EDGE,{"disambiguationData":[OSD([sQuery(id+"F2.wireOp",EDGE,"E762.0"),sQuery(id+"F2.wireOp",EDGE,"E770.MirrorCS")])]});
            var Q5;
            Q5=makeQuery(id+"F3.opExtrude","SWEPT_EDGE",EDGE,{"disambiguationData":[OSD([sQuery(id+"F2.wireOp",EDGE,"E762.0"),sQuery(id+"F2.wireOp",EDGE,"E771.MirrorCS")])]});
            fillet(context, id + "F4", {"entities" : qUnion([Q0, Q1, Q2, Q3, Q4, Q5]), "radius" : 5 * mm, "tangentPropagation" : true, "allowEdgeOverflow" : false});
        }
        {
            var Q0;
            Q0=makeQuery(id+"F1.opExtrude","SWEPT_EDGE",EDGE,{"disambiguationData":[OSD([sQuery(id+"F0.wireOp",EDGE,"E7"),sQuery(id+"F0.wireOp",EDGE,"E8")])]});
            var Q1;
            Q1=makeQuery(id+"F1.opExtrude","SWEPT_EDGE",EDGE,{"disambiguationData":[OSD([sQuery(id+"F0.wireOp",EDGE,"E745"),sQuery(id+"F0.wireOp",EDGE,"E746")])]});
            var Q2;
            Q2=makeQuery(id+"F1.opExtrude","SWEPT_EDGE",EDGE,{"disambiguationData":[OSD([sQuery(id+"F0.wireOp",EDGE,"E727"),sQuery(id+"F0.wireOp",EDGE,"E728")])]});
            var Q3;
            Q3=makeQuery(id+"F1.opExtrude","SWEPT_EDGE",EDGE,{"disambiguationData":[OSD([sQuery(id+"F0.wireOp",EDGE,"E8"),sQuery(id+"F0.wireOp",EDGE,"E9")])]});
            var Q4;
            Q4=makeQuery(id+"F1.opExtrude","SWEPT_EDGE",EDGE,{"disambiguationData":[OSD([sQuery(id+"F0.wireOp",EDGE,"E746"),sQuery(id+"F0.wireOp",EDGE,"E747")])]});
            var Q5;
            Q5=makeQuery(id+"F1.opExtrude","SWEPT_EDGE",EDGE,{"disambiguationData":[OSD([sQuery(id+"F0.wireOp",EDGE,"E728"),sQuery(id+"F0.wireOp",EDGE,"E729")])]});
            var Q6;
            Q6=makeQuery(id+"F1.opExtrude","SWEPT_EDGE",EDGE,{"disambiguationData":[OSD([sQuery(id+"F0.wireOp",EDGE,"E25"),sQuery(id+"F0.wireOp",EDGE,"E26")])]});
            var Q7;
            Q7=makeQuery(id+"F1.opExtrude","SWEPT_EDGE",EDGE,{"disambiguationData":[OSD([sQuery(id+"F0.wireOp",EDGE,"E26"),sQuery(id+"F0.wireOp",EDGE,"E27")])]});
            var Q8;
            Q8=makeQuery(id+"F1.opExtrude","SWEPT_EDGE",EDGE,{"disambiguationData":[OSD([sQuery(id+"F0.wireOp",EDGE,"E43"),sQuery(id+"F0.wireOp",EDGE,"E44")])]});
            var Q9;
            Q9=makeQuery(id+"F1.opExtrude","SWEPT_EDGE",EDGE,{"disambiguationData":[OSD([sQuery(id+"F0.wireOp",EDGE,"E44"),sQuery(id+"F0.wireOp",EDGE,"E45")])]});
            var Q10;
            Q10=makeQuery(id+"F1.opExtrude","SWEPT_EDGE",EDGE,{"disambiguationData":[OSD([sQuery(id+"F0.wireOp",EDGE,"E61"),sQuery(id+"F0.wireOp",EDGE,"E62")])]});
            var Q11;
            Q11=makeQuery(id+"F1.opExtrude","SWEPT_EDGE",EDGE,{"disambiguationData":[OSD([sQuery(id+"F0.wireOp",EDGE,"E62"),sQuery(id+"F0.wireOp",EDGE,"E63")])]});
            var Q12;
            Q12=makeQuery(id+"F1.opExtrude","SWEPT_EDGE",EDGE,{"disambiguationData":[OSD([sQuery(id+"F0.wireOp",EDGE,"E79"),sQuery(id+"F0.wireOp",EDGE,"E80")])]});
            var Q13;
            Q13=makeQuery(id+"F1.opExtrude","SWEPT_EDGE",EDGE,{"disambiguationData":[OSD([sQuery(id+"F0.wireOp",EDGE,"E80"),sQuery(id+"F0.wireOp",EDGE,"E81")])]});
            var Q14;
            Q14=makeQuery(id+"F1.opExtrude","SWEPT_EDGE",EDGE,{"disambiguationData":[OSD([sQuery(id+"F0.wireOp",EDGE,"E97"),sQuery(id+"F0.wireOp",EDGE,"E98")])]});
            var Q15;
            Q15=makeQuery(id+"F1.opExtrude","SWEPT_EDGE",EDGE,{"disambiguationData":[OSD([sQuery(id+"F0.wireOp",EDGE,"E98"),sQuery(id+"F0.wireOp",EDGE,"E99")])]});
            var Q16;
            Q16=makeQuery(id+"F1.opExtrude","SWEPT_EDGE",EDGE,{"disambiguationData":[OSD([sQuery(id+"F0.wireOp",EDGE,"E115"),sQuery(id+"F0.wireOp",EDGE,"E116")])]});
            var Q17;
            Q17=makeQuery(id+"F1.opExtrude","SWEPT_EDGE",EDGE,{"disambiguationData":[OSD([sQuery(id+"F0.wireOp",EDGE,"E116"),sQuery(id+"F0.wireOp",EDGE,"E117")])]});
            var Q18;
            Q18=makeQuery(id+"F1.opExtrude","SWEPT_EDGE",EDGE,{"disambiguationData":[OSD([sQuery(id+"F0.wireOp",EDGE,"E133"),sQuery(id+"F0.wireOp",EDGE,"E134")])]});
            var Q19;
            Q19=makeQuery(id+"F1.opExtrude","SWEPT_EDGE",EDGE,{"disambiguationData":[OSD([sQuery(id+"F0.wireOp",EDGE,"E134"),sQuery(id+"F0.wireOp",EDGE,"E135")])]});
            var Q20;
            Q20=makeQuery(id+"F1.opExtrude","SWEPT_EDGE",EDGE,{"disambiguationData":[OSD([sQuery(id+"F0.wireOp",EDGE,"E151"),sQuery(id+"F0.wireOp",EDGE,"E152")])]});
            var Q21;
            Q21=makeQuery(id+"F1.opExtrude","SWEPT_EDGE",EDGE,{"disambiguationData":[OSD([sQuery(id+"F0.wireOp",EDGE,"E152"),sQuery(id+"F0.wireOp",EDGE,"E153")])]});
            var Q22;
            Q22=makeQuery(id+"F1.opExtrude","SWEPT_EDGE",EDGE,{"disambiguationData":[OSD([sQuery(id+"F0.wireOp",EDGE,"E169"),sQuery(id+"F0.wireOp",EDGE,"E170")])]});
            var Q23;
            Q23=makeQuery(id+"F1.opExtrude","SWEPT_EDGE",EDGE,{"disambiguationData":[OSD([sQuery(id+"F0.wireOp",EDGE,"E170"),sQuery(id+"F0.wireOp",EDGE,"E171")])]});
            var Q24;
            Q24=makeQuery(id+"F1.opExtrude","SWEPT_EDGE",EDGE,{"disambiguationData":[OSD([sQuery(id+"F0.wireOp",EDGE,"E187"),sQuery(id+"F0.wireOp",EDGE,"E188")])]});
            var Q25;
            Q25=makeQuery(id+"F1.opExtrude","SWEPT_EDGE",EDGE,{"disambiguationData":[OSD([sQuery(id+"F0.wireOp",EDGE,"E188"),sQuery(id+"F0.wireOp",EDGE,"E189")])]});
            var Q26;
            Q26=makeQuery(id+"F1.opExtrude","SWEPT_EDGE",EDGE,{"disambiguationData":[OSD([sQuery(id+"F0.wireOp",EDGE,"E205"),sQuery(id+"F0.wireOp",EDGE,"E206")])]});
            var Q27;
            Q27=makeQuery(id+"F1.opExtrude","SWEPT_EDGE",EDGE,{"disambiguationData":[OSD([sQuery(id+"F0.wireOp",EDGE,"E206"),sQuery(id+"F0.wireOp",EDGE,"E207")])]});
            var Q28;
            Q28=makeQuery(id+"F1.opExtrude","SWEPT_EDGE",EDGE,{"disambiguationData":[OSD([sQuery(id+"F0.wireOp",EDGE,"E223"),sQuery(id+"F0.wireOp",EDGE,"E224")])]});
            var Q29;
            Q29=makeQuery(id+"F1.opExtrude","SWEPT_EDGE",EDGE,{"disambiguationData":[OSD([sQuery(id+"F0.wireOp",EDGE,"E224"),sQuery(id+"F0.wireOp",EDGE,"E225")])]});
            var Q30;
            Q30=makeQuery(id+"F1.opExtrude","SWEPT_EDGE",EDGE,{"disambiguationData":[OSD([sQuery(id+"F0.wireOp",EDGE,"E241"),sQuery(id+"F0.wireOp",EDGE,"E242")])]});
            var Q31;
            Q31=makeQuery(id+"F1.opExtrude","SWEPT_EDGE",EDGE,{"disambiguationData":[OSD([sQuery(id+"F0.wireOp",EDGE,"E242"),sQuery(id+"F0.wireOp",EDGE,"E243")])]});
            var Q32;
            Q32=makeQuery(id+"F1.opExtrude","SWEPT_EDGE",EDGE,{"disambiguationData":[OSD([sQuery(id+"F0.wireOp",EDGE,"E259"),sQuery(id+"F0.wireOp",EDGE,"E260")])]});
            var Q33;
            Q33=makeQuery(id+"F1.opExtrude","SWEPT_EDGE",EDGE,{"disambiguationData":[OSD([sQuery(id+"F0.wireOp",EDGE,"E260"),sQuery(id+"F0.wireOp",EDGE,"E261")])]});
            var Q34;
            Q34=makeQuery(id+"F1.opExtrude","SWEPT_EDGE",EDGE,{"disambiguationData":[OSD([sQuery(id+"F0.wireOp",EDGE,"E277"),sQuery(id+"F0.wireOp",EDGE,"E278")])]});
            var Q35;
            Q35=makeQuery(id+"F1.opExtrude","SWEPT_EDGE",EDGE,{"disambiguationData":[OSD([sQuery(id+"F0.wireOp",EDGE,"E278"),sQuery(id+"F0.wireOp",EDGE,"E279")])]});
            var Q36;
            Q36=makeQuery(id+"F1.opExtrude","SWEPT_EDGE",EDGE,{"disambiguationData":[OSD([sQuery(id+"F0.wireOp",EDGE,"E295"),sQuery(id+"F0.wireOp",EDGE,"E296")])]});
            var Q37;
            Q37=makeQuery(id+"F1.opExtrude","SWEPT_EDGE",EDGE,{"disambiguationData":[OSD([sQuery(id+"F0.wireOp",EDGE,"E296"),sQuery(id+"F0.wireOp",EDGE,"E297")])]});
            var Q38;
            Q38=makeQuery(id+"F1.opExtrude","SWEPT_EDGE",EDGE,{"disambiguationData":[OSD([sQuery(id+"F0.wireOp",EDGE,"E313"),sQuery(id+"F0.wireOp",EDGE,"E314")])]});
            var Q39;
            Q39=makeQuery(id+"F1.opExtrude","SWEPT_EDGE",EDGE,{"disambiguationData":[OSD([sQuery(id+"F0.wireOp",EDGE,"E314"),sQuery(id+"F0.wireOp",EDGE,"E315")])]});
            var Q40;
            Q40=makeQuery(id+"F1.opExtrude","SWEPT_EDGE",EDGE,{"disambiguationData":[OSD([sQuery(id+"F0.wireOp",EDGE,"E331"),sQuery(id+"F0.wireOp",EDGE,"E332")])]});
            var Q41;
            Q41=makeQuery(id+"F1.opExtrude","SWEPT_EDGE",EDGE,{"disambiguationData":[OSD([sQuery(id+"F0.wireOp",EDGE,"E332"),sQuery(id+"F0.wireOp",EDGE,"E333")])]});
            var Q42;
            Q42=makeQuery(id+"F1.opExtrude","SWEPT_EDGE",EDGE,{"disambiguationData":[OSD([sQuery(id+"F0.wireOp",EDGE,"E349"),sQuery(id+"F0.wireOp",EDGE,"E350")])]});
            var Q43;
            Q43=makeQuery(id+"F1.opExtrude","SWEPT_EDGE",EDGE,{"disambiguationData":[OSD([sQuery(id+"F0.wireOp",EDGE,"E350"),sQuery(id+"F0.wireOp",EDGE,"E351")])]});
            var Q44;
            Q44=makeQuery(id+"F1.opExtrude","SWEPT_EDGE",EDGE,{"disambiguationData":[OSD([sQuery(id+"F0.wireOp",EDGE,"E367"),sQuery(id+"F0.wireOp",EDGE,"E368")])]});
            var Q45;
            Q45=makeQuery(id+"F1.opExtrude","SWEPT_EDGE",EDGE,{"disambiguationData":[OSD([sQuery(id+"F0.wireOp",EDGE,"E368"),sQuery(id+"F0.wireOp",EDGE,"E369")])]});
            var Q46;
            Q46=makeQuery(id+"F1.opExtrude","SWEPT_EDGE",EDGE,{"disambiguationData":[OSD([sQuery(id+"F0.wireOp",EDGE,"E385"),sQuery(id+"F0.wireOp",EDGE,"E386")])]});
            var Q47;
            Q47=makeQuery(id+"F1.opExtrude","SWEPT_EDGE",EDGE,{"disambiguationData":[OSD([sQuery(id+"F0.wireOp",EDGE,"E386"),sQuery(id+"F0.wireOp",EDGE,"E387")])]});
            var Q48;
            Q48=makeQuery(id+"F1.opExtrude","SWEPT_EDGE",EDGE,{"disambiguationData":[OSD([sQuery(id+"F0.wireOp",EDGE,"E403"),sQuery(id+"F0.wireOp",EDGE,"E404")])]});
            var Q49;
            Q49=makeQuery(id+"F1.opExtrude","SWEPT_EDGE",EDGE,{"disambiguationData":[OSD([sQuery(id+"F0.wireOp",EDGE,"E404"),sQuery(id+"F0.wireOp",EDGE,"E405")])]});
            var Q50;
            Q50=makeQuery(id+"F1.opExtrude","SWEPT_EDGE",EDGE,{"disambiguationData":[OSD([sQuery(id+"F0.wireOp",EDGE,"E421"),sQuery(id+"F0.wireOp",EDGE,"E422")])]});
            var Q51;
            Q51=makeQuery(id+"F1.opExtrude","SWEPT_EDGE",EDGE,{"disambiguationData":[OSD([sQuery(id+"F0.wireOp",EDGE,"E422"),sQuery(id+"F0.wireOp",EDGE,"E423")])]});
            var Q52;
            Q52=makeQuery(id+"F1.opExtrude","SWEPT_EDGE",EDGE,{"disambiguationData":[OSD([sQuery(id+"F0.wireOp",EDGE,"E439"),sQuery(id+"F0.wireOp",EDGE,"E440")])]});
            var Q53;
            Q53=makeQuery(id+"F1.opExtrude","SWEPT_EDGE",EDGE,{"disambiguationData":[OSD([sQuery(id+"F0.wireOp",EDGE,"E440"),sQuery(id+"F0.wireOp",EDGE,"E441")])]});
            var Q54;
            Q54=makeQuery(id+"F1.opExtrude","SWEPT_EDGE",EDGE,{"disambiguationData":[OSD([sQuery(id+"F0.wireOp",EDGE,"E457"),sQuery(id+"F0.wireOp",EDGE,"E458")])]});
            var Q55;
            Q55=makeQuery(id+"F1.opExtrude","SWEPT_EDGE",EDGE,{"disambiguationData":[OSD([sQuery(id+"F0.wireOp",EDGE,"E458"),sQuery(id+"F0.wireOp",EDGE,"E459")])]});
            var Q56;
            Q56=makeQuery(id+"F1.opExtrude","SWEPT_EDGE",EDGE,{"disambiguationData":[OSD([sQuery(id+"F0.wireOp",EDGE,"E475"),sQuery(id+"F0.wireOp",EDGE,"E476")])]});
            var Q57;
            Q57=makeQuery(id+"F1.opExtrude","SWEPT_EDGE",EDGE,{"disambiguationData":[OSD([sQuery(id+"F0.wireOp",EDGE,"E476"),sQuery(id+"F0.wireOp",EDGE,"E477")])]});
            var Q58;
            Q58=makeQuery(id+"F1.opExtrude","SWEPT_EDGE",EDGE,{"disambiguationData":[OSD([sQuery(id+"F0.wireOp",EDGE,"E493"),sQuery(id+"F0.wireOp",EDGE,"E494")])]});
            var Q59;
            Q59=makeQuery(id+"F1.opExtrude","SWEPT_EDGE",EDGE,{"disambiguationData":[OSD([sQuery(id+"F0.wireOp",EDGE,"E494"),sQuery(id+"F0.wireOp",EDGE,"E495")])]});
            var Q60;
            Q60=makeQuery(id+"F1.opExtrude","SWEPT_EDGE",EDGE,{"disambiguationData":[OSD([sQuery(id+"F0.wireOp",EDGE,"E511"),sQuery(id+"F0.wireOp",EDGE,"E512")])]});
            var Q61;
            Q61=makeQuery(id+"F1.opExtrude","SWEPT_EDGE",EDGE,{"disambiguationData":[OSD([sQuery(id+"F0.wireOp",EDGE,"E512"),sQuery(id+"F0.wireOp",EDGE,"E513")])]});
            var Q62;
            Q62=makeQuery(id+"F1.opExtrude","SWEPT_EDGE",EDGE,{"disambiguationData":[OSD([sQuery(id+"F0.wireOp",EDGE,"E529"),sQuery(id+"F0.wireOp",EDGE,"E530")])]});
            var Q63;
            Q63=makeQuery(id+"F1.opExtrude","SWEPT_EDGE",EDGE,{"disambiguationData":[OSD([sQuery(id+"F0.wireOp",EDGE,"E530"),sQuery(id+"F0.wireOp",EDGE,"E531")])]});
            var Q64;
            Q64=makeQuery(id+"F1.opExtrude","SWEPT_EDGE",EDGE,{"disambiguationData":[OSD([sQuery(id+"F0.wireOp",EDGE,"E547"),sQuery(id+"F0.wireOp",EDGE,"E548")])]});
            var Q65;
            Q65=makeQuery(id+"F1.opExtrude","SWEPT_EDGE",EDGE,{"disambiguationData":[OSD([sQuery(id+"F0.wireOp",EDGE,"E548"),sQuery(id+"F0.wireOp",EDGE,"E549")])]});
            var Q66;
            Q66=makeQuery(id+"F1.opExtrude","SWEPT_EDGE",EDGE,{"disambiguationData":[OSD([sQuery(id+"F0.wireOp",EDGE,"E565"),sQuery(id+"F0.wireOp",EDGE,"E566")])]});
            var Q67;
            Q67=makeQuery(id+"F1.opExtrude","SWEPT_EDGE",EDGE,{"disambiguationData":[OSD([sQuery(id+"F0.wireOp",EDGE,"E566"),sQuery(id+"F0.wireOp",EDGE,"E567")])]});
            var Q68;
            Q68=makeQuery(id+"F1.opExtrude","SWEPT_EDGE",EDGE,{"disambiguationData":[OSD([sQuery(id+"F0.wireOp",EDGE,"E583"),sQuery(id+"F0.wireOp",EDGE,"E584")])]});
            var Q69;
            Q69=makeQuery(id+"F1.opExtrude","SWEPT_EDGE",EDGE,{"disambiguationData":[OSD([sQuery(id+"F0.wireOp",EDGE,"E584"),sQuery(id+"F0.wireOp",EDGE,"E585")])]});
            var Q70;
            Q70=makeQuery(id+"F1.opExtrude","SWEPT_EDGE",EDGE,{"disambiguationData":[OSD([sQuery(id+"F0.wireOp",EDGE,"E601"),sQuery(id+"F0.wireOp",EDGE,"E602")])]});
            var Q71;
            Q71=makeQuery(id+"F1.opExtrude","SWEPT_EDGE",EDGE,{"disambiguationData":[OSD([sQuery(id+"F0.wireOp",EDGE,"E602"),sQuery(id+"F0.wireOp",EDGE,"E603")])]});
            var Q72;
            Q72=makeQuery(id+"F1.opExtrude","SWEPT_EDGE",EDGE,{"disambiguationData":[OSD([sQuery(id+"F0.wireOp",EDGE,"E619"),sQuery(id+"F0.wireOp",EDGE,"E620")])]});
            var Q73;
            Q73=makeQuery(id+"F1.opExtrude","SWEPT_EDGE",EDGE,{"disambiguationData":[OSD([sQuery(id+"F0.wireOp",EDGE,"E620"),sQuery(id+"F0.wireOp",EDGE,"E621")])]});
            var Q74;
            Q74=makeQuery(id+"F1.opExtrude","SWEPT_EDGE",EDGE,{"disambiguationData":[OSD([sQuery(id+"F0.wireOp",EDGE,"E637"),sQuery(id+"F0.wireOp",EDGE,"E638")])]});
            var Q75;
            Q75=makeQuery(id+"F1.opExtrude","SWEPT_EDGE",EDGE,{"disambiguationData":[OSD([sQuery(id+"F0.wireOp",EDGE,"E638"),sQuery(id+"F0.wireOp",EDGE,"E639")])]});
            var Q76;
            Q76=makeQuery(id+"F1.opExtrude","SWEPT_EDGE",EDGE,{"disambiguationData":[OSD([sQuery(id+"F0.wireOp",EDGE,"E655"),sQuery(id+"F0.wireOp",EDGE,"E656")])]});
            var Q77;
            Q77=makeQuery(id+"F1.opExtrude","SWEPT_EDGE",EDGE,{"disambiguationData":[OSD([sQuery(id+"F0.wireOp",EDGE,"E656"),sQuery(id+"F0.wireOp",EDGE,"E657")])]});
            var Q78;
            Q78=makeQuery(id+"F1.opExtrude","SWEPT_EDGE",EDGE,{"disambiguationData":[OSD([sQuery(id+"F0.wireOp",EDGE,"E673"),sQuery(id+"F0.wireOp",EDGE,"E674")])]});
            var Q79;
            Q79=makeQuery(id+"F1.opExtrude","SWEPT_EDGE",EDGE,{"disambiguationData":[OSD([sQuery(id+"F0.wireOp",EDGE,"E674"),sQuery(id+"F0.wireOp",EDGE,"E675")])]});
            var Q80;
            Q80=makeQuery(id+"F1.opExtrude","SWEPT_EDGE",EDGE,{"disambiguationData":[OSD([sQuery(id+"F0.wireOp",EDGE,"E691"),sQuery(id+"F0.wireOp",EDGE,"E692")])]});
            var Q81;
            Q81=makeQuery(id+"F1.opExtrude","SWEPT_EDGE",EDGE,{"disambiguationData":[OSD([sQuery(id+"F0.wireOp",EDGE,"E692"),sQuery(id+"F0.wireOp",EDGE,"E693")])]});
            var Q82;
            Q82=makeQuery(id+"F1.opExtrude","SWEPT_EDGE",EDGE,{"disambiguationData":[OSD([sQuery(id+"F0.wireOp",EDGE,"E709"),sQuery(id+"F0.wireOp",EDGE,"E710")])]});
            var Q83;
            Q83=makeQuery(id+"F1.opExtrude","SWEPT_EDGE",EDGE,{"disambiguationData":[OSD([sQuery(id+"F0.wireOp",EDGE,"E710"),sQuery(id+"F0.wireOp",EDGE,"E711")])]});
            fillet(context, id + "F5", {"entities" : qUnion([Q0, Q1, Q2, Q3, Q4, Q5, Q6, Q7, Q8, Q9, Q10, Q11, Q12, Q13, Q14, Q15, Q16, Q17, Q18, Q19, Q20, Q21, Q22, Q23, Q24, Q25, Q26, Q27, Q28, Q29, Q30, Q31, Q32, Q33, Q34, Q35, Q36, Q37, Q38, Q39, Q40, Q41, Q42, Q43, Q44, Q45, Q46, Q47, Q48, Q49, Q50, Q51, Q52, Q53, Q54, Q55, Q56, Q57, Q58, Q59, Q60, Q61, Q62, Q63, Q64, Q65, Q66, Q67, Q68, Q69, Q70, Q71, Q72, Q73, Q74, Q75, Q76, Q77, Q78, Q79, Q80, Q81, Q82, Q83]), "radius" : 0.3 * mm, "tangentPropagation" : true, "allowEdgeOverflow" : false});
        }
        {
            var Q0;
            Q0=makeQuery(id+"F1.opExtrude","SWEPT_EDGE",EDGE,{"disambiguationData":[OSD([sQuery(id+"F0.wireOp",EDGE,"E17"),sQuery(id+"F0.wireOp",EDGE,"E18")])]});
            var Q1;
            Q1=makeQuery(id+"F1.opExtrude","SWEPT_EDGE",EDGE,{"disambiguationData":[OSD([sQuery(id+"F0.wireOp",EDGE,"E16"),sQuery(id+"F0.wireOp",EDGE,"E17")])]});
            var Q2;
            Q2=makeQuery(id+"F1.opExtrude","SWEPT_EDGE",EDGE,{"disambiguationData":[OSD([sQuery(id+"F0.wireOp",EDGE,"E0"),sQuery(id+"F0.wireOp",EDGE,"E755")])]});
            var Q3;
            Q3=makeQuery(id+"F1.opExtrude","SWEPT_EDGE",EDGE,{"disambiguationData":[OSD([sQuery(id+"F0.wireOp",EDGE,"E754"),sQuery(id+"F0.wireOp",EDGE,"E755")])]});
            var Q4;
            Q4=makeQuery(id+"F1.opExtrude","SWEPT_EDGE",EDGE,{"disambiguationData":[OSD([sQuery(id+"F0.wireOp",EDGE,"E737"),sQuery(id+"F0.wireOp",EDGE,"E738")])]});
            var Q5;
            Q5=makeQuery(id+"F1.opExtrude","SWEPT_EDGE",EDGE,{"disambiguationData":[OSD([sQuery(id+"F0.wireOp",EDGE,"E736"),sQuery(id+"F0.wireOp",EDGE,"E737")])]});
            var Q6;
            Q6=makeQuery(id+"F1.opExtrude","SWEPT_EDGE",EDGE,{"disambiguationData":[OSD([sQuery(id+"F0.wireOp",EDGE,"E719"),sQuery(id+"F0.wireOp",EDGE,"E720")])]});
            var Q7;
            Q7=makeQuery(id+"F1.opExtrude","SWEPT_EDGE",EDGE,{"disambiguationData":[OSD([sQuery(id+"F0.wireOp",EDGE,"E718"),sQuery(id+"F0.wireOp",EDGE,"E719")])]});
            var Q8;
            Q8=makeQuery(id+"F1.opExtrude","SWEPT_EDGE",EDGE,{"disambiguationData":[OSD([sQuery(id+"F0.wireOp",EDGE,"E701"),sQuery(id+"F0.wireOp",EDGE,"E702")])]});
            var Q9;
            Q9=makeQuery(id+"F1.opExtrude","SWEPT_EDGE",EDGE,{"disambiguationData":[OSD([sQuery(id+"F0.wireOp",EDGE,"E700"),sQuery(id+"F0.wireOp",EDGE,"E701")])]});
            var Q10;
            Q10=makeQuery(id+"F1.opExtrude","SWEPT_EDGE",EDGE,{"disambiguationData":[OSD([sQuery(id+"F0.wireOp",EDGE,"E683"),sQuery(id+"F0.wireOp",EDGE,"E684")])]});
            var Q11;
            Q11=makeQuery(id+"F1.opExtrude","SWEPT_EDGE",EDGE,{"disambiguationData":[OSD([sQuery(id+"F0.wireOp",EDGE,"E682"),sQuery(id+"F0.wireOp",EDGE,"E683")])]});
            var Q12;
            Q12=makeQuery(id+"F1.opExtrude","SWEPT_EDGE",EDGE,{"disambiguationData":[OSD([sQuery(id+"F0.wireOp",EDGE,"E665"),sQuery(id+"F0.wireOp",EDGE,"E666")])]});
            var Q13;
            Q13=makeQuery(id+"F1.opExtrude","SWEPT_EDGE",EDGE,{"disambiguationData":[OSD([sQuery(id+"F0.wireOp",EDGE,"E664"),sQuery(id+"F0.wireOp",EDGE,"E665")])]});
            var Q14;
            Q14=makeQuery(id+"F1.opExtrude","SWEPT_EDGE",EDGE,{"disambiguationData":[OSD([sQuery(id+"F0.wireOp",EDGE,"E647"),sQuery(id+"F0.wireOp",EDGE,"E648")])]});
            var Q15;
            Q15=makeQuery(id+"F1.opExtrude","SWEPT_EDGE",EDGE,{"disambiguationData":[OSD([sQuery(id+"F0.wireOp",EDGE,"E646"),sQuery(id+"F0.wireOp",EDGE,"E647")])]});
            var Q16;
            Q16=makeQuery(id+"F1.opExtrude","SWEPT_EDGE",EDGE,{"disambiguationData":[OSD([sQuery(id+"F0.wireOp",EDGE,"E629"),sQuery(id+"F0.wireOp",EDGE,"E630")])]});
            var Q17;
            Q17=makeQuery(id+"F1.opExtrude","SWEPT_EDGE",EDGE,{"disambiguationData":[OSD([sQuery(id+"F0.wireOp",EDGE,"E628"),sQuery(id+"F0.wireOp",EDGE,"E629")])]});
            var Q18;
            Q18=makeQuery(id+"F1.opExtrude","SWEPT_EDGE",EDGE,{"disambiguationData":[OSD([sQuery(id+"F0.wireOp",EDGE,"E611"),sQuery(id+"F0.wireOp",EDGE,"E612")])]});
            var Q19;
            Q19=makeQuery(id+"F1.opExtrude","SWEPT_EDGE",EDGE,{"disambiguationData":[OSD([sQuery(id+"F0.wireOp",EDGE,"E610"),sQuery(id+"F0.wireOp",EDGE,"E611")])]});
            var Q20;
            Q20=makeQuery(id+"F1.opExtrude","SWEPT_EDGE",EDGE,{"disambiguationData":[OSD([sQuery(id+"F0.wireOp",EDGE,"E593"),sQuery(id+"F0.wireOp",EDGE,"E594")])]});
            var Q21;
            Q21=makeQuery(id+"F1.opExtrude","SWEPT_EDGE",EDGE,{"disambiguationData":[OSD([sQuery(id+"F0.wireOp",EDGE,"E592"),sQuery(id+"F0.wireOp",EDGE,"E593")])]});
            var Q22;
            Q22=makeQuery(id+"F1.opExtrude","SWEPT_EDGE",EDGE,{"disambiguationData":[OSD([sQuery(id+"F0.wireOp",EDGE,"E575"),sQuery(id+"F0.wireOp",EDGE,"E576")])]});
            var Q23;
            Q23=makeQuery(id+"F1.opExtrude","SWEPT_EDGE",EDGE,{"disambiguationData":[OSD([sQuery(id+"F0.wireOp",EDGE,"E574"),sQuery(id+"F0.wireOp",EDGE,"E575")])]});
            var Q24;
            Q24=makeQuery(id+"F1.opExtrude","SWEPT_EDGE",EDGE,{"disambiguationData":[OSD([sQuery(id+"F0.wireOp",EDGE,"E557"),sQuery(id+"F0.wireOp",EDGE,"E558")])]});
            var Q25;
            Q25=makeQuery(id+"F1.opExtrude","SWEPT_EDGE",EDGE,{"disambiguationData":[OSD([sQuery(id+"F0.wireOp",EDGE,"E556"),sQuery(id+"F0.wireOp",EDGE,"E557")])]});
            var Q26;
            Q26=makeQuery(id+"F1.opExtrude","SWEPT_EDGE",EDGE,{"disambiguationData":[OSD([sQuery(id+"F0.wireOp",EDGE,"E539"),sQuery(id+"F0.wireOp",EDGE,"E540")])]});
            var Q27;
            Q27=makeQuery(id+"F1.opExtrude","SWEPT_EDGE",EDGE,{"disambiguationData":[OSD([sQuery(id+"F0.wireOp",EDGE,"E538"),sQuery(id+"F0.wireOp",EDGE,"E539")])]});
            var Q28;
            Q28=makeQuery(id+"F1.opExtrude","SWEPT_EDGE",EDGE,{"disambiguationData":[OSD([sQuery(id+"F0.wireOp",EDGE,"E521"),sQuery(id+"F0.wireOp",EDGE,"E522")])]});
            var Q29;
            Q29=makeQuery(id+"F1.opExtrude","SWEPT_EDGE",EDGE,{"disambiguationData":[OSD([sQuery(id+"F0.wireOp",EDGE,"E520"),sQuery(id+"F0.wireOp",EDGE,"E521")])]});
            var Q30;
            Q30=makeQuery(id+"F1.opExtrude","SWEPT_EDGE",EDGE,{"disambiguationData":[OSD([sQuery(id+"F0.wireOp",EDGE,"E503"),sQuery(id+"F0.wireOp",EDGE,"E504")])]});
            var Q31;
            Q31=makeQuery(id+"F1.opExtrude","SWEPT_EDGE",EDGE,{"disambiguationData":[OSD([sQuery(id+"F0.wireOp",EDGE,"E502"),sQuery(id+"F0.wireOp",EDGE,"E503")])]});
            var Q32;
            Q32=makeQuery(id+"F1.opExtrude","SWEPT_EDGE",EDGE,{"disambiguationData":[OSD([sQuery(id+"F0.wireOp",EDGE,"E485"),sQuery(id+"F0.wireOp",EDGE,"E486")])]});
            var Q33;
            Q33=makeQuery(id+"F1.opExtrude","SWEPT_EDGE",EDGE,{"disambiguationData":[OSD([sQuery(id+"F0.wireOp",EDGE,"E484"),sQuery(id+"F0.wireOp",EDGE,"E485")])]});
            var Q34;
            Q34=makeQuery(id+"F1.opExtrude","SWEPT_EDGE",EDGE,{"disambiguationData":[OSD([sQuery(id+"F0.wireOp",EDGE,"E467"),sQuery(id+"F0.wireOp",EDGE,"E468")])]});
            var Q35;
            Q35=makeQuery(id+"F1.opExtrude","SWEPT_EDGE",EDGE,{"disambiguationData":[OSD([sQuery(id+"F0.wireOp",EDGE,"E466"),sQuery(id+"F0.wireOp",EDGE,"E467")])]});
            var Q36;
            Q36=makeQuery(id+"F1.opExtrude","SWEPT_EDGE",EDGE,{"disambiguationData":[OSD([sQuery(id+"F0.wireOp",EDGE,"E449"),sQuery(id+"F0.wireOp",EDGE,"E450")])]});
            var Q37;
            Q37=makeQuery(id+"F1.opExtrude","SWEPT_EDGE",EDGE,{"disambiguationData":[OSD([sQuery(id+"F0.wireOp",EDGE,"E448"),sQuery(id+"F0.wireOp",EDGE,"E449")])]});
            var Q38;
            Q38=makeQuery(id+"F1.opExtrude","SWEPT_EDGE",EDGE,{"disambiguationData":[OSD([sQuery(id+"F0.wireOp",EDGE,"E431"),sQuery(id+"F0.wireOp",EDGE,"E432")])]});
            var Q39;
            Q39=makeQuery(id+"F1.opExtrude","SWEPT_EDGE",EDGE,{"disambiguationData":[OSD([sQuery(id+"F0.wireOp",EDGE,"E430"),sQuery(id+"F0.wireOp",EDGE,"E431")])]});
            var Q40;
            Q40=makeQuery(id+"F1.opExtrude","SWEPT_EDGE",EDGE,{"disambiguationData":[OSD([sQuery(id+"F0.wireOp",EDGE,"E413"),sQuery(id+"F0.wireOp",EDGE,"E414")])]});
            var Q41;
            Q41=makeQuery(id+"F1.opExtrude","SWEPT_EDGE",EDGE,{"disambiguationData":[OSD([sQuery(id+"F0.wireOp",EDGE,"E412"),sQuery(id+"F0.wireOp",EDGE,"E413")])]});
            var Q42;
            Q42=makeQuery(id+"F1.opExtrude","SWEPT_EDGE",EDGE,{"disambiguationData":[OSD([sQuery(id+"F0.wireOp",EDGE,"E395"),sQuery(id+"F0.wireOp",EDGE,"E396")])]});
            var Q43;
            Q43=makeQuery(id+"F1.opExtrude","SWEPT_EDGE",EDGE,{"disambiguationData":[OSD([sQuery(id+"F0.wireOp",EDGE,"E394"),sQuery(id+"F0.wireOp",EDGE,"E395")])]});
            var Q44;
            Q44=makeQuery(id+"F1.opExtrude","SWEPT_EDGE",EDGE,{"disambiguationData":[OSD([sQuery(id+"F0.wireOp",EDGE,"E377"),sQuery(id+"F0.wireOp",EDGE,"E378")])]});
            var Q45;
            Q45=makeQuery(id+"F1.opExtrude","SWEPT_EDGE",EDGE,{"disambiguationData":[OSD([sQuery(id+"F0.wireOp",EDGE,"E376"),sQuery(id+"F0.wireOp",EDGE,"E377")])]});
            var Q46;
            Q46=makeQuery(id+"F1.opExtrude","SWEPT_EDGE",EDGE,{"disambiguationData":[OSD([sQuery(id+"F0.wireOp",EDGE,"E359"),sQuery(id+"F0.wireOp",EDGE,"E360")])]});
            var Q47;
            Q47=makeQuery(id+"F1.opExtrude","SWEPT_EDGE",EDGE,{"disambiguationData":[OSD([sQuery(id+"F0.wireOp",EDGE,"E358"),sQuery(id+"F0.wireOp",EDGE,"E359")])]});
            var Q48;
            Q48=makeQuery(id+"F1.opExtrude","SWEPT_EDGE",EDGE,{"disambiguationData":[OSD([sQuery(id+"F0.wireOp",EDGE,"E341"),sQuery(id+"F0.wireOp",EDGE,"E342")])]});
            var Q49;
            Q49=makeQuery(id+"F1.opExtrude","SWEPT_EDGE",EDGE,{"disambiguationData":[OSD([sQuery(id+"F0.wireOp",EDGE,"E340"),sQuery(id+"F0.wireOp",EDGE,"E341")])]});
            var Q50;
            Q50=makeQuery(id+"F1.opExtrude","SWEPT_EDGE",EDGE,{"disambiguationData":[OSD([sQuery(id+"F0.wireOp",EDGE,"E323"),sQuery(id+"F0.wireOp",EDGE,"E324")])]});
            var Q51;
            Q51=makeQuery(id+"F1.opExtrude","SWEPT_EDGE",EDGE,{"disambiguationData":[OSD([sQuery(id+"F0.wireOp",EDGE,"E322"),sQuery(id+"F0.wireOp",EDGE,"E323")])]});
            var Q52;
            Q52=makeQuery(id+"F1.opExtrude","SWEPT_EDGE",EDGE,{"disambiguationData":[OSD([sQuery(id+"F0.wireOp",EDGE,"E305"),sQuery(id+"F0.wireOp",EDGE,"E306")])]});
            var Q53;
            Q53=makeQuery(id+"F1.opExtrude","SWEPT_EDGE",EDGE,{"disambiguationData":[OSD([sQuery(id+"F0.wireOp",EDGE,"E304"),sQuery(id+"F0.wireOp",EDGE,"E305")])]});
            var Q54;
            Q54=makeQuery(id+"F1.opExtrude","SWEPT_EDGE",EDGE,{"disambiguationData":[OSD([sQuery(id+"F0.wireOp",EDGE,"E286"),sQuery(id+"F0.wireOp",EDGE,"E287")])]});
            var Q55;
            Q55=makeQuery(id+"F1.opExtrude","SWEPT_EDGE",EDGE,{"disambiguationData":[OSD([sQuery(id+"F0.wireOp",EDGE,"E269"),sQuery(id+"F0.wireOp",EDGE,"E270")])]});
            var Q56;
            Q56=makeQuery(id+"F1.opExtrude","SWEPT_EDGE",EDGE,{"disambiguationData":[OSD([sQuery(id+"F0.wireOp",EDGE,"E268"),sQuery(id+"F0.wireOp",EDGE,"E269")])]});
            var Q57;
            Q57=makeQuery(id+"F1.opExtrude","SWEPT_EDGE",EDGE,{"disambiguationData":[OSD([sQuery(id+"F0.wireOp",EDGE,"E251"),sQuery(id+"F0.wireOp",EDGE,"E252")])]});
            var Q58;
            Q58=makeQuery(id+"F1.opExtrude","SWEPT_EDGE",EDGE,{"disambiguationData":[OSD([sQuery(id+"F0.wireOp",EDGE,"E250"),sQuery(id+"F0.wireOp",EDGE,"E251")])]});
            var Q59;
            Q59=makeQuery(id+"F1.opExtrude","SWEPT_EDGE",EDGE,{"disambiguationData":[OSD([sQuery(id+"F0.wireOp",EDGE,"E233"),sQuery(id+"F0.wireOp",EDGE,"E234")])]});
            var Q60;
            Q60=makeQuery(id+"F1.opExtrude","SWEPT_EDGE",EDGE,{"disambiguationData":[OSD([sQuery(id+"F0.wireOp",EDGE,"E232"),sQuery(id+"F0.wireOp",EDGE,"E233")])]});
            var Q61;
            Q61=makeQuery(id+"F1.opExtrude","SWEPT_EDGE",EDGE,{"disambiguationData":[OSD([sQuery(id+"F0.wireOp",EDGE,"E215"),sQuery(id+"F0.wireOp",EDGE,"E216")])]});
            var Q62;
            Q62=makeQuery(id+"F1.opExtrude","SWEPT_EDGE",EDGE,{"disambiguationData":[OSD([sQuery(id+"F0.wireOp",EDGE,"E214"),sQuery(id+"F0.wireOp",EDGE,"E215")])]});
            var Q63;
            Q63=makeQuery(id+"F1.opExtrude","SWEPT_EDGE",EDGE,{"disambiguationData":[OSD([sQuery(id+"F0.wireOp",EDGE,"E197"),sQuery(id+"F0.wireOp",EDGE,"E198")])]});
            var Q64;
            Q64=makeQuery(id+"F1.opExtrude","SWEPT_EDGE",EDGE,{"disambiguationData":[OSD([sQuery(id+"F0.wireOp",EDGE,"E196"),sQuery(id+"F0.wireOp",EDGE,"E197")])]});
            var Q65;
            Q65=makeQuery(id+"F1.opExtrude","SWEPT_EDGE",EDGE,{"disambiguationData":[OSD([sQuery(id+"F0.wireOp",EDGE,"E179"),sQuery(id+"F0.wireOp",EDGE,"E180")])]});
            var Q66;
            Q66=makeQuery(id+"F1.opExtrude","SWEPT_EDGE",EDGE,{"disambiguationData":[OSD([sQuery(id+"F0.wireOp",EDGE,"E178"),sQuery(id+"F0.wireOp",EDGE,"E179")])]});
            var Q67;
            Q67=makeQuery(id+"F1.opExtrude","SWEPT_EDGE",EDGE,{"disambiguationData":[OSD([sQuery(id+"F0.wireOp",EDGE,"E161"),sQuery(id+"F0.wireOp",EDGE,"E162")])]});
            var Q68;
            Q68=makeQuery(id+"F1.opExtrude","SWEPT_EDGE",EDGE,{"disambiguationData":[OSD([sQuery(id+"F0.wireOp",EDGE,"E160"),sQuery(id+"F0.wireOp",EDGE,"E161")])]});
            var Q69;
            Q69=makeQuery(id+"F1.opExtrude","SWEPT_EDGE",EDGE,{"disambiguationData":[OSD([sQuery(id+"F0.wireOp",EDGE,"E143"),sQuery(id+"F0.wireOp",EDGE,"E144")])]});
            var Q70;
            Q70=makeQuery(id+"F1.opExtrude","SWEPT_EDGE",EDGE,{"disambiguationData":[OSD([sQuery(id+"F0.wireOp",EDGE,"E142"),sQuery(id+"F0.wireOp",EDGE,"E143")])]});
            var Q71;
            Q71=makeQuery(id+"F1.opExtrude","SWEPT_EDGE",EDGE,{"disambiguationData":[OSD([sQuery(id+"F0.wireOp",EDGE,"E125"),sQuery(id+"F0.wireOp",EDGE,"E126")])]});
            var Q72;
            Q72=makeQuery(id+"F1.opExtrude","SWEPT_EDGE",EDGE,{"disambiguationData":[OSD([sQuery(id+"F0.wireOp",EDGE,"E124"),sQuery(id+"F0.wireOp",EDGE,"E125")])]});
            var Q73;
            Q73=makeQuery(id+"F1.opExtrude","SWEPT_EDGE",EDGE,{"disambiguationData":[OSD([sQuery(id+"F0.wireOp",EDGE,"E107"),sQuery(id+"F0.wireOp",EDGE,"E108")])]});
            var Q74;
            Q74=makeQuery(id+"F1.opExtrude","SWEPT_EDGE",EDGE,{"disambiguationData":[OSD([sQuery(id+"F0.wireOp",EDGE,"E106"),sQuery(id+"F0.wireOp",EDGE,"E107")])]});
            var Q75;
            Q75=makeQuery(id+"F1.opExtrude","SWEPT_EDGE",EDGE,{"disambiguationData":[OSD([sQuery(id+"F0.wireOp",EDGE,"E89"),sQuery(id+"F0.wireOp",EDGE,"E90")])]});
            var Q76;
            Q76=makeQuery(id+"F1.opExtrude","SWEPT_EDGE",EDGE,{"disambiguationData":[OSD([sQuery(id+"F0.wireOp",EDGE,"E88"),sQuery(id+"F0.wireOp",EDGE,"E89")])]});
            var Q77;
            Q77=makeQuery(id+"F1.opExtrude","SWEPT_EDGE",EDGE,{"disambiguationData":[OSD([sQuery(id+"F0.wireOp",EDGE,"E71"),sQuery(id+"F0.wireOp",EDGE,"E72")])]});
            var Q78;
            Q78=makeQuery(id+"F1.opExtrude","SWEPT_EDGE",EDGE,{"disambiguationData":[OSD([sQuery(id+"F0.wireOp",EDGE,"E70"),sQuery(id+"F0.wireOp",EDGE,"E71")])]});
            var Q79;
            Q79=makeQuery(id+"F1.opExtrude","SWEPT_EDGE",EDGE,{"disambiguationData":[OSD([sQuery(id+"F0.wireOp",EDGE,"E53"),sQuery(id+"F0.wireOp",EDGE,"E54")])]});
            var Q80;
            Q80=makeQuery(id+"F1.opExtrude","SWEPT_EDGE",EDGE,{"disambiguationData":[OSD([sQuery(id+"F0.wireOp",EDGE,"E52"),sQuery(id+"F0.wireOp",EDGE,"E53")])]});
            var Q81;
            Q81=makeQuery(id+"F1.opExtrude","SWEPT_EDGE",EDGE,{"disambiguationData":[OSD([sQuery(id+"F0.wireOp",EDGE,"E35"),sQuery(id+"F0.wireOp",EDGE,"E36")])]});
            var Q82;
            Q82=makeQuery(id+"F1.opExtrude","SWEPT_EDGE",EDGE,{"disambiguationData":[OSD([sQuery(id+"F0.wireOp",EDGE,"E34"),sQuery(id+"F0.wireOp",EDGE,"E35")])]});
            fillet(context, id + "F6", {"entities" : qUnion([Q0, Q1, Q2, Q3, Q4, Q5, Q6, Q7, Q8, Q9, Q10, Q11, Q12, Q13, Q14, Q15, Q16, Q17, Q18, Q19, Q20, Q21, Q22, Q23, Q24, Q25, Q26, Q27, Q28, Q29, Q30, Q31, Q32, Q33, Q34, Q35, Q36, Q37, Q38, Q39, Q40, Q41, Q42, Q43, Q44, Q45, Q46, Q47, Q48, Q49, Q50, Q51, Q52, Q53, Q54, Q55, Q56, Q57, Q58, Q59, Q60, Q61, Q62, Q63, Q64, Q65, Q66, Q67, Q68, Q69, Q70, Q71, Q72, Q73, Q74, Q75, Q76, Q77, Q78, Q79, Q80, Q81, Q82]), "radius" : 1 * mm, "tangentPropagation" : true, "allowEdgeOverflow" : false});
        }
    });
